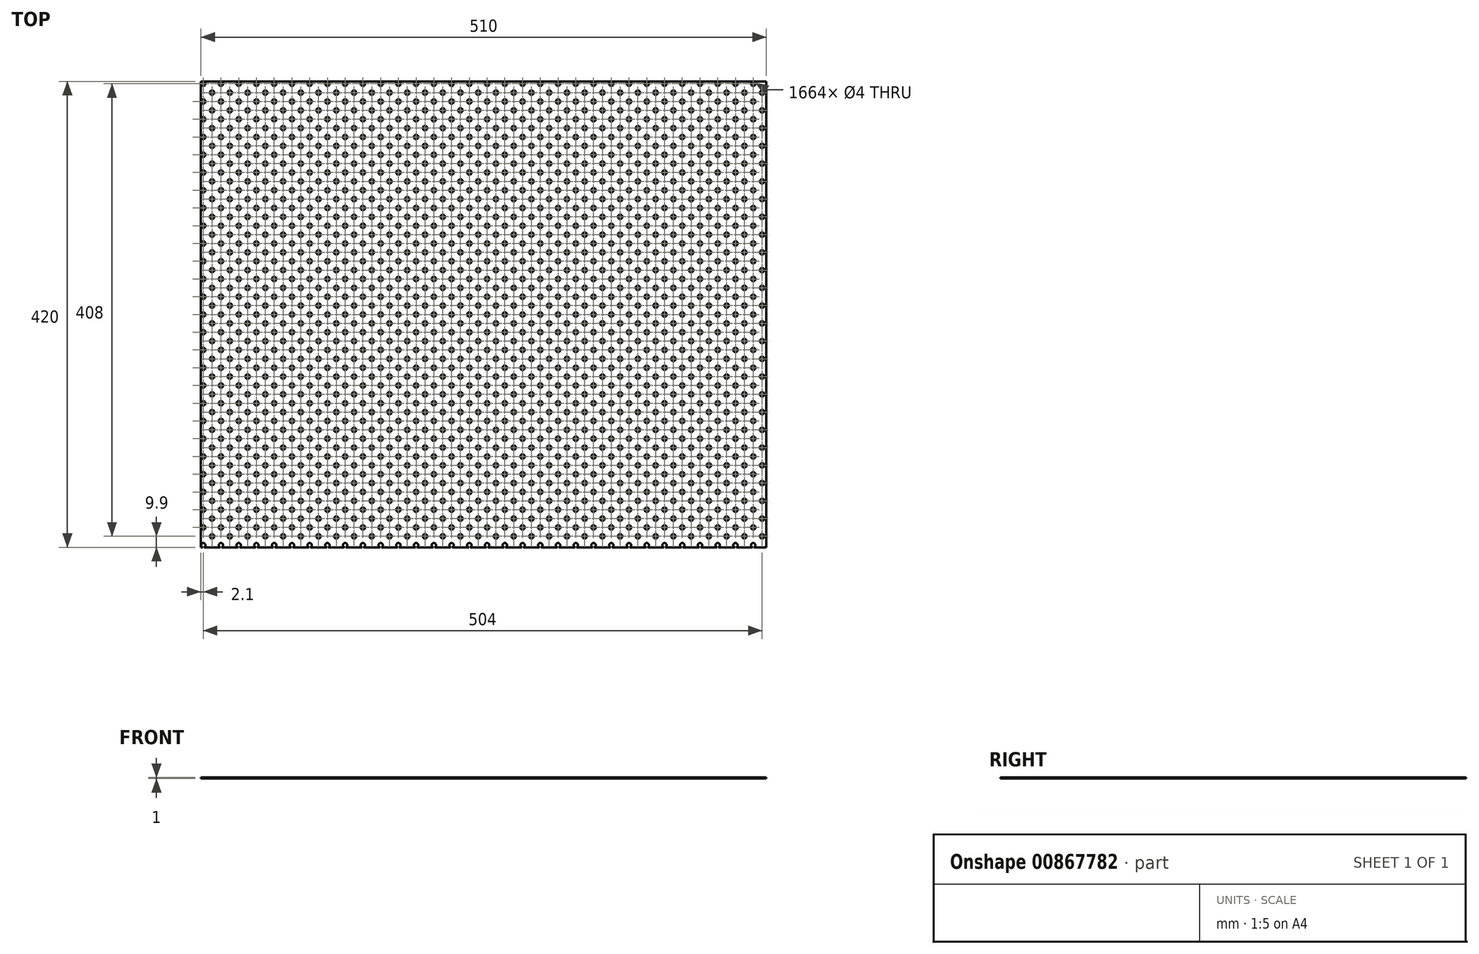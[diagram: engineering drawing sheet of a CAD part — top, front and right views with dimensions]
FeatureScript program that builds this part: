
annotation { "Feature Type Name" : "Feature", "Feature Type Description" : "" }
export const myFeature = defineFeature(function(context is Context, id is Id, definition is map)
    precondition{}
    {
        {
            var Q0;
            Q0=qCreatedBy(makeId("Top.planeOp"),FACE);
            var sketch = newSketch(context, id + "F0", { "sketchPlane" : qUnion([Q0])});
            skLineSegment(sketch, "E0.bottom", {"start": v(-115.44, 0) * mm, "end": v(394.56, 0) * mm});
            skLineSegment(sketch, "E0.top", {"start": v(-115.44, -420) * mm, "end": v(394.56, -420) * mm});
            skLineSegment(sketch, "E0.left", {"start": v(-115.44, 0) * mm, "end": v(-115.44, -420) * mm});
            skLineSegment(sketch, "E0.right", {"start": v(394.56, 0) * mm, "end": v(394.56, -420) * mm});
            skCircle(sketch, "E1", {"center": v(-113.34, -2.1) * mm, "radius": 2 * mm});
            skCircle(sketch, "E2.0.1.0", {"center": v(-113.34, -18.1) * mm, "radius": 2 * mm});
            skCircle(sketch, "E2.0.2.0", {"center": v(-113.34, -34.1) * mm, "radius": 2 * mm});
            skCircle(sketch, "E2.0.3.0", {"center": v(-113.34, -50.1) * mm, "radius": 2 * mm});
            skCircle(sketch, "E2.0.4.0", {"center": v(-113.34, -66.1) * mm, "radius": 2 * mm});
            skCircle(sketch, "E2.0.5.0", {"center": v(-113.34, -82.1) * mm, "radius": 2 * mm});
            skCircle(sketch, "E2.0.6.0", {"center": v(-113.34, -98.1) * mm, "radius": 2 * mm});
            skCircle(sketch, "E2.0.7.0", {"center": v(-113.34, -114.1) * mm, "radius": 2 * mm});
            skCircle(sketch, "E2.0.8.0", {"center": v(-113.34, -130.1) * mm, "radius": 2 * mm});
            skCircle(sketch, "E2.0.9.0", {"center": v(-113.34, -146.1) * mm, "radius": 2 * mm});
            skCircle(sketch, "E2.0.10.0", {"center": v(-113.34, -162.1) * mm, "radius": 2 * mm});
            skCircle(sketch, "E2.0.11.0", {"center": v(-113.34, -178.1) * mm, "radius": 2 * mm});
            skCircle(sketch, "E2.0.12.0", {"center": v(-113.34, -194.1) * mm, "radius": 2 * mm});
            skCircle(sketch, "E2.0.13.0", {"center": v(-113.34, -210.1) * mm, "radius": 2 * mm});
            skCircle(sketch, "E2.0.14.0", {"center": v(-113.34, -226.1) * mm, "radius": 2 * mm});
            skCircle(sketch, "E2.0.15.0", {"center": v(-113.34, -242.1) * mm, "radius": 2 * mm});
            skCircle(sketch, "E2.0.16.0", {"center": v(-113.34, -258.1) * mm, "radius": 2 * mm});
            skCircle(sketch, "E2.0.17.0", {"center": v(-113.34, -274.1) * mm, "radius": 2 * mm});
            skCircle(sketch, "E2.0.18.0", {"center": v(-113.34, -290.1) * mm, "radius": 2 * mm});
            skCircle(sketch, "E2.0.19.0", {"center": v(-113.34, -306.1) * mm, "radius": 2 * mm});
            skCircle(sketch, "E2.0.20.0", {"center": v(-113.34, -322.1) * mm, "radius": 2 * mm});
            skCircle(sketch, "E2.0.21.0", {"center": v(-113.34, -338.1) * mm, "radius": 2 * mm});
            skCircle(sketch, "E2.0.22.0", {"center": v(-113.34, -354.1) * mm, "radius": 2 * mm});
            skCircle(sketch, "E2.0.23.0", {"center": v(-113.34, -370.1) * mm, "radius": 2 * mm});
            skCircle(sketch, "E2.0.24.0", {"center": v(-113.34, -386.1) * mm, "radius": 2 * mm});
            skCircle(sketch, "E2.1.0.0", {"center": v(-97.34, -2.1) * mm, "radius": 2 * mm});
            skCircle(sketch, "E2.1.1.0", {"center": v(-97.34, -18.1) * mm, "radius": 2 * mm});
            skCircle(sketch, "E2.1.2.0", {"center": v(-97.34, -34.1) * mm, "radius": 2 * mm});
            skCircle(sketch, "E2.1.3.0", {"center": v(-97.34, -50.1) * mm, "radius": 2 * mm});
            skCircle(sketch, "E2.1.4.0", {"center": v(-97.34, -66.1) * mm, "radius": 2 * mm});
            skCircle(sketch, "E2.1.5.0", {"center": v(-97.34, -82.1) * mm, "radius": 2 * mm});
            skCircle(sketch, "E2.1.6.0", {"center": v(-97.34, -98.1) * mm, "radius": 2 * mm});
            skCircle(sketch, "E2.1.7.0", {"center": v(-97.34, -114.1) * mm, "radius": 2 * mm});
            skCircle(sketch, "E2.1.8.0", {"center": v(-97.34, -130.1) * mm, "radius": 2 * mm});
            skCircle(sketch, "E2.1.9.0", {"center": v(-97.34, -146.1) * mm, "radius": 2 * mm});
            skCircle(sketch, "E2.1.10.0", {"center": v(-97.34, -162.1) * mm, "radius": 2 * mm});
            skCircle(sketch, "E2.1.11.0", {"center": v(-97.34, -178.1) * mm, "radius": 2 * mm});
            skCircle(sketch, "E2.1.12.0", {"center": v(-97.34, -194.1) * mm, "radius": 2 * mm});
            skCircle(sketch, "E2.1.13.0", {"center": v(-97.34, -210.1) * mm, "radius": 2 * mm});
            skCircle(sketch, "E2.1.14.0", {"center": v(-97.34, -226.1) * mm, "radius": 2 * mm});
            skCircle(sketch, "E2.1.15.0", {"center": v(-97.34, -242.1) * mm, "radius": 2 * mm});
            skCircle(sketch, "E2.1.16.0", {"center": v(-97.34, -258.1) * mm, "radius": 2 * mm});
            skCircle(sketch, "E2.1.17.0", {"center": v(-97.34, -274.1) * mm, "radius": 2 * mm});
            skCircle(sketch, "E2.1.18.0", {"center": v(-97.34, -290.1) * mm, "radius": 2 * mm});
            skCircle(sketch, "E2.1.19.0", {"center": v(-97.34, -306.1) * mm, "radius": 2 * mm});
            skCircle(sketch, "E2.1.20.0", {"center": v(-97.34, -322.1) * mm, "radius": 2 * mm});
            skCircle(sketch, "E2.1.21.0", {"center": v(-97.34, -338.1) * mm, "radius": 2 * mm});
            skCircle(sketch, "E2.1.22.0", {"center": v(-97.34, -354.1) * mm, "radius": 2 * mm});
            skCircle(sketch, "E2.1.23.0", {"center": v(-97.34, -370.1) * mm, "radius": 2 * mm});
            skCircle(sketch, "E2.1.24.0", {"center": v(-97.34, -386.1) * mm, "radius": 2 * mm});
            skCircle(sketch, "E2.2.0.0", {"center": v(-81.34, -2.1) * mm, "radius": 2 * mm});
            skCircle(sketch, "E2.2.1.0", {"center": v(-81.34, -18.1) * mm, "radius": 2 * mm});
            skCircle(sketch, "E2.2.2.0", {"center": v(-81.34, -34.1) * mm, "radius": 2 * mm});
            skCircle(sketch, "E2.2.3.0", {"center": v(-81.34, -50.1) * mm, "radius": 2 * mm});
            skCircle(sketch, "E2.2.4.0", {"center": v(-81.34, -66.1) * mm, "radius": 2 * mm});
            skCircle(sketch, "E2.2.5.0", {"center": v(-81.34, -82.1) * mm, "radius": 2 * mm});
            skCircle(sketch, "E2.2.6.0", {"center": v(-81.34, -98.1) * mm, "radius": 2 * mm});
            skCircle(sketch, "E2.2.7.0", {"center": v(-81.34, -114.1) * mm, "radius": 2 * mm});
            skCircle(sketch, "E2.2.8.0", {"center": v(-81.34, -130.1) * mm, "radius": 2 * mm});
            skCircle(sketch, "E2.2.9.0", {"center": v(-81.34, -146.1) * mm, "radius": 2 * mm});
            skCircle(sketch, "E2.2.10.0", {"center": v(-81.34, -162.1) * mm, "radius": 2 * mm});
            skCircle(sketch, "E2.2.11.0", {"center": v(-81.34, -178.1) * mm, "radius": 2 * mm});
            skCircle(sketch, "E2.2.12.0", {"center": v(-81.34, -194.1) * mm, "radius": 2 * mm});
            skCircle(sketch, "E2.2.13.0", {"center": v(-81.34, -210.1) * mm, "radius": 2 * mm});
            skCircle(sketch, "E2.2.14.0", {"center": v(-81.34, -226.1) * mm, "radius": 2 * mm});
            skCircle(sketch, "E2.2.15.0", {"center": v(-81.34, -242.1) * mm, "radius": 2 * mm});
            skCircle(sketch, "E2.2.16.0", {"center": v(-81.34, -258.1) * mm, "radius": 2 * mm});
            skCircle(sketch, "E2.2.17.0", {"center": v(-81.34, -274.1) * mm, "radius": 2 * mm});
            skCircle(sketch, "E2.2.18.0", {"center": v(-81.34, -290.1) * mm, "radius": 2 * mm});
            skCircle(sketch, "E2.2.19.0", {"center": v(-81.34, -306.1) * mm, "radius": 2 * mm});
            skCircle(sketch, "E2.2.20.0", {"center": v(-81.34, -322.1) * mm, "radius": 2 * mm});
            skCircle(sketch, "E2.2.21.0", {"center": v(-81.34, -338.1) * mm, "radius": 2 * mm});
            skCircle(sketch, "E2.2.22.0", {"center": v(-81.34, -354.1) * mm, "radius": 2 * mm});
            skCircle(sketch, "E2.2.23.0", {"center": v(-81.34, -370.1) * mm, "radius": 2 * mm});
            skCircle(sketch, "E2.2.24.0", {"center": v(-81.34, -386.1) * mm, "radius": 2 * mm});
            skCircle(sketch, "E2.3.0.0", {"center": v(-65.34, -2.1) * mm, "radius": 2 * mm});
            skCircle(sketch, "E2.3.1.0", {"center": v(-65.34, -18.1) * mm, "radius": 2 * mm});
            skCircle(sketch, "E2.3.2.0", {"center": v(-65.34, -34.1) * mm, "radius": 2 * mm});
            skCircle(sketch, "E2.3.3.0", {"center": v(-65.34, -50.1) * mm, "radius": 2 * mm});
            skCircle(sketch, "E2.3.4.0", {"center": v(-65.34, -66.1) * mm, "radius": 2 * mm});
            skCircle(sketch, "E2.3.5.0", {"center": v(-65.34, -82.1) * mm, "radius": 2 * mm});
            skCircle(sketch, "E2.3.6.0", {"center": v(-65.34, -98.1) * mm, "radius": 2 * mm});
            skCircle(sketch, "E2.3.7.0", {"center": v(-65.34, -114.1) * mm, "radius": 2 * mm});
            skCircle(sketch, "E2.3.8.0", {"center": v(-65.34, -130.1) * mm, "radius": 2 * mm});
            skCircle(sketch, "E2.3.9.0", {"center": v(-65.34, -146.1) * mm, "radius": 2 * mm});
            skCircle(sketch, "E2.3.10.0", {"center": v(-65.34, -162.1) * mm, "radius": 2 * mm});
            skCircle(sketch, "E2.3.11.0", {"center": v(-65.34, -178.1) * mm, "radius": 2 * mm});
            skCircle(sketch, "E2.3.12.0", {"center": v(-65.34, -194.1) * mm, "radius": 2 * mm});
            skCircle(sketch, "E2.3.13.0", {"center": v(-65.34, -210.1) * mm, "radius": 2 * mm});
            skCircle(sketch, "E2.3.14.0", {"center": v(-65.34, -226.1) * mm, "radius": 2 * mm});
            skCircle(sketch, "E2.3.15.0", {"center": v(-65.34, -242.1) * mm, "radius": 2 * mm});
            skCircle(sketch, "E2.3.16.0", {"center": v(-65.34, -258.1) * mm, "radius": 2 * mm});
            skCircle(sketch, "E2.3.17.0", {"center": v(-65.34, -274.1) * mm, "radius": 2 * mm});
            skCircle(sketch, "E2.3.18.0", {"center": v(-65.34, -290.1) * mm, "radius": 2 * mm});
            skCircle(sketch, "E2.3.19.0", {"center": v(-65.34, -306.1) * mm, "radius": 2 * mm});
            skCircle(sketch, "E2.3.20.0", {"center": v(-65.34, -322.1) * mm, "radius": 2 * mm});
            skCircle(sketch, "E2.3.21.0", {"center": v(-65.34, -338.1) * mm, "radius": 2 * mm});
            skCircle(sketch, "E2.3.22.0", {"center": v(-65.34, -354.1) * mm, "radius": 2 * mm});
            skCircle(sketch, "E2.3.23.0", {"center": v(-65.34, -370.1) * mm, "radius": 2 * mm});
            skCircle(sketch, "E2.3.24.0", {"center": v(-65.34, -386.1) * mm, "radius": 2 * mm});
            skCircle(sketch, "E2.4.0.0", {"center": v(-49.34, -2.1) * mm, "radius": 2 * mm});
            skCircle(sketch, "E2.4.1.0", {"center": v(-49.34, -18.1) * mm, "radius": 2 * mm});
            skCircle(sketch, "E2.4.2.0", {"center": v(-49.34, -34.1) * mm, "radius": 2 * mm});
            skCircle(sketch, "E2.4.3.0", {"center": v(-49.34, -50.1) * mm, "radius": 2 * mm});
            skCircle(sketch, "E2.4.4.0", {"center": v(-49.34, -66.1) * mm, "radius": 2 * mm});
            skCircle(sketch, "E2.4.5.0", {"center": v(-49.34, -82.1) * mm, "radius": 2 * mm});
            skCircle(sketch, "E2.4.6.0", {"center": v(-49.34, -98.1) * mm, "radius": 2 * mm});
            skCircle(sketch, "E2.4.7.0", {"center": v(-49.34, -114.1) * mm, "radius": 2 * mm});
            skCircle(sketch, "E2.4.8.0", {"center": v(-49.34, -130.1) * mm, "radius": 2 * mm});
            skCircle(sketch, "E2.4.9.0", {"center": v(-49.34, -146.1) * mm, "radius": 2 * mm});
            skCircle(sketch, "E2.4.10.0", {"center": v(-49.34, -162.1) * mm, "radius": 2 * mm});
            skCircle(sketch, "E2.4.11.0", {"center": v(-49.34, -178.1) * mm, "radius": 2 * mm});
            skCircle(sketch, "E2.4.12.0", {"center": v(-49.34, -194.1) * mm, "radius": 2 * mm});
            skCircle(sketch, "E2.4.13.0", {"center": v(-49.34, -210.1) * mm, "radius": 2 * mm});
            skCircle(sketch, "E2.4.14.0", {"center": v(-49.34, -226.1) * mm, "radius": 2 * mm});
            skCircle(sketch, "E2.4.15.0", {"center": v(-49.34, -242.1) * mm, "radius": 2 * mm});
            skCircle(sketch, "E2.4.16.0", {"center": v(-49.34, -258.1) * mm, "radius": 2 * mm});
            skCircle(sketch, "E2.4.17.0", {"center": v(-49.34, -274.1) * mm, "radius": 2 * mm});
            skCircle(sketch, "E2.4.18.0", {"center": v(-49.34, -290.1) * mm, "radius": 2 * mm});
            skCircle(sketch, "E2.4.19.0", {"center": v(-49.34, -306.1) * mm, "radius": 2 * mm});
            skCircle(sketch, "E2.4.20.0", {"center": v(-49.34, -322.1) * mm, "radius": 2 * mm});
            skCircle(sketch, "E2.4.21.0", {"center": v(-49.34, -338.1) * mm, "radius": 2 * mm});
            skCircle(sketch, "E2.4.22.0", {"center": v(-49.34, -354.1) * mm, "radius": 2 * mm});
            skCircle(sketch, "E2.4.23.0", {"center": v(-49.34, -370.1) * mm, "radius": 2 * mm});
            skCircle(sketch, "E2.4.24.0", {"center": v(-49.34, -386.1) * mm, "radius": 2 * mm});
            skCircle(sketch, "E2.5.0.0", {"center": v(-33.34, -2.1) * mm, "radius": 2 * mm});
            skCircle(sketch, "E2.5.1.0", {"center": v(-33.34, -18.1) * mm, "radius": 2 * mm});
            skCircle(sketch, "E2.5.2.0", {"center": v(-33.34, -34.1) * mm, "radius": 2 * mm});
            skCircle(sketch, "E2.5.3.0", {"center": v(-33.34, -50.1) * mm, "radius": 2 * mm});
            skCircle(sketch, "E2.5.4.0", {"center": v(-33.34, -66.1) * mm, "radius": 2 * mm});
            skCircle(sketch, "E2.5.5.0", {"center": v(-33.34, -82.1) * mm, "radius": 2 * mm});
            skCircle(sketch, "E2.5.6.0", {"center": v(-33.34, -98.1) * mm, "radius": 2 * mm});
            skCircle(sketch, "E2.5.7.0", {"center": v(-33.34, -114.1) * mm, "radius": 2 * mm});
            skCircle(sketch, "E2.5.8.0", {"center": v(-33.34, -130.1) * mm, "radius": 2 * mm});
            skCircle(sketch, "E2.5.9.0", {"center": v(-33.34, -146.1) * mm, "radius": 2 * mm});
            skCircle(sketch, "E2.5.10.0", {"center": v(-33.34, -162.1) * mm, "radius": 2 * mm});
            skCircle(sketch, "E2.5.11.0", {"center": v(-33.34, -178.1) * mm, "radius": 2 * mm});
            skCircle(sketch, "E2.5.12.0", {"center": v(-33.34, -194.1) * mm, "radius": 2 * mm});
            skCircle(sketch, "E2.5.13.0", {"center": v(-33.34, -210.1) * mm, "radius": 2 * mm});
            skCircle(sketch, "E2.5.14.0", {"center": v(-33.34, -226.1) * mm, "radius": 2 * mm});
            skCircle(sketch, "E2.5.15.0", {"center": v(-33.34, -242.1) * mm, "radius": 2 * mm});
            skCircle(sketch, "E2.5.16.0", {"center": v(-33.34, -258.1) * mm, "radius": 2 * mm});
            skCircle(sketch, "E2.5.17.0", {"center": v(-33.34, -274.1) * mm, "radius": 2 * mm});
            skCircle(sketch, "E2.5.18.0", {"center": v(-33.34, -290.1) * mm, "radius": 2 * mm});
            skCircle(sketch, "E2.5.19.0", {"center": v(-33.34, -306.1) * mm, "radius": 2 * mm});
            skCircle(sketch, "E2.5.20.0", {"center": v(-33.34, -322.1) * mm, "radius": 2 * mm});
            skCircle(sketch, "E2.5.21.0", {"center": v(-33.34, -338.1) * mm, "radius": 2 * mm});
            skCircle(sketch, "E2.5.22.0", {"center": v(-33.34, -354.1) * mm, "radius": 2 * mm});
            skCircle(sketch, "E2.5.23.0", {"center": v(-33.34, -370.1) * mm, "radius": 2 * mm});
            skCircle(sketch, "E2.5.24.0", {"center": v(-33.34, -386.1) * mm, "radius": 2 * mm});
            skCircle(sketch, "E2.6.0.0", {"center": v(-17.34, -2.1) * mm, "radius": 2 * mm});
            skCircle(sketch, "E2.6.1.0", {"center": v(-17.34, -18.1) * mm, "radius": 2 * mm});
            skCircle(sketch, "E2.6.2.0", {"center": v(-17.34, -34.1) * mm, "radius": 2 * mm});
            skCircle(sketch, "E2.6.3.0", {"center": v(-17.34, -50.1) * mm, "radius": 2 * mm});
            skCircle(sketch, "E2.6.4.0", {"center": v(-17.34, -66.1) * mm, "radius": 2 * mm});
            skCircle(sketch, "E2.6.5.0", {"center": v(-17.34, -82.1) * mm, "radius": 2 * mm});
            skCircle(sketch, "E2.6.6.0", {"center": v(-17.34, -98.1) * mm, "radius": 2 * mm});
            skCircle(sketch, "E2.6.7.0", {"center": v(-17.34, -114.1) * mm, "radius": 2 * mm});
            skCircle(sketch, "E2.6.8.0", {"center": v(-17.34, -130.1) * mm, "radius": 2 * mm});
            skCircle(sketch, "E2.6.9.0", {"center": v(-17.34, -146.1) * mm, "radius": 2 * mm});
            skCircle(sketch, "E2.6.10.0", {"center": v(-17.34, -162.1) * mm, "radius": 2 * mm});
            skCircle(sketch, "E2.6.11.0", {"center": v(-17.34, -178.1) * mm, "radius": 2 * mm});
            skCircle(sketch, "E2.6.12.0", {"center": v(-17.34, -194.1) * mm, "radius": 2 * mm});
            skCircle(sketch, "E2.6.13.0", {"center": v(-17.34, -210.1) * mm, "radius": 2 * mm});
            skCircle(sketch, "E2.6.14.0", {"center": v(-17.34, -226.1) * mm, "radius": 2 * mm});
            skCircle(sketch, "E2.6.15.0", {"center": v(-17.34, -242.1) * mm, "radius": 2 * mm});
            skCircle(sketch, "E2.6.16.0", {"center": v(-17.34, -258.1) * mm, "radius": 2 * mm});
            skCircle(sketch, "E2.6.17.0", {"center": v(-17.34, -274.1) * mm, "radius": 2 * mm});
            skCircle(sketch, "E2.6.18.0", {"center": v(-17.34, -290.1) * mm, "radius": 2 * mm});
            skCircle(sketch, "E2.6.19.0", {"center": v(-17.34, -306.1) * mm, "radius": 2 * mm});
            skCircle(sketch, "E2.6.20.0", {"center": v(-17.34, -322.1) * mm, "radius": 2 * mm});
            skCircle(sketch, "E2.6.21.0", {"center": v(-17.34, -338.1) * mm, "radius": 2 * mm});
            skCircle(sketch, "E2.6.22.0", {"center": v(-17.34, -354.1) * mm, "radius": 2 * mm});
            skCircle(sketch, "E2.6.23.0", {"center": v(-17.34, -370.1) * mm, "radius": 2 * mm});
            skCircle(sketch, "E2.6.24.0", {"center": v(-17.34, -386.1) * mm, "radius": 2 * mm});
            skCircle(sketch, "E2.7.0.0", {"center": v(-1.34, -2.1) * mm, "radius": 2 * mm});
            skCircle(sketch, "E2.7.1.0", {"center": v(-1.34, -18.1) * mm, "radius": 2 * mm});
            skCircle(sketch, "E2.7.2.0", {"center": v(-1.34, -34.1) * mm, "radius": 2 * mm});
            skCircle(sketch, "E2.7.3.0", {"center": v(-1.34, -50.1) * mm, "radius": 2 * mm});
            skCircle(sketch, "E2.7.4.0", {"center": v(-1.34, -66.1) * mm, "radius": 2 * mm});
            skCircle(sketch, "E2.7.5.0", {"center": v(-1.34, -82.1) * mm, "radius": 2 * mm});
            skCircle(sketch, "E2.7.6.0", {"center": v(-1.34, -98.1) * mm, "radius": 2 * mm});
            skCircle(sketch, "E2.7.7.0", {"center": v(-1.34, -114.1) * mm, "radius": 2 * mm});
            skCircle(sketch, "E2.7.8.0", {"center": v(-1.34, -130.1) * mm, "radius": 2 * mm});
            skCircle(sketch, "E2.7.9.0", {"center": v(-1.34, -146.1) * mm, "radius": 2 * mm});
            skCircle(sketch, "E2.7.10.0", {"center": v(-1.34, -162.1) * mm, "radius": 2 * mm});
            skCircle(sketch, "E2.7.11.0", {"center": v(-1.34, -178.1) * mm, "radius": 2 * mm});
            skCircle(sketch, "E2.7.12.0", {"center": v(-1.34, -194.1) * mm, "radius": 2 * mm});
            skCircle(sketch, "E2.7.13.0", {"center": v(-1.34, -210.1) * mm, "radius": 2 * mm});
            skCircle(sketch, "E2.7.14.0", {"center": v(-1.34, -226.1) * mm, "radius": 2 * mm});
            skCircle(sketch, "E2.7.15.0", {"center": v(-1.34, -242.1) * mm, "radius": 2 * mm});
            skCircle(sketch, "E2.7.16.0", {"center": v(-1.34, -258.1) * mm, "radius": 2 * mm});
            skCircle(sketch, "E2.7.17.0", {"center": v(-1.34, -274.1) * mm, "radius": 2 * mm});
            skCircle(sketch, "E2.7.18.0", {"center": v(-1.34, -290.1) * mm, "radius": 2 * mm});
            skCircle(sketch, "E2.7.19.0", {"center": v(-1.34, -306.1) * mm, "radius": 2 * mm});
            skCircle(sketch, "E2.7.20.0", {"center": v(-1.34, -322.1) * mm, "radius": 2 * mm});
            skCircle(sketch, "E2.7.21.0", {"center": v(-1.34, -338.1) * mm, "radius": 2 * mm});
            skCircle(sketch, "E2.7.22.0", {"center": v(-1.34, -354.1) * mm, "radius": 2 * mm});
            skCircle(sketch, "E2.7.23.0", {"center": v(-1.34, -370.1) * mm, "radius": 2 * mm});
            skCircle(sketch, "E2.7.24.0", {"center": v(-1.34, -386.1) * mm, "radius": 2 * mm});
            skCircle(sketch, "E2.8.0.0", {"center": v(14.66, -2.1) * mm, "radius": 2 * mm});
            skCircle(sketch, "E2.8.1.0", {"center": v(14.66, -18.1) * mm, "radius": 2 * mm});
            skCircle(sketch, "E2.8.2.0", {"center": v(14.66, -34.1) * mm, "radius": 2 * mm});
            skCircle(sketch, "E2.8.3.0", {"center": v(14.66, -50.1) * mm, "radius": 2 * mm});
            skCircle(sketch, "E2.8.4.0", {"center": v(14.66, -66.1) * mm, "radius": 2 * mm});
            skCircle(sketch, "E2.8.5.0", {"center": v(14.66, -82.1) * mm, "radius": 2 * mm});
            skCircle(sketch, "E2.8.6.0", {"center": v(14.66, -98.1) * mm, "radius": 2 * mm});
            skCircle(sketch, "E2.8.7.0", {"center": v(14.66, -114.1) * mm, "radius": 2 * mm});
            skCircle(sketch, "E2.8.8.0", {"center": v(14.66, -130.1) * mm, "radius": 2 * mm});
            skCircle(sketch, "E2.8.9.0", {"center": v(14.66, -146.1) * mm, "radius": 2 * mm});
            skCircle(sketch, "E2.8.10.0", {"center": v(14.66, -162.1) * mm, "radius": 2 * mm});
            skCircle(sketch, "E2.8.11.0", {"center": v(14.66, -178.1) * mm, "radius": 2 * mm});
            skCircle(sketch, "E2.8.12.0", {"center": v(14.66, -194.1) * mm, "radius": 2 * mm});
            skCircle(sketch, "E2.8.13.0", {"center": v(14.66, -210.1) * mm, "radius": 2 * mm});
            skCircle(sketch, "E2.8.14.0", {"center": v(14.66, -226.1) * mm, "radius": 2 * mm});
            skCircle(sketch, "E2.8.15.0", {"center": v(14.66, -242.1) * mm, "radius": 2 * mm});
            skCircle(sketch, "E2.8.16.0", {"center": v(14.66, -258.1) * mm, "radius": 2 * mm});
            skCircle(sketch, "E2.8.17.0", {"center": v(14.66, -274.1) * mm, "radius": 2 * mm});
            skCircle(sketch, "E2.8.18.0", {"center": v(14.66, -290.1) * mm, "radius": 2 * mm});
            skCircle(sketch, "E2.8.19.0", {"center": v(14.66, -306.1) * mm, "radius": 2 * mm});
            skCircle(sketch, "E2.8.20.0", {"center": v(14.66, -322.1) * mm, "radius": 2 * mm});
            skCircle(sketch, "E2.8.21.0", {"center": v(14.66, -338.1) * mm, "radius": 2 * mm});
            skCircle(sketch, "E2.8.22.0", {"center": v(14.66, -354.1) * mm, "radius": 2 * mm});
            skCircle(sketch, "E2.8.23.0", {"center": v(14.66, -370.1) * mm, "radius": 2 * mm});
            skCircle(sketch, "E2.8.24.0", {"center": v(14.66, -386.1) * mm, "radius": 2 * mm});
            skCircle(sketch, "E2.9.0.0", {"center": v(30.66, -2.1) * mm, "radius": 2 * mm});
            skCircle(sketch, "E2.9.1.0", {"center": v(30.66, -18.1) * mm, "radius": 2 * mm});
            skCircle(sketch, "E2.9.2.0", {"center": v(30.66, -34.1) * mm, "radius": 2 * mm});
            skCircle(sketch, "E2.9.3.0", {"center": v(30.66, -50.1) * mm, "radius": 2 * mm});
            skCircle(sketch, "E2.9.4.0", {"center": v(30.66, -66.1) * mm, "radius": 2 * mm});
            skCircle(sketch, "E2.9.5.0", {"center": v(30.66, -82.1) * mm, "radius": 2 * mm});
            skCircle(sketch, "E2.9.6.0", {"center": v(30.66, -98.1) * mm, "radius": 2 * mm});
            skCircle(sketch, "E2.9.7.0", {"center": v(30.66, -114.1) * mm, "radius": 2 * mm});
            skCircle(sketch, "E2.9.8.0", {"center": v(30.66, -130.1) * mm, "radius": 2 * mm});
            skCircle(sketch, "E2.9.9.0", {"center": v(30.66, -146.1) * mm, "radius": 2 * mm});
            skCircle(sketch, "E2.9.10.0", {"center": v(30.66, -162.1) * mm, "radius": 2 * mm});
            skCircle(sketch, "E2.9.11.0", {"center": v(30.66, -178.1) * mm, "radius": 2 * mm});
            skCircle(sketch, "E2.9.12.0", {"center": v(30.66, -194.1) * mm, "radius": 2 * mm});
            skCircle(sketch, "E2.9.13.0", {"center": v(30.66, -210.1) * mm, "radius": 2 * mm});
            skCircle(sketch, "E2.9.14.0", {"center": v(30.66, -226.1) * mm, "radius": 2 * mm});
            skCircle(sketch, "E2.9.15.0", {"center": v(30.66, -242.1) * mm, "radius": 2 * mm});
            skCircle(sketch, "E2.9.16.0", {"center": v(30.66, -258.1) * mm, "radius": 2 * mm});
            skCircle(sketch, "E2.9.17.0", {"center": v(30.66, -274.1) * mm, "radius": 2 * mm});
            skCircle(sketch, "E2.9.18.0", {"center": v(30.66, -290.1) * mm, "radius": 2 * mm});
            skCircle(sketch, "E2.9.19.0", {"center": v(30.66, -306.1) * mm, "radius": 2 * mm});
            skCircle(sketch, "E2.9.20.0", {"center": v(30.66, -322.1) * mm, "radius": 2 * mm});
            skCircle(sketch, "E2.9.21.0", {"center": v(30.66, -338.1) * mm, "radius": 2 * mm});
            skCircle(sketch, "E2.9.22.0", {"center": v(30.66, -354.1) * mm, "radius": 2 * mm});
            skCircle(sketch, "E2.9.23.0", {"center": v(30.66, -370.1) * mm, "radius": 2 * mm});
            skCircle(sketch, "E2.9.24.0", {"center": v(30.66, -386.1) * mm, "radius": 2 * mm});
            skCircle(sketch, "E2.10.0.0", {"center": v(46.66, -2.1) * mm, "radius": 2 * mm});
            skCircle(sketch, "E2.10.1.0", {"center": v(46.66, -18.1) * mm, "radius": 2 * mm});
            skCircle(sketch, "E2.10.2.0", {"center": v(46.66, -34.1) * mm, "radius": 2 * mm});
            skCircle(sketch, "E2.10.3.0", {"center": v(46.66, -50.1) * mm, "radius": 2 * mm});
            skCircle(sketch, "E2.10.4.0", {"center": v(46.66, -66.1) * mm, "radius": 2 * mm});
            skCircle(sketch, "E2.10.5.0", {"center": v(46.66, -82.1) * mm, "radius": 2 * mm});
            skCircle(sketch, "E2.10.6.0", {"center": v(46.66, -98.1) * mm, "radius": 2 * mm});
            skCircle(sketch, "E2.10.7.0", {"center": v(46.66, -114.1) * mm, "radius": 2 * mm});
            skCircle(sketch, "E2.10.8.0", {"center": v(46.66, -130.1) * mm, "radius": 2 * mm});
            skCircle(sketch, "E2.10.9.0", {"center": v(46.66, -146.1) * mm, "radius": 2 * mm});
            skCircle(sketch, "E2.10.10.0", {"center": v(46.66, -162.1) * mm, "radius": 2 * mm});
            skCircle(sketch, "E2.10.11.0", {"center": v(46.66, -178.1) * mm, "radius": 2 * mm});
            skCircle(sketch, "E2.10.12.0", {"center": v(46.66, -194.1) * mm, "radius": 2 * mm});
            skCircle(sketch, "E2.10.13.0", {"center": v(46.66, -210.1) * mm, "radius": 2 * mm});
            skCircle(sketch, "E2.10.14.0", {"center": v(46.66, -226.1) * mm, "radius": 2 * mm});
            skCircle(sketch, "E2.10.15.0", {"center": v(46.66, -242.1) * mm, "radius": 2 * mm});
            skCircle(sketch, "E2.10.16.0", {"center": v(46.66, -258.1) * mm, "radius": 2 * mm});
            skCircle(sketch, "E2.10.17.0", {"center": v(46.66, -274.1) * mm, "radius": 2 * mm});
            skCircle(sketch, "E2.10.18.0", {"center": v(46.66, -290.1) * mm, "radius": 2 * mm});
            skCircle(sketch, "E2.10.19.0", {"center": v(46.66, -306.1) * mm, "radius": 2 * mm});
            skCircle(sketch, "E2.10.20.0", {"center": v(46.66, -322.1) * mm, "radius": 2 * mm});
            skCircle(sketch, "E2.10.21.0", {"center": v(46.66, -338.1) * mm, "radius": 2 * mm});
            skCircle(sketch, "E2.10.22.0", {"center": v(46.66, -354.1) * mm, "radius": 2 * mm});
            skCircle(sketch, "E2.10.23.0", {"center": v(46.66, -370.1) * mm, "radius": 2 * mm});
            skCircle(sketch, "E2.10.24.0", {"center": v(46.66, -386.1) * mm, "radius": 2 * mm});
            skCircle(sketch, "E2.11.0.0", {"center": v(62.66, -2.1) * mm, "radius": 2 * mm});
            skCircle(sketch, "E2.11.1.0", {"center": v(62.66, -18.1) * mm, "radius": 2 * mm});
            skCircle(sketch, "E2.11.2.0", {"center": v(62.66, -34.1) * mm, "radius": 2 * mm});
            skCircle(sketch, "E2.11.3.0", {"center": v(62.66, -50.1) * mm, "radius": 2 * mm});
            skCircle(sketch, "E2.11.4.0", {"center": v(62.66, -66.1) * mm, "radius": 2 * mm});
            skCircle(sketch, "E2.11.5.0", {"center": v(62.66, -82.1) * mm, "radius": 2 * mm});
            skCircle(sketch, "E2.11.6.0", {"center": v(62.66, -98.1) * mm, "radius": 2 * mm});
            skCircle(sketch, "E2.11.7.0", {"center": v(62.66, -114.1) * mm, "radius": 2 * mm});
            skCircle(sketch, "E2.11.8.0", {"center": v(62.66, -130.1) * mm, "radius": 2 * mm});
            skCircle(sketch, "E2.11.9.0", {"center": v(62.66, -146.1) * mm, "radius": 2 * mm});
            skCircle(sketch, "E2.11.10.0", {"center": v(62.66, -162.1) * mm, "radius": 2 * mm});
            skCircle(sketch, "E2.11.11.0", {"center": v(62.66, -178.1) * mm, "radius": 2 * mm});
            skCircle(sketch, "E2.11.12.0", {"center": v(62.66, -194.1) * mm, "radius": 2 * mm});
            skCircle(sketch, "E2.11.13.0", {"center": v(62.66, -210.1) * mm, "radius": 2 * mm});
            skCircle(sketch, "E2.11.14.0", {"center": v(62.66, -226.1) * mm, "radius": 2 * mm});
            skCircle(sketch, "E2.11.15.0", {"center": v(62.66, -242.1) * mm, "radius": 2 * mm});
            skCircle(sketch, "E2.11.16.0", {"center": v(62.66, -258.1) * mm, "radius": 2 * mm});
            skCircle(sketch, "E2.11.17.0", {"center": v(62.66, -274.1) * mm, "radius": 2 * mm});
            skCircle(sketch, "E2.11.18.0", {"center": v(62.66, -290.1) * mm, "radius": 2 * mm});
            skCircle(sketch, "E2.11.19.0", {"center": v(62.66, -306.1) * mm, "radius": 2 * mm});
            skCircle(sketch, "E2.11.20.0", {"center": v(62.66, -322.1) * mm, "radius": 2 * mm});
            skCircle(sketch, "E2.11.21.0", {"center": v(62.66, -338.1) * mm, "radius": 2 * mm});
            skCircle(sketch, "E2.11.22.0", {"center": v(62.66, -354.1) * mm, "radius": 2 * mm});
            skCircle(sketch, "E2.11.23.0", {"center": v(62.66, -370.1) * mm, "radius": 2 * mm});
            skCircle(sketch, "E2.11.24.0", {"center": v(62.66, -386.1) * mm, "radius": 2 * mm});
            skCircle(sketch, "E2.12.0.0", {"center": v(78.66, -2.1) * mm, "radius": 2 * mm});
            skCircle(sketch, "E2.12.1.0", {"center": v(78.66, -18.1) * mm, "radius": 2 * mm});
            skCircle(sketch, "E2.12.2.0", {"center": v(78.66, -34.1) * mm, "radius": 2 * mm});
            skCircle(sketch, "E2.12.3.0", {"center": v(78.66, -50.1) * mm, "radius": 2 * mm});
            skCircle(sketch, "E2.12.4.0", {"center": v(78.66, -66.1) * mm, "radius": 2 * mm});
            skCircle(sketch, "E2.12.5.0", {"center": v(78.66, -82.1) * mm, "radius": 2 * mm});
            skCircle(sketch, "E2.12.6.0", {"center": v(78.66, -98.1) * mm, "radius": 2 * mm});
            skCircle(sketch, "E2.12.7.0", {"center": v(78.66, -114.1) * mm, "radius": 2 * mm});
            skCircle(sketch, "E2.12.8.0", {"center": v(78.66, -130.1) * mm, "radius": 2 * mm});
            skCircle(sketch, "E2.12.9.0", {"center": v(78.66, -146.1) * mm, "radius": 2 * mm});
            skCircle(sketch, "E2.12.10.0", {"center": v(78.66, -162.1) * mm, "radius": 2 * mm});
            skCircle(sketch, "E2.12.11.0", {"center": v(78.66, -178.1) * mm, "radius": 2 * mm});
            skCircle(sketch, "E2.12.12.0", {"center": v(78.66, -194.1) * mm, "radius": 2 * mm});
            skCircle(sketch, "E2.12.13.0", {"center": v(78.66, -210.1) * mm, "radius": 2 * mm});
            skCircle(sketch, "E2.12.14.0", {"center": v(78.66, -226.1) * mm, "radius": 2 * mm});
            skCircle(sketch, "E2.12.15.0", {"center": v(78.66, -242.1) * mm, "radius": 2 * mm});
            skCircle(sketch, "E2.12.16.0", {"center": v(78.66, -258.1) * mm, "radius": 2 * mm});
            skCircle(sketch, "E2.12.17.0", {"center": v(78.66, -274.1) * mm, "radius": 2 * mm});
            skCircle(sketch, "E2.12.18.0", {"center": v(78.66, -290.1) * mm, "radius": 2 * mm});
            skCircle(sketch, "E2.12.19.0", {"center": v(78.66, -306.1) * mm, "radius": 2 * mm});
            skCircle(sketch, "E2.12.20.0", {"center": v(78.66, -322.1) * mm, "radius": 2 * mm});
            skCircle(sketch, "E2.12.21.0", {"center": v(78.66, -338.1) * mm, "radius": 2 * mm});
            skCircle(sketch, "E2.12.22.0", {"center": v(78.66, -354.1) * mm, "radius": 2 * mm});
            skCircle(sketch, "E2.12.23.0", {"center": v(78.66, -370.1) * mm, "radius": 2 * mm});
            skCircle(sketch, "E2.12.24.0", {"center": v(78.66, -386.1) * mm, "radius": 2 * mm});
            skCircle(sketch, "E2.13.0.0", {"center": v(94.66, -2.1) * mm, "radius": 2 * mm});
            skCircle(sketch, "E2.13.1.0", {"center": v(94.66, -18.1) * mm, "radius": 2 * mm});
            skCircle(sketch, "E2.13.2.0", {"center": v(94.66, -34.1) * mm, "radius": 2 * mm});
            skCircle(sketch, "E2.13.3.0", {"center": v(94.66, -50.1) * mm, "radius": 2 * mm});
            skCircle(sketch, "E2.13.4.0", {"center": v(94.66, -66.1) * mm, "radius": 2 * mm});
            skCircle(sketch, "E2.13.5.0", {"center": v(94.66, -82.1) * mm, "radius": 2 * mm});
            skCircle(sketch, "E2.13.6.0", {"center": v(94.66, -98.1) * mm, "radius": 2 * mm});
            skCircle(sketch, "E2.13.7.0", {"center": v(94.66, -114.1) * mm, "radius": 2 * mm});
            skCircle(sketch, "E2.13.8.0", {"center": v(94.66, -130.1) * mm, "radius": 2 * mm});
            skCircle(sketch, "E2.13.9.0", {"center": v(94.66, -146.1) * mm, "radius": 2 * mm});
            skCircle(sketch, "E2.13.10.0", {"center": v(94.66, -162.1) * mm, "radius": 2 * mm});
            skCircle(sketch, "E2.13.11.0", {"center": v(94.66, -178.1) * mm, "radius": 2 * mm});
            skCircle(sketch, "E2.13.12.0", {"center": v(94.66, -194.1) * mm, "radius": 2 * mm});
            skCircle(sketch, "E2.13.13.0", {"center": v(94.66, -210.1) * mm, "radius": 2 * mm});
            skCircle(sketch, "E2.13.14.0", {"center": v(94.66, -226.1) * mm, "radius": 2 * mm});
            skCircle(sketch, "E2.13.15.0", {"center": v(94.66, -242.1) * mm, "radius": 2 * mm});
            skCircle(sketch, "E2.13.16.0", {"center": v(94.66, -258.1) * mm, "radius": 2 * mm});
            skCircle(sketch, "E2.13.17.0", {"center": v(94.66, -274.1) * mm, "radius": 2 * mm});
            skCircle(sketch, "E2.13.18.0", {"center": v(94.66, -290.1) * mm, "radius": 2 * mm});
            skCircle(sketch, "E2.13.19.0", {"center": v(94.66, -306.1) * mm, "radius": 2 * mm});
            skCircle(sketch, "E2.13.20.0", {"center": v(94.66, -322.1) * mm, "radius": 2 * mm});
            skCircle(sketch, "E2.13.21.0", {"center": v(94.66, -338.1) * mm, "radius": 2 * mm});
            skCircle(sketch, "E2.13.22.0", {"center": v(94.66, -354.1) * mm, "radius": 2 * mm});
            skCircle(sketch, "E2.13.23.0", {"center": v(94.66, -370.1) * mm, "radius": 2 * mm});
            skCircle(sketch, "E2.13.24.0", {"center": v(94.66, -386.1) * mm, "radius": 2 * mm});
            skCircle(sketch, "E2.14.0.0", {"center": v(110.66, -2.1) * mm, "radius": 2 * mm});
            skCircle(sketch, "E2.14.1.0", {"center": v(110.66, -18.1) * mm, "radius": 2 * mm});
            skCircle(sketch, "E2.14.2.0", {"center": v(110.66, -34.1) * mm, "radius": 2 * mm});
            skCircle(sketch, "E2.14.3.0", {"center": v(110.66, -50.1) * mm, "radius": 2 * mm});
            skCircle(sketch, "E2.14.4.0", {"center": v(110.66, -66.1) * mm, "radius": 2 * mm});
            skCircle(sketch, "E2.14.5.0", {"center": v(110.66, -82.1) * mm, "radius": 2 * mm});
            skCircle(sketch, "E2.14.6.0", {"center": v(110.66, -98.1) * mm, "radius": 2 * mm});
            skCircle(sketch, "E2.14.7.0", {"center": v(110.66, -114.1) * mm, "radius": 2 * mm});
            skCircle(sketch, "E2.14.8.0", {"center": v(110.66, -130.1) * mm, "radius": 2 * mm});
            skCircle(sketch, "E2.14.9.0", {"center": v(110.66, -146.1) * mm, "radius": 2 * mm});
            skCircle(sketch, "E2.14.10.0", {"center": v(110.66, -162.1) * mm, "radius": 2 * mm});
            skCircle(sketch, "E2.14.11.0", {"center": v(110.66, -178.1) * mm, "radius": 2 * mm});
            skCircle(sketch, "E2.14.12.0", {"center": v(110.66, -194.1) * mm, "radius": 2 * mm});
            skCircle(sketch, "E2.14.13.0", {"center": v(110.66, -210.1) * mm, "radius": 2 * mm});
            skCircle(sketch, "E2.14.14.0", {"center": v(110.66, -226.1) * mm, "radius": 2 * mm});
            skCircle(sketch, "E2.14.15.0", {"center": v(110.66, -242.1) * mm, "radius": 2 * mm});
            skCircle(sketch, "E2.14.16.0", {"center": v(110.66, -258.1) * mm, "radius": 2 * mm});
            skCircle(sketch, "E2.14.17.0", {"center": v(110.66, -274.1) * mm, "radius": 2 * mm});
            skCircle(sketch, "E2.14.18.0", {"center": v(110.66, -290.1) * mm, "radius": 2 * mm});
            skCircle(sketch, "E2.14.19.0", {"center": v(110.66, -306.1) * mm, "radius": 2 * mm});
            skCircle(sketch, "E2.14.20.0", {"center": v(110.66, -322.1) * mm, "radius": 2 * mm});
            skCircle(sketch, "E2.14.21.0", {"center": v(110.66, -338.1) * mm, "radius": 2 * mm});
            skCircle(sketch, "E2.14.22.0", {"center": v(110.66, -354.1) * mm, "radius": 2 * mm});
            skCircle(sketch, "E2.14.23.0", {"center": v(110.66, -370.1) * mm, "radius": 2 * mm});
            skCircle(sketch, "E2.14.24.0", {"center": v(110.66, -386.1) * mm, "radius": 2 * mm});
            skCircle(sketch, "E2.15.0.0", {"center": v(126.66, -2.1) * mm, "radius": 2 * mm});
            skCircle(sketch, "E2.15.1.0", {"center": v(126.66, -18.1) * mm, "radius": 2 * mm});
            skCircle(sketch, "E2.15.2.0", {"center": v(126.66, -34.1) * mm, "radius": 2 * mm});
            skCircle(sketch, "E2.15.3.0", {"center": v(126.66, -50.1) * mm, "radius": 2 * mm});
            skCircle(sketch, "E2.15.4.0", {"center": v(126.66, -66.1) * mm, "radius": 2 * mm});
            skCircle(sketch, "E2.15.5.0", {"center": v(126.66, -82.1) * mm, "radius": 2 * mm});
            skCircle(sketch, "E2.15.6.0", {"center": v(126.66, -98.1) * mm, "radius": 2 * mm});
            skCircle(sketch, "E2.15.7.0", {"center": v(126.66, -114.1) * mm, "radius": 2 * mm});
            skCircle(sketch, "E2.15.8.0", {"center": v(126.66, -130.1) * mm, "radius": 2 * mm});
            skCircle(sketch, "E2.15.9.0", {"center": v(126.66, -146.1) * mm, "radius": 2 * mm});
            skCircle(sketch, "E2.15.10.0", {"center": v(126.66, -162.1) * mm, "radius": 2 * mm});
            skCircle(sketch, "E2.15.11.0", {"center": v(126.66, -178.1) * mm, "radius": 2 * mm});
            skCircle(sketch, "E2.15.12.0", {"center": v(126.66, -194.1) * mm, "radius": 2 * mm});
            skCircle(sketch, "E2.15.13.0", {"center": v(126.66, -210.1) * mm, "radius": 2 * mm});
            skCircle(sketch, "E2.15.14.0", {"center": v(126.66, -226.1) * mm, "radius": 2 * mm});
            skCircle(sketch, "E2.15.15.0", {"center": v(126.66, -242.1) * mm, "radius": 2 * mm});
            skCircle(sketch, "E2.15.16.0", {"center": v(126.66, -258.1) * mm, "radius": 2 * mm});
            skCircle(sketch, "E2.15.17.0", {"center": v(126.66, -274.1) * mm, "radius": 2 * mm});
            skCircle(sketch, "E2.15.18.0", {"center": v(126.66, -290.1) * mm, "radius": 2 * mm});
            skCircle(sketch, "E2.15.19.0", {"center": v(126.66, -306.1) * mm, "radius": 2 * mm});
            skCircle(sketch, "E2.15.20.0", {"center": v(126.66, -322.1) * mm, "radius": 2 * mm});
            skCircle(sketch, "E2.15.21.0", {"center": v(126.66, -338.1) * mm, "radius": 2 * mm});
            skCircle(sketch, "E2.15.22.0", {"center": v(126.66, -354.1) * mm, "radius": 2 * mm});
            skCircle(sketch, "E2.15.23.0", {"center": v(126.66, -370.1) * mm, "radius": 2 * mm});
            skCircle(sketch, "E2.15.24.0", {"center": v(126.66, -386.1) * mm, "radius": 2 * mm});
            skCircle(sketch, "E2.16.0.0", {"center": v(142.66, -2.1) * mm, "radius": 2 * mm});
            skCircle(sketch, "E2.16.1.0", {"center": v(142.66, -18.1) * mm, "radius": 2 * mm});
            skCircle(sketch, "E2.16.2.0", {"center": v(142.66, -34.1) * mm, "radius": 2 * mm});
            skCircle(sketch, "E2.16.3.0", {"center": v(142.66, -50.1) * mm, "radius": 2 * mm});
            skCircle(sketch, "E2.16.4.0", {"center": v(142.66, -66.1) * mm, "radius": 2 * mm});
            skCircle(sketch, "E2.16.5.0", {"center": v(142.66, -82.1) * mm, "radius": 2 * mm});
            skCircle(sketch, "E2.16.6.0", {"center": v(142.66, -98.1) * mm, "radius": 2 * mm});
            skCircle(sketch, "E2.16.7.0", {"center": v(142.66, -114.1) * mm, "radius": 2 * mm});
            skCircle(sketch, "E2.16.8.0", {"center": v(142.66, -130.1) * mm, "radius": 2 * mm});
            skCircle(sketch, "E2.16.9.0", {"center": v(142.66, -146.1) * mm, "radius": 2 * mm});
            skCircle(sketch, "E2.16.10.0", {"center": v(142.66, -162.1) * mm, "radius": 2 * mm});
            skCircle(sketch, "E2.16.11.0", {"center": v(142.66, -178.1) * mm, "radius": 2 * mm});
            skCircle(sketch, "E2.16.12.0", {"center": v(142.66, -194.1) * mm, "radius": 2 * mm});
            skCircle(sketch, "E2.16.13.0", {"center": v(142.66, -210.1) * mm, "radius": 2 * mm});
            skCircle(sketch, "E2.16.14.0", {"center": v(142.66, -226.1) * mm, "radius": 2 * mm});
            skCircle(sketch, "E2.16.15.0", {"center": v(142.66, -242.1) * mm, "radius": 2 * mm});
            skCircle(sketch, "E2.16.16.0", {"center": v(142.66, -258.1) * mm, "radius": 2 * mm});
            skCircle(sketch, "E2.16.17.0", {"center": v(142.66, -274.1) * mm, "radius": 2 * mm});
            skCircle(sketch, "E2.16.18.0", {"center": v(142.66, -290.1) * mm, "radius": 2 * mm});
            skCircle(sketch, "E2.16.19.0", {"center": v(142.66, -306.1) * mm, "radius": 2 * mm});
            skCircle(sketch, "E2.16.20.0", {"center": v(142.66, -322.1) * mm, "radius": 2 * mm});
            skCircle(sketch, "E2.16.21.0", {"center": v(142.66, -338.1) * mm, "radius": 2 * mm});
            skCircle(sketch, "E2.16.22.0", {"center": v(142.66, -354.1) * mm, "radius": 2 * mm});
            skCircle(sketch, "E2.16.23.0", {"center": v(142.66, -370.1) * mm, "radius": 2 * mm});
            skCircle(sketch, "E2.16.24.0", {"center": v(142.66, -386.1) * mm, "radius": 2 * mm});
            skCircle(sketch, "E2.17.0.0", {"center": v(158.66, -2.1) * mm, "radius": 2 * mm});
            skCircle(sketch, "E2.17.1.0", {"center": v(158.66, -18.1) * mm, "radius": 2 * mm});
            skCircle(sketch, "E2.17.2.0", {"center": v(158.66, -34.1) * mm, "radius": 2 * mm});
            skCircle(sketch, "E2.17.3.0", {"center": v(158.66, -50.1) * mm, "radius": 2 * mm});
            skCircle(sketch, "E2.17.4.0", {"center": v(158.66, -66.1) * mm, "radius": 2 * mm});
            skCircle(sketch, "E2.17.5.0", {"center": v(158.66, -82.1) * mm, "radius": 2 * mm});
            skCircle(sketch, "E2.17.6.0", {"center": v(158.66, -98.1) * mm, "radius": 2 * mm});
            skCircle(sketch, "E2.17.7.0", {"center": v(158.66, -114.1) * mm, "radius": 2 * mm});
            skCircle(sketch, "E2.17.8.0", {"center": v(158.66, -130.1) * mm, "radius": 2 * mm});
            skCircle(sketch, "E2.17.9.0", {"center": v(158.66, -146.1) * mm, "radius": 2 * mm});
            skCircle(sketch, "E2.17.10.0", {"center": v(158.66, -162.1) * mm, "radius": 2 * mm});
            skCircle(sketch, "E2.17.11.0", {"center": v(158.66, -178.1) * mm, "radius": 2 * mm});
            skCircle(sketch, "E2.17.12.0", {"center": v(158.66, -194.1) * mm, "radius": 2 * mm});
            skCircle(sketch, "E2.17.13.0", {"center": v(158.66, -210.1) * mm, "radius": 2 * mm});
            skCircle(sketch, "E2.17.14.0", {"center": v(158.66, -226.1) * mm, "radius": 2 * mm});
            skCircle(sketch, "E2.17.15.0", {"center": v(158.66, -242.1) * mm, "radius": 2 * mm});
            skCircle(sketch, "E2.17.16.0", {"center": v(158.66, -258.1) * mm, "radius": 2 * mm});
            skCircle(sketch, "E2.17.17.0", {"center": v(158.66, -274.1) * mm, "radius": 2 * mm});
            skCircle(sketch, "E2.17.18.0", {"center": v(158.66, -290.1) * mm, "radius": 2 * mm});
            skCircle(sketch, "E2.17.19.0", {"center": v(158.66, -306.1) * mm, "radius": 2 * mm});
            skCircle(sketch, "E2.17.20.0", {"center": v(158.66, -322.1) * mm, "radius": 2 * mm});
            skCircle(sketch, "E2.17.21.0", {"center": v(158.66, -338.1) * mm, "radius": 2 * mm});
            skCircle(sketch, "E2.17.22.0", {"center": v(158.66, -354.1) * mm, "radius": 2 * mm});
            skCircle(sketch, "E2.17.23.0", {"center": v(158.66, -370.1) * mm, "radius": 2 * mm});
            skCircle(sketch, "E2.17.24.0", {"center": v(158.66, -386.1) * mm, "radius": 2 * mm});
            skCircle(sketch, "E2.18.0.0", {"center": v(174.66, -2.1) * mm, "radius": 2 * mm});
            skCircle(sketch, "E2.18.1.0", {"center": v(174.66, -18.1) * mm, "radius": 2 * mm});
            skCircle(sketch, "E2.18.2.0", {"center": v(174.66, -34.1) * mm, "radius": 2 * mm});
            skCircle(sketch, "E2.18.3.0", {"center": v(174.66, -50.1) * mm, "radius": 2 * mm});
            skCircle(sketch, "E2.18.4.0", {"center": v(174.66, -66.1) * mm, "radius": 2 * mm});
            skCircle(sketch, "E2.18.5.0", {"center": v(174.66, -82.1) * mm, "radius": 2 * mm});
            skCircle(sketch, "E2.18.6.0", {"center": v(174.66, -98.1) * mm, "radius": 2 * mm});
            skCircle(sketch, "E2.18.7.0", {"center": v(174.66, -114.1) * mm, "radius": 2 * mm});
            skCircle(sketch, "E2.18.8.0", {"center": v(174.66, -130.1) * mm, "radius": 2 * mm});
            skCircle(sketch, "E2.18.9.0", {"center": v(174.66, -146.1) * mm, "radius": 2 * mm});
            skCircle(sketch, "E2.18.10.0", {"center": v(174.66, -162.1) * mm, "radius": 2 * mm});
            skCircle(sketch, "E2.18.11.0", {"center": v(174.66, -178.1) * mm, "radius": 2 * mm});
            skCircle(sketch, "E2.18.12.0", {"center": v(174.66, -194.1) * mm, "radius": 2 * mm});
            skCircle(sketch, "E2.18.13.0", {"center": v(174.66, -210.1) * mm, "radius": 2 * mm});
            skCircle(sketch, "E2.18.14.0", {"center": v(174.66, -226.1) * mm, "radius": 2 * mm});
            skCircle(sketch, "E2.18.15.0", {"center": v(174.66, -242.1) * mm, "radius": 2 * mm});
            skCircle(sketch, "E2.18.16.0", {"center": v(174.66, -258.1) * mm, "radius": 2 * mm});
            skCircle(sketch, "E2.18.17.0", {"center": v(174.66, -274.1) * mm, "radius": 2 * mm});
            skCircle(sketch, "E2.18.18.0", {"center": v(174.66, -290.1) * mm, "radius": 2 * mm});
            skCircle(sketch, "E2.18.19.0", {"center": v(174.66, -306.1) * mm, "radius": 2 * mm});
            skCircle(sketch, "E2.18.20.0", {"center": v(174.66, -322.1) * mm, "radius": 2 * mm});
            skCircle(sketch, "E2.18.21.0", {"center": v(174.66, -338.1) * mm, "radius": 2 * mm});
            skCircle(sketch, "E2.18.22.0", {"center": v(174.66, -354.1) * mm, "radius": 2 * mm});
            skCircle(sketch, "E2.18.23.0", {"center": v(174.66, -370.1) * mm, "radius": 2 * mm});
            skCircle(sketch, "E2.18.24.0", {"center": v(174.66, -386.1) * mm, "radius": 2 * mm});
            skCircle(sketch, "E2.19.0.0", {"center": v(190.66, -2.1) * mm, "radius": 2 * mm});
            skCircle(sketch, "E2.19.1.0", {"center": v(190.66, -18.1) * mm, "radius": 2 * mm});
            skCircle(sketch, "E2.19.2.0", {"center": v(190.66, -34.1) * mm, "radius": 2 * mm});
            skCircle(sketch, "E2.19.3.0", {"center": v(190.66, -50.1) * mm, "radius": 2 * mm});
            skCircle(sketch, "E2.19.4.0", {"center": v(190.66, -66.1) * mm, "radius": 2 * mm});
            skCircle(sketch, "E2.19.5.0", {"center": v(190.66, -82.1) * mm, "radius": 2 * mm});
            skCircle(sketch, "E2.19.6.0", {"center": v(190.66, -98.1) * mm, "radius": 2 * mm});
            skCircle(sketch, "E2.19.7.0", {"center": v(190.66, -114.1) * mm, "radius": 2 * mm});
            skCircle(sketch, "E2.19.8.0", {"center": v(190.66, -130.1) * mm, "radius": 2 * mm});
            skCircle(sketch, "E2.19.9.0", {"center": v(190.66, -146.1) * mm, "radius": 2 * mm});
            skCircle(sketch, "E2.19.10.0", {"center": v(190.66, -162.1) * mm, "radius": 2 * mm});
            skCircle(sketch, "E2.19.11.0", {"center": v(190.66, -178.1) * mm, "radius": 2 * mm});
            skCircle(sketch, "E2.19.12.0", {"center": v(190.66, -194.1) * mm, "radius": 2 * mm});
            skCircle(sketch, "E2.19.13.0", {"center": v(190.66, -210.1) * mm, "radius": 2 * mm});
            skCircle(sketch, "E2.19.14.0", {"center": v(190.66, -226.1) * mm, "radius": 2 * mm});
            skCircle(sketch, "E2.19.15.0", {"center": v(190.66, -242.1) * mm, "radius": 2 * mm});
            skCircle(sketch, "E2.19.16.0", {"center": v(190.66, -258.1) * mm, "radius": 2 * mm});
            skCircle(sketch, "E2.19.17.0", {"center": v(190.66, -274.1) * mm, "radius": 2 * mm});
            skCircle(sketch, "E2.19.18.0", {"center": v(190.66, -290.1) * mm, "radius": 2 * mm});
            skCircle(sketch, "E2.19.19.0", {"center": v(190.66, -306.1) * mm, "radius": 2 * mm});
            skCircle(sketch, "E2.19.20.0", {"center": v(190.66, -322.1) * mm, "radius": 2 * mm});
            skCircle(sketch, "E2.19.21.0", {"center": v(190.66, -338.1) * mm, "radius": 2 * mm});
            skCircle(sketch, "E2.19.22.0", {"center": v(190.66, -354.1) * mm, "radius": 2 * mm});
            skCircle(sketch, "E2.19.23.0", {"center": v(190.66, -370.1) * mm, "radius": 2 * mm});
            skCircle(sketch, "E2.19.24.0", {"center": v(190.66, -386.1) * mm, "radius": 2 * mm});
            skCircle(sketch, "E2.20.0.0", {"center": v(206.66, -2.1) * mm, "radius": 2 * mm});
            skCircle(sketch, "E2.20.1.0", {"center": v(206.66, -18.1) * mm, "radius": 2 * mm});
            skCircle(sketch, "E2.20.2.0", {"center": v(206.66, -34.1) * mm, "radius": 2 * mm});
            skCircle(sketch, "E2.20.3.0", {"center": v(206.66, -50.1) * mm, "radius": 2 * mm});
            skCircle(sketch, "E2.20.4.0", {"center": v(206.66, -66.1) * mm, "radius": 2 * mm});
            skCircle(sketch, "E2.20.5.0", {"center": v(206.66, -82.1) * mm, "radius": 2 * mm});
            skCircle(sketch, "E2.20.6.0", {"center": v(206.66, -98.1) * mm, "radius": 2 * mm});
            skCircle(sketch, "E2.20.7.0", {"center": v(206.66, -114.1) * mm, "radius": 2 * mm});
            skCircle(sketch, "E2.20.8.0", {"center": v(206.66, -130.1) * mm, "radius": 2 * mm});
            skCircle(sketch, "E2.20.9.0", {"center": v(206.66, -146.1) * mm, "radius": 2 * mm});
            skCircle(sketch, "E2.20.10.0", {"center": v(206.66, -162.1) * mm, "radius": 2 * mm});
            skCircle(sketch, "E2.20.11.0", {"center": v(206.66, -178.1) * mm, "radius": 2 * mm});
            skCircle(sketch, "E2.20.12.0", {"center": v(206.66, -194.1) * mm, "radius": 2 * mm});
            skCircle(sketch, "E2.20.13.0", {"center": v(206.66, -210.1) * mm, "radius": 2 * mm});
            skCircle(sketch, "E2.20.14.0", {"center": v(206.66, -226.1) * mm, "radius": 2 * mm});
            skCircle(sketch, "E2.20.15.0", {"center": v(206.66, -242.1) * mm, "radius": 2 * mm});
            skCircle(sketch, "E2.20.16.0", {"center": v(206.66, -258.1) * mm, "radius": 2 * mm});
            skCircle(sketch, "E2.20.17.0", {"center": v(206.66, -274.1) * mm, "radius": 2 * mm});
            skCircle(sketch, "E2.20.18.0", {"center": v(206.66, -290.1) * mm, "radius": 2 * mm});
            skCircle(sketch, "E2.20.19.0", {"center": v(206.66, -306.1) * mm, "radius": 2 * mm});
            skCircle(sketch, "E2.20.20.0", {"center": v(206.66, -322.1) * mm, "radius": 2 * mm});
            skCircle(sketch, "E2.20.21.0", {"center": v(206.66, -338.1) * mm, "radius": 2 * mm});
            skCircle(sketch, "E2.20.22.0", {"center": v(206.66, -354.1) * mm, "radius": 2 * mm});
            skCircle(sketch, "E2.20.23.0", {"center": v(206.66, -370.1) * mm, "radius": 2 * mm});
            skCircle(sketch, "E2.20.24.0", {"center": v(206.66, -386.1) * mm, "radius": 2 * mm});
            skCircle(sketch, "E2.21.0.0", {"center": v(222.66, -2.1) * mm, "radius": 2 * mm});
            skCircle(sketch, "E2.21.1.0", {"center": v(222.66, -18.1) * mm, "radius": 2 * mm});
            skCircle(sketch, "E2.21.2.0", {"center": v(222.66, -34.1) * mm, "radius": 2 * mm});
            skCircle(sketch, "E2.21.3.0", {"center": v(222.66, -50.1) * mm, "radius": 2 * mm});
            skCircle(sketch, "E2.21.4.0", {"center": v(222.66, -66.1) * mm, "radius": 2 * mm});
            skCircle(sketch, "E2.21.5.0", {"center": v(222.66, -82.1) * mm, "radius": 2 * mm});
            skCircle(sketch, "E2.21.6.0", {"center": v(222.66, -98.1) * mm, "radius": 2 * mm});
            skCircle(sketch, "E2.21.7.0", {"center": v(222.66, -114.1) * mm, "radius": 2 * mm});
            skCircle(sketch, "E2.21.8.0", {"center": v(222.66, -130.1) * mm, "radius": 2 * mm});
            skCircle(sketch, "E2.21.9.0", {"center": v(222.66, -146.1) * mm, "radius": 2 * mm});
            skCircle(sketch, "E2.21.10.0", {"center": v(222.66, -162.1) * mm, "radius": 2 * mm});
            skCircle(sketch, "E2.21.11.0", {"center": v(222.66, -178.1) * mm, "radius": 2 * mm});
            skCircle(sketch, "E2.21.12.0", {"center": v(222.66, -194.1) * mm, "radius": 2 * mm});
            skCircle(sketch, "E2.21.13.0", {"center": v(222.66, -210.1) * mm, "radius": 2 * mm});
            skCircle(sketch, "E2.21.14.0", {"center": v(222.66, -226.1) * mm, "radius": 2 * mm});
            skCircle(sketch, "E2.21.15.0", {"center": v(222.66, -242.1) * mm, "radius": 2 * mm});
            skCircle(sketch, "E2.21.16.0", {"center": v(222.66, -258.1) * mm, "radius": 2 * mm});
            skCircle(sketch, "E2.21.17.0", {"center": v(222.66, -274.1) * mm, "radius": 2 * mm});
            skCircle(sketch, "E2.21.18.0", {"center": v(222.66, -290.1) * mm, "radius": 2 * mm});
            skCircle(sketch, "E2.21.19.0", {"center": v(222.66, -306.1) * mm, "radius": 2 * mm});
            skCircle(sketch, "E2.21.20.0", {"center": v(222.66, -322.1) * mm, "radius": 2 * mm});
            skCircle(sketch, "E2.21.21.0", {"center": v(222.66, -338.1) * mm, "radius": 2 * mm});
            skCircle(sketch, "E2.21.22.0", {"center": v(222.66, -354.1) * mm, "radius": 2 * mm});
            skCircle(sketch, "E2.21.23.0", {"center": v(222.66, -370.1) * mm, "radius": 2 * mm});
            skCircle(sketch, "E2.21.24.0", {"center": v(222.66, -386.1) * mm, "radius": 2 * mm});
            skCircle(sketch, "E2.22.0.0", {"center": v(238.66, -2.1) * mm, "radius": 2 * mm});
            skCircle(sketch, "E2.22.1.0", {"center": v(238.66, -18.1) * mm, "radius": 2 * mm});
            skCircle(sketch, "E2.22.2.0", {"center": v(238.66, -34.1) * mm, "radius": 2 * mm});
            skCircle(sketch, "E2.22.3.0", {"center": v(238.66, -50.1) * mm, "radius": 2 * mm});
            skCircle(sketch, "E2.22.4.0", {"center": v(238.66, -66.1) * mm, "radius": 2 * mm});
            skCircle(sketch, "E2.22.5.0", {"center": v(238.66, -82.1) * mm, "radius": 2 * mm});
            skCircle(sketch, "E2.22.6.0", {"center": v(238.66, -98.1) * mm, "radius": 2 * mm});
            skCircle(sketch, "E2.22.7.0", {"center": v(238.66, -114.1) * mm, "radius": 2 * mm});
            skCircle(sketch, "E2.22.8.0", {"center": v(238.66, -130.1) * mm, "radius": 2 * mm});
            skCircle(sketch, "E2.22.9.0", {"center": v(238.66, -146.1) * mm, "radius": 2 * mm});
            skCircle(sketch, "E2.22.10.0", {"center": v(238.66, -162.1) * mm, "radius": 2 * mm});
            skCircle(sketch, "E2.22.11.0", {"center": v(238.66, -178.1) * mm, "radius": 2 * mm});
            skCircle(sketch, "E2.22.12.0", {"center": v(238.66, -194.1) * mm, "radius": 2 * mm});
            skCircle(sketch, "E2.22.13.0", {"center": v(238.66, -210.1) * mm, "radius": 2 * mm});
            skCircle(sketch, "E2.22.14.0", {"center": v(238.66, -226.1) * mm, "radius": 2 * mm});
            skCircle(sketch, "E2.22.15.0", {"center": v(238.66, -242.1) * mm, "radius": 2 * mm});
            skCircle(sketch, "E2.22.16.0", {"center": v(238.66, -258.1) * mm, "radius": 2 * mm});
            skCircle(sketch, "E2.22.17.0", {"center": v(238.66, -274.1) * mm, "radius": 2 * mm});
            skCircle(sketch, "E2.22.18.0", {"center": v(238.66, -290.1) * mm, "radius": 2 * mm});
            skCircle(sketch, "E2.22.19.0", {"center": v(238.66, -306.1) * mm, "radius": 2 * mm});
            skCircle(sketch, "E2.22.20.0", {"center": v(238.66, -322.1) * mm, "radius": 2 * mm});
            skCircle(sketch, "E2.22.21.0", {"center": v(238.66, -338.1) * mm, "radius": 2 * mm});
            skCircle(sketch, "E2.22.22.0", {"center": v(238.66, -354.1) * mm, "radius": 2 * mm});
            skCircle(sketch, "E2.22.23.0", {"center": v(238.66, -370.1) * mm, "radius": 2 * mm});
            skCircle(sketch, "E2.22.24.0", {"center": v(238.66, -386.1) * mm, "radius": 2 * mm});
            skCircle(sketch, "E2.23.0.0", {"center": v(254.66, -2.1) * mm, "radius": 2 * mm});
            skCircle(sketch, "E2.23.1.0", {"center": v(254.66, -18.1) * mm, "radius": 2 * mm});
            skCircle(sketch, "E2.23.2.0", {"center": v(254.66, -34.1) * mm, "radius": 2 * mm});
            skCircle(sketch, "E2.23.3.0", {"center": v(254.66, -50.1) * mm, "radius": 2 * mm});
            skCircle(sketch, "E2.23.4.0", {"center": v(254.66, -66.1) * mm, "radius": 2 * mm});
            skCircle(sketch, "E2.23.5.0", {"center": v(254.66, -82.1) * mm, "radius": 2 * mm});
            skCircle(sketch, "E2.23.6.0", {"center": v(254.66, -98.1) * mm, "radius": 2 * mm});
            skCircle(sketch, "E2.23.7.0", {"center": v(254.66, -114.1) * mm, "radius": 2 * mm});
            skCircle(sketch, "E2.23.8.0", {"center": v(254.66, -130.1) * mm, "radius": 2 * mm});
            skCircle(sketch, "E2.23.9.0", {"center": v(254.66, -146.1) * mm, "radius": 2 * mm});
            skCircle(sketch, "E2.23.10.0", {"center": v(254.66, -162.1) * mm, "radius": 2 * mm});
            skCircle(sketch, "E2.23.11.0", {"center": v(254.66, -178.1) * mm, "radius": 2 * mm});
            skCircle(sketch, "E2.23.12.0", {"center": v(254.66, -194.1) * mm, "radius": 2 * mm});
            skCircle(sketch, "E2.23.13.0", {"center": v(254.66, -210.1) * mm, "radius": 2 * mm});
            skCircle(sketch, "E2.23.14.0", {"center": v(254.66, -226.1) * mm, "radius": 2 * mm});
            skCircle(sketch, "E2.23.15.0", {"center": v(254.66, -242.1) * mm, "radius": 2 * mm});
            skCircle(sketch, "E2.23.16.0", {"center": v(254.66, -258.1) * mm, "radius": 2 * mm});
            skCircle(sketch, "E2.23.17.0", {"center": v(254.66, -274.1) * mm, "radius": 2 * mm});
            skCircle(sketch, "E2.23.18.0", {"center": v(254.66, -290.1) * mm, "radius": 2 * mm});
            skCircle(sketch, "E2.23.19.0", {"center": v(254.66, -306.1) * mm, "radius": 2 * mm});
            skCircle(sketch, "E2.23.20.0", {"center": v(254.66, -322.1) * mm, "radius": 2 * mm});
            skCircle(sketch, "E2.23.21.0", {"center": v(254.66, -338.1) * mm, "radius": 2 * mm});
            skCircle(sketch, "E2.23.22.0", {"center": v(254.66, -354.1) * mm, "radius": 2 * mm});
            skCircle(sketch, "E2.23.23.0", {"center": v(254.66, -370.1) * mm, "radius": 2 * mm});
            skCircle(sketch, "E2.23.24.0", {"center": v(254.66, -386.1) * mm, "radius": 2 * mm});
            skCircle(sketch, "E2.24.0.0", {"center": v(270.66, -2.1) * mm, "radius": 2 * mm});
            skCircle(sketch, "E2.24.1.0", {"center": v(270.66, -18.1) * mm, "radius": 2 * mm});
            skCircle(sketch, "E2.24.2.0", {"center": v(270.66, -34.1) * mm, "radius": 2 * mm});
            skCircle(sketch, "E2.24.3.0", {"center": v(270.66, -50.1) * mm, "radius": 2 * mm});
            skCircle(sketch, "E2.24.4.0", {"center": v(270.66, -66.1) * mm, "radius": 2 * mm});
            skCircle(sketch, "E2.24.5.0", {"center": v(270.66, -82.1) * mm, "radius": 2 * mm});
            skCircle(sketch, "E2.24.6.0", {"center": v(270.66, -98.1) * mm, "radius": 2 * mm});
            skCircle(sketch, "E2.24.7.0", {"center": v(270.66, -114.1) * mm, "radius": 2 * mm});
            skCircle(sketch, "E2.24.8.0", {"center": v(270.66, -130.1) * mm, "radius": 2 * mm});
            skCircle(sketch, "E2.24.9.0", {"center": v(270.66, -146.1) * mm, "radius": 2 * mm});
            skCircle(sketch, "E2.24.10.0", {"center": v(270.66, -162.1) * mm, "radius": 2 * mm});
            skCircle(sketch, "E2.24.11.0", {"center": v(270.66, -178.1) * mm, "radius": 2 * mm});
            skCircle(sketch, "E2.24.12.0", {"center": v(270.66, -194.1) * mm, "radius": 2 * mm});
            skCircle(sketch, "E2.24.13.0", {"center": v(270.66, -210.1) * mm, "radius": 2 * mm});
            skCircle(sketch, "E2.24.14.0", {"center": v(270.66, -226.1) * mm, "radius": 2 * mm});
            skCircle(sketch, "E2.24.15.0", {"center": v(270.66, -242.1) * mm, "radius": 2 * mm});
            skCircle(sketch, "E2.24.16.0", {"center": v(270.66, -258.1) * mm, "radius": 2 * mm});
            skCircle(sketch, "E2.24.17.0", {"center": v(270.66, -274.1) * mm, "radius": 2 * mm});
            skCircle(sketch, "E2.24.18.0", {"center": v(270.66, -290.1) * mm, "radius": 2 * mm});
            skCircle(sketch, "E2.24.19.0", {"center": v(270.66, -306.1) * mm, "radius": 2 * mm});
            skCircle(sketch, "E2.24.20.0", {"center": v(270.66, -322.1) * mm, "radius": 2 * mm});
            skCircle(sketch, "E2.24.21.0", {"center": v(270.66, -338.1) * mm, "radius": 2 * mm});
            skCircle(sketch, "E2.24.22.0", {"center": v(270.66, -354.1) * mm, "radius": 2 * mm});
            skCircle(sketch, "E2.24.23.0", {"center": v(270.66, -370.1) * mm, "radius": 2 * mm});
            skCircle(sketch, "E2.24.24.0", {"center": v(270.66, -386.1) * mm, "radius": 2 * mm});
            skCircle(sketch, "E2.25.0.0", {"center": v(286.66, -2.1) * mm, "radius": 2 * mm});
            skCircle(sketch, "E2.25.1.0", {"center": v(286.66, -18.1) * mm, "radius": 2 * mm});
            skCircle(sketch, "E2.25.2.0", {"center": v(286.66, -34.1) * mm, "radius": 2 * mm});
            skCircle(sketch, "E2.25.3.0", {"center": v(286.66, -50.1) * mm, "radius": 2 * mm});
            skCircle(sketch, "E2.25.4.0", {"center": v(286.66, -66.1) * mm, "radius": 2 * mm});
            skCircle(sketch, "E2.25.5.0", {"center": v(286.66, -82.1) * mm, "radius": 2 * mm});
            skCircle(sketch, "E2.25.6.0", {"center": v(286.66, -98.1) * mm, "radius": 2 * mm});
            skCircle(sketch, "E2.25.7.0", {"center": v(286.66, -114.1) * mm, "radius": 2 * mm});
            skCircle(sketch, "E2.25.8.0", {"center": v(286.66, -130.1) * mm, "radius": 2 * mm});
            skCircle(sketch, "E2.25.9.0", {"center": v(286.66, -146.1) * mm, "radius": 2 * mm});
            skCircle(sketch, "E2.25.10.0", {"center": v(286.66, -162.1) * mm, "radius": 2 * mm});
            skCircle(sketch, "E2.25.11.0", {"center": v(286.66, -178.1) * mm, "radius": 2 * mm});
            skCircle(sketch, "E2.25.12.0", {"center": v(286.66, -194.1) * mm, "radius": 2 * mm});
            skCircle(sketch, "E2.25.13.0", {"center": v(286.66, -210.1) * mm, "radius": 2 * mm});
            skCircle(sketch, "E2.25.14.0", {"center": v(286.66, -226.1) * mm, "radius": 2 * mm});
            skCircle(sketch, "E2.25.15.0", {"center": v(286.66, -242.1) * mm, "radius": 2 * mm});
            skCircle(sketch, "E2.25.16.0", {"center": v(286.66, -258.1) * mm, "radius": 2 * mm});
            skCircle(sketch, "E2.25.17.0", {"center": v(286.66, -274.1) * mm, "radius": 2 * mm});
            skCircle(sketch, "E2.25.18.0", {"center": v(286.66, -290.1) * mm, "radius": 2 * mm});
            skCircle(sketch, "E2.25.19.0", {"center": v(286.66, -306.1) * mm, "radius": 2 * mm});
            skCircle(sketch, "E2.25.20.0", {"center": v(286.66, -322.1) * mm, "radius": 2 * mm});
            skCircle(sketch, "E2.25.21.0", {"center": v(286.66, -338.1) * mm, "radius": 2 * mm});
            skCircle(sketch, "E2.25.22.0", {"center": v(286.66, -354.1) * mm, "radius": 2 * mm});
            skCircle(sketch, "E2.25.23.0", {"center": v(286.66, -370.1) * mm, "radius": 2 * mm});
            skCircle(sketch, "E2.25.24.0", {"center": v(286.66, -386.1) * mm, "radius": 2 * mm});
            skCircle(sketch, "E2.26.0.0", {"center": v(302.66, -2.1) * mm, "radius": 2 * mm});
            skCircle(sketch, "E2.26.1.0", {"center": v(302.66, -18.1) * mm, "radius": 2 * mm});
            skCircle(sketch, "E2.26.2.0", {"center": v(302.66, -34.1) * mm, "radius": 2 * mm});
            skCircle(sketch, "E2.26.3.0", {"center": v(302.66, -50.1) * mm, "radius": 2 * mm});
            skCircle(sketch, "E2.26.4.0", {"center": v(302.66, -66.1) * mm, "radius": 2 * mm});
            skCircle(sketch, "E2.26.5.0", {"center": v(302.66, -82.1) * mm, "radius": 2 * mm});
            skCircle(sketch, "E2.26.6.0", {"center": v(302.66, -98.1) * mm, "radius": 2 * mm});
            skCircle(sketch, "E2.26.7.0", {"center": v(302.66, -114.1) * mm, "radius": 2 * mm});
            skCircle(sketch, "E2.26.8.0", {"center": v(302.66, -130.1) * mm, "radius": 2 * mm});
            skCircle(sketch, "E2.26.9.0", {"center": v(302.66, -146.1) * mm, "radius": 2 * mm});
            skCircle(sketch, "E2.26.10.0", {"center": v(302.66, -162.1) * mm, "radius": 2 * mm});
            skCircle(sketch, "E2.26.11.0", {"center": v(302.66, -178.1) * mm, "radius": 2 * mm});
            skCircle(sketch, "E2.26.12.0", {"center": v(302.66, -194.1) * mm, "radius": 2 * mm});
            skCircle(sketch, "E2.26.13.0", {"center": v(302.66, -210.1) * mm, "radius": 2 * mm});
            skCircle(sketch, "E2.26.14.0", {"center": v(302.66, -226.1) * mm, "radius": 2 * mm});
            skCircle(sketch, "E2.26.15.0", {"center": v(302.66, -242.1) * mm, "radius": 2 * mm});
            skCircle(sketch, "E2.26.16.0", {"center": v(302.66, -258.1) * mm, "radius": 2 * mm});
            skCircle(sketch, "E2.26.17.0", {"center": v(302.66, -274.1) * mm, "radius": 2 * mm});
            skCircle(sketch, "E2.26.18.0", {"center": v(302.66, -290.1) * mm, "radius": 2 * mm});
            skCircle(sketch, "E2.26.19.0", {"center": v(302.66, -306.1) * mm, "radius": 2 * mm});
            skCircle(sketch, "E2.26.20.0", {"center": v(302.66, -322.1) * mm, "radius": 2 * mm});
            skCircle(sketch, "E2.26.21.0", {"center": v(302.66, -338.1) * mm, "radius": 2 * mm});
            skCircle(sketch, "E2.26.22.0", {"center": v(302.66, -354.1) * mm, "radius": 2 * mm});
            skCircle(sketch, "E2.26.23.0", {"center": v(302.66, -370.1) * mm, "radius": 2 * mm});
            skCircle(sketch, "E2.26.24.0", {"center": v(302.66, -386.1) * mm, "radius": 2 * mm});
            skCircle(sketch, "E2.27.0.0", {"center": v(318.66, -2.1) * mm, "radius": 2 * mm});
            skCircle(sketch, "E2.27.1.0", {"center": v(318.66, -18.1) * mm, "radius": 2 * mm});
            skCircle(sketch, "E2.27.2.0", {"center": v(318.66, -34.1) * mm, "radius": 2 * mm});
            skCircle(sketch, "E2.27.3.0", {"center": v(318.66, -50.1) * mm, "radius": 2 * mm});
            skCircle(sketch, "E2.27.4.0", {"center": v(318.66, -66.1) * mm, "radius": 2 * mm});
            skCircle(sketch, "E2.27.5.0", {"center": v(318.66, -82.1) * mm, "radius": 2 * mm});
            skCircle(sketch, "E2.27.6.0", {"center": v(318.66, -98.1) * mm, "radius": 2 * mm});
            skCircle(sketch, "E2.27.7.0", {"center": v(318.66, -114.1) * mm, "radius": 2 * mm});
            skCircle(sketch, "E2.27.8.0", {"center": v(318.66, -130.1) * mm, "radius": 2 * mm});
            skCircle(sketch, "E2.27.9.0", {"center": v(318.66, -146.1) * mm, "radius": 2 * mm});
            skCircle(sketch, "E2.27.10.0", {"center": v(318.66, -162.1) * mm, "radius": 2 * mm});
            skCircle(sketch, "E2.27.11.0", {"center": v(318.66, -178.1) * mm, "radius": 2 * mm});
            skCircle(sketch, "E2.27.12.0", {"center": v(318.66, -194.1) * mm, "radius": 2 * mm});
            skCircle(sketch, "E2.27.13.0", {"center": v(318.66, -210.1) * mm, "radius": 2 * mm});
            skCircle(sketch, "E2.27.14.0", {"center": v(318.66, -226.1) * mm, "radius": 2 * mm});
            skCircle(sketch, "E2.27.15.0", {"center": v(318.66, -242.1) * mm, "radius": 2 * mm});
            skCircle(sketch, "E2.27.16.0", {"center": v(318.66, -258.1) * mm, "radius": 2 * mm});
            skCircle(sketch, "E2.27.17.0", {"center": v(318.66, -274.1) * mm, "radius": 2 * mm});
            skCircle(sketch, "E2.27.18.0", {"center": v(318.66, -290.1) * mm, "radius": 2 * mm});
            skCircle(sketch, "E2.27.19.0", {"center": v(318.66, -306.1) * mm, "radius": 2 * mm});
            skCircle(sketch, "E2.27.20.0", {"center": v(318.66, -322.1) * mm, "radius": 2 * mm});
            skCircle(sketch, "E2.27.21.0", {"center": v(318.66, -338.1) * mm, "radius": 2 * mm});
            skCircle(sketch, "E2.27.22.0", {"center": v(318.66, -354.1) * mm, "radius": 2 * mm});
            skCircle(sketch, "E2.27.23.0", {"center": v(318.66, -370.1) * mm, "radius": 2 * mm});
            skCircle(sketch, "E2.27.24.0", {"center": v(318.66, -386.1) * mm, "radius": 2 * mm});
            skCircle(sketch, "E2.28.0.0", {"center": v(334.66, -2.1) * mm, "radius": 2 * mm});
            skCircle(sketch, "E2.28.1.0", {"center": v(334.66, -18.1) * mm, "radius": 2 * mm});
            skCircle(sketch, "E2.28.2.0", {"center": v(334.66, -34.1) * mm, "radius": 2 * mm});
            skCircle(sketch, "E2.28.3.0", {"center": v(334.66, -50.1) * mm, "radius": 2 * mm});
            skCircle(sketch, "E2.28.4.0", {"center": v(334.66, -66.1) * mm, "radius": 2 * mm});
            skCircle(sketch, "E2.28.5.0", {"center": v(334.66, -82.1) * mm, "radius": 2 * mm});
            skCircle(sketch, "E2.28.6.0", {"center": v(334.66, -98.1) * mm, "radius": 2 * mm});
            skCircle(sketch, "E2.28.7.0", {"center": v(334.66, -114.1) * mm, "radius": 2 * mm});
            skCircle(sketch, "E2.28.8.0", {"center": v(334.66, -130.1) * mm, "radius": 2 * mm});
            skCircle(sketch, "E2.28.9.0", {"center": v(334.66, -146.1) * mm, "radius": 2 * mm});
            skCircle(sketch, "E2.28.10.0", {"center": v(334.66, -162.1) * mm, "radius": 2 * mm});
            skCircle(sketch, "E2.28.11.0", {"center": v(334.66, -178.1) * mm, "radius": 2 * mm});
            skCircle(sketch, "E2.28.12.0", {"center": v(334.66, -194.1) * mm, "radius": 2 * mm});
            skCircle(sketch, "E2.28.13.0", {"center": v(334.66, -210.1) * mm, "radius": 2 * mm});
            skCircle(sketch, "E2.28.14.0", {"center": v(334.66, -226.1) * mm, "radius": 2 * mm});
            skCircle(sketch, "E2.28.15.0", {"center": v(334.66, -242.1) * mm, "radius": 2 * mm});
            skCircle(sketch, "E2.28.16.0", {"center": v(334.66, -258.1) * mm, "radius": 2 * mm});
            skCircle(sketch, "E2.28.17.0", {"center": v(334.66, -274.1) * mm, "radius": 2 * mm});
            skCircle(sketch, "E2.28.18.0", {"center": v(334.66, -290.1) * mm, "radius": 2 * mm});
            skCircle(sketch, "E2.28.19.0", {"center": v(334.66, -306.1) * mm, "radius": 2 * mm});
            skCircle(sketch, "E2.28.20.0", {"center": v(334.66, -322.1) * mm, "radius": 2 * mm});
            skCircle(sketch, "E2.28.21.0", {"center": v(334.66, -338.1) * mm, "radius": 2 * mm});
            skCircle(sketch, "E2.28.22.0", {"center": v(334.66, -354.1) * mm, "radius": 2 * mm});
            skCircle(sketch, "E2.28.23.0", {"center": v(334.66, -370.1) * mm, "radius": 2 * mm});
            skCircle(sketch, "E2.28.24.0", {"center": v(334.66, -386.1) * mm, "radius": 2 * mm});
            skCircle(sketch, "E2.29.0.0", {"center": v(350.66, -2.1) * mm, "radius": 2 * mm});
            skCircle(sketch, "E2.29.1.0", {"center": v(350.66, -18.1) * mm, "radius": 2 * mm});
            skCircle(sketch, "E2.29.2.0", {"center": v(350.66, -34.1) * mm, "radius": 2 * mm});
            skCircle(sketch, "E2.29.3.0", {"center": v(350.66, -50.1) * mm, "radius": 2 * mm});
            skCircle(sketch, "E2.29.4.0", {"center": v(350.66, -66.1) * mm, "radius": 2 * mm});
            skCircle(sketch, "E2.29.5.0", {"center": v(350.66, -82.1) * mm, "radius": 2 * mm});
            skCircle(sketch, "E2.29.6.0", {"center": v(350.66, -98.1) * mm, "radius": 2 * mm});
            skCircle(sketch, "E2.29.7.0", {"center": v(350.66, -114.1) * mm, "radius": 2 * mm});
            skCircle(sketch, "E2.29.8.0", {"center": v(350.66, -130.1) * mm, "radius": 2 * mm});
            skCircle(sketch, "E2.29.9.0", {"center": v(350.66, -146.1) * mm, "radius": 2 * mm});
            skCircle(sketch, "E2.29.10.0", {"center": v(350.66, -162.1) * mm, "radius": 2 * mm});
            skCircle(sketch, "E2.29.11.0", {"center": v(350.66, -178.1) * mm, "radius": 2 * mm});
            skCircle(sketch, "E2.29.12.0", {"center": v(350.66, -194.1) * mm, "radius": 2 * mm});
            skCircle(sketch, "E2.29.13.0", {"center": v(350.66, -210.1) * mm, "radius": 2 * mm});
            skCircle(sketch, "E2.29.14.0", {"center": v(350.66, -226.1) * mm, "radius": 2 * mm});
            skCircle(sketch, "E2.29.15.0", {"center": v(350.66, -242.1) * mm, "radius": 2 * mm});
            skCircle(sketch, "E2.29.16.0", {"center": v(350.66, -258.1) * mm, "radius": 2 * mm});
            skCircle(sketch, "E2.29.17.0", {"center": v(350.66, -274.1) * mm, "radius": 2 * mm});
            skCircle(sketch, "E2.29.18.0", {"center": v(350.66, -290.1) * mm, "radius": 2 * mm});
            skCircle(sketch, "E2.29.19.0", {"center": v(350.66, -306.1) * mm, "radius": 2 * mm});
            skCircle(sketch, "E2.29.20.0", {"center": v(350.66, -322.1) * mm, "radius": 2 * mm});
            skCircle(sketch, "E2.29.21.0", {"center": v(350.66, -338.1) * mm, "radius": 2 * mm});
            skCircle(sketch, "E2.29.22.0", {"center": v(350.66, -354.1) * mm, "radius": 2 * mm});
            skCircle(sketch, "E2.29.23.0", {"center": v(350.66, -370.1) * mm, "radius": 2 * mm});
            skCircle(sketch, "E2.29.24.0", {"center": v(350.66, -386.1) * mm, "radius": 2 * mm});
            skCircle(sketch, "E2.30.0.0", {"center": v(366.66, -2.1) * mm, "radius": 2 * mm});
            skCircle(sketch, "E2.30.1.0", {"center": v(366.66, -18.1) * mm, "radius": 2 * mm});
            skCircle(sketch, "E2.30.2.0", {"center": v(366.66, -34.1) * mm, "radius": 2 * mm});
            skCircle(sketch, "E2.30.3.0", {"center": v(366.66, -50.1) * mm, "radius": 2 * mm});
            skCircle(sketch, "E2.30.4.0", {"center": v(366.66, -66.1) * mm, "radius": 2 * mm});
            skCircle(sketch, "E2.30.5.0", {"center": v(366.66, -82.1) * mm, "radius": 2 * mm});
            skCircle(sketch, "E2.30.6.0", {"center": v(366.66, -98.1) * mm, "radius": 2 * mm});
            skCircle(sketch, "E2.30.7.0", {"center": v(366.66, -114.1) * mm, "radius": 2 * mm});
            skCircle(sketch, "E2.30.8.0", {"center": v(366.66, -130.1) * mm, "radius": 2 * mm});
            skCircle(sketch, "E2.30.9.0", {"center": v(366.66, -146.1) * mm, "radius": 2 * mm});
            skCircle(sketch, "E2.30.10.0", {"center": v(366.66, -162.1) * mm, "radius": 2 * mm});
            skCircle(sketch, "E2.30.11.0", {"center": v(366.66, -178.1) * mm, "radius": 2 * mm});
            skCircle(sketch, "E2.30.12.0", {"center": v(366.66, -194.1) * mm, "radius": 2 * mm});
            skCircle(sketch, "E2.30.13.0", {"center": v(366.66, -210.1) * mm, "radius": 2 * mm});
            skCircle(sketch, "E2.30.14.0", {"center": v(366.66, -226.1) * mm, "radius": 2 * mm});
            skCircle(sketch, "E2.30.15.0", {"center": v(366.66, -242.1) * mm, "radius": 2 * mm});
            skCircle(sketch, "E2.30.16.0", {"center": v(366.66, -258.1) * mm, "radius": 2 * mm});
            skCircle(sketch, "E2.30.17.0", {"center": v(366.66, -274.1) * mm, "radius": 2 * mm});
            skCircle(sketch, "E2.30.18.0", {"center": v(366.66, -290.1) * mm, "radius": 2 * mm});
            skCircle(sketch, "E2.30.19.0", {"center": v(366.66, -306.1) * mm, "radius": 2 * mm});
            skCircle(sketch, "E2.30.20.0", {"center": v(366.66, -322.1) * mm, "radius": 2 * mm});
            skCircle(sketch, "E2.30.21.0", {"center": v(366.66, -338.1) * mm, "radius": 2 * mm});
            skCircle(sketch, "E2.30.22.0", {"center": v(366.66, -354.1) * mm, "radius": 2 * mm});
            skCircle(sketch, "E2.30.23.0", {"center": v(366.66, -370.1) * mm, "radius": 2 * mm});
            skCircle(sketch, "E2.30.24.0", {"center": v(366.66, -386.1) * mm, "radius": 2 * mm});
            skLineSegment(sketch, "E2.direction1", {"start": v(-113.34, -2.1) * mm, "end": v(-97.34, -2.1) * mm, "construction": true});
            skLineSegment(sketch, "E2.direction2", {"start": v(-113.34, -2.1) * mm, "end": v(-113.34, -18.1) * mm, "construction": true});
            skCircle(sketch, "E3", {"center": v(-105.34, -10.1) * mm, "radius": 2 * mm});
            skCircle(sketch, "E4.0.1.0", {"center": v(-105.34, -26.1) * mm, "radius": 2 * mm});
            skCircle(sketch, "E4.0.2.0", {"center": v(-105.34, -42.1) * mm, "radius": 2 * mm});
            skCircle(sketch, "E4.0.3.0", {"center": v(-105.34, -58.1) * mm, "radius": 2 * mm});
            skCircle(sketch, "E4.0.4.0", {"center": v(-105.34, -74.1) * mm, "radius": 2 * mm});
            skCircle(sketch, "E4.0.5.0", {"center": v(-105.34, -90.1) * mm, "radius": 2 * mm});
            skCircle(sketch, "E4.0.6.0", {"center": v(-105.34, -106.1) * mm, "radius": 2 * mm});
            skCircle(sketch, "E4.0.7.0", {"center": v(-105.34, -122.1) * mm, "radius": 2 * mm});
            skCircle(sketch, "E4.0.8.0", {"center": v(-105.34, -138.1) * mm, "radius": 2 * mm});
            skCircle(sketch, "E4.0.9.0", {"center": v(-105.34, -154.1) * mm, "radius": 2 * mm});
            skCircle(sketch, "E4.0.10.0", {"center": v(-105.34, -170.1) * mm, "radius": 2 * mm});
            skCircle(sketch, "E4.0.11.0", {"center": v(-105.34, -186.1) * mm, "radius": 2 * mm});
            skCircle(sketch, "E4.0.12.0", {"center": v(-105.34, -202.1) * mm, "radius": 2 * mm});
            skCircle(sketch, "E4.0.13.0", {"center": v(-105.34, -218.1) * mm, "radius": 2 * mm});
            skCircle(sketch, "E4.0.14.0", {"center": v(-105.34, -234.1) * mm, "radius": 2 * mm});
            skCircle(sketch, "E4.0.15.0", {"center": v(-105.34, -250.1) * mm, "radius": 2 * mm});
            skCircle(sketch, "E4.0.16.0", {"center": v(-105.34, -266.1) * mm, "radius": 2 * mm});
            skCircle(sketch, "E4.0.17.0", {"center": v(-105.34, -282.1) * mm, "radius": 2 * mm});
            skCircle(sketch, "E4.0.18.0", {"center": v(-105.34, -298.1) * mm, "radius": 2 * mm});
            skCircle(sketch, "E4.0.19.0", {"center": v(-105.34, -314.1) * mm, "radius": 2 * mm});
            skCircle(sketch, "E4.0.20.0", {"center": v(-105.34, -330.1) * mm, "radius": 2 * mm});
            skCircle(sketch, "E4.0.21.0", {"center": v(-105.34, -346.1) * mm, "radius": 2 * mm});
            skCircle(sketch, "E4.0.22.0", {"center": v(-105.34, -362.1) * mm, "radius": 2 * mm});
            skCircle(sketch, "E4.0.23.0", {"center": v(-105.34, -378.1) * mm, "radius": 2 * mm});
            skCircle(sketch, "E4.0.24.0", {"center": v(-105.34, -394.1) * mm, "radius": 2 * mm});
            skCircle(sketch, "E4.1.0.0", {"center": v(-89.34, -10.1) * mm, "radius": 2 * mm});
            skCircle(sketch, "E4.1.1.0", {"center": v(-89.34, -26.1) * mm, "radius": 2 * mm});
            skCircle(sketch, "E4.1.2.0", {"center": v(-89.34, -42.1) * mm, "radius": 2 * mm});
            skCircle(sketch, "E4.1.3.0", {"center": v(-89.34, -58.1) * mm, "radius": 2 * mm});
            skCircle(sketch, "E4.1.4.0", {"center": v(-89.34, -74.1) * mm, "radius": 2 * mm});
            skCircle(sketch, "E4.1.5.0", {"center": v(-89.34, -90.1) * mm, "radius": 2 * mm});
            skCircle(sketch, "E4.1.6.0", {"center": v(-89.34, -106.1) * mm, "radius": 2 * mm});
            skCircle(sketch, "E4.1.7.0", {"center": v(-89.34, -122.1) * mm, "radius": 2 * mm});
            skCircle(sketch, "E4.1.8.0", {"center": v(-89.34, -138.1) * mm, "radius": 2 * mm});
            skCircle(sketch, "E4.1.9.0", {"center": v(-89.34, -154.1) * mm, "radius": 2 * mm});
            skCircle(sketch, "E4.1.10.0", {"center": v(-89.34, -170.1) * mm, "radius": 2 * mm});
            skCircle(sketch, "E4.1.11.0", {"center": v(-89.34, -186.1) * mm, "radius": 2 * mm});
            skCircle(sketch, "E4.1.12.0", {"center": v(-89.34, -202.1) * mm, "radius": 2 * mm});
            skCircle(sketch, "E4.1.13.0", {"center": v(-89.34, -218.1) * mm, "radius": 2 * mm});
            skCircle(sketch, "E4.1.14.0", {"center": v(-89.34, -234.1) * mm, "radius": 2 * mm});
            skCircle(sketch, "E4.1.15.0", {"center": v(-89.34, -250.1) * mm, "radius": 2 * mm});
            skCircle(sketch, "E4.1.16.0", {"center": v(-89.34, -266.1) * mm, "radius": 2 * mm});
            skCircle(sketch, "E4.1.17.0", {"center": v(-89.34, -282.1) * mm, "radius": 2 * mm});
            skCircle(sketch, "E4.1.18.0", {"center": v(-89.34, -298.1) * mm, "radius": 2 * mm});
            skCircle(sketch, "E4.1.19.0", {"center": v(-89.34, -314.1) * mm, "radius": 2 * mm});
            skCircle(sketch, "E4.1.20.0", {"center": v(-89.34, -330.1) * mm, "radius": 2 * mm});
            skCircle(sketch, "E4.1.21.0", {"center": v(-89.34, -346.1) * mm, "radius": 2 * mm});
            skCircle(sketch, "E4.1.22.0", {"center": v(-89.34, -362.1) * mm, "radius": 2 * mm});
            skCircle(sketch, "E4.1.23.0", {"center": v(-89.34, -378.1) * mm, "radius": 2 * mm});
            skCircle(sketch, "E4.1.24.0", {"center": v(-89.34, -394.1) * mm, "radius": 2 * mm});
            skCircle(sketch, "E4.2.0.0", {"center": v(-73.34, -10.1) * mm, "radius": 2 * mm});
            skCircle(sketch, "E4.2.1.0", {"center": v(-73.34, -26.1) * mm, "radius": 2 * mm});
            skCircle(sketch, "E4.2.2.0", {"center": v(-73.34, -42.1) * mm, "radius": 2 * mm});
            skCircle(sketch, "E4.2.3.0", {"center": v(-73.34, -58.1) * mm, "radius": 2 * mm});
            skCircle(sketch, "E4.2.4.0", {"center": v(-73.34, -74.1) * mm, "radius": 2 * mm});
            skCircle(sketch, "E4.2.5.0", {"center": v(-73.34, -90.1) * mm, "radius": 2 * mm});
            skCircle(sketch, "E4.2.6.0", {"center": v(-73.34, -106.1) * mm, "radius": 2 * mm});
            skCircle(sketch, "E4.2.7.0", {"center": v(-73.34, -122.1) * mm, "radius": 2 * mm});
            skCircle(sketch, "E4.2.8.0", {"center": v(-73.34, -138.1) * mm, "radius": 2 * mm});
            skCircle(sketch, "E4.2.9.0", {"center": v(-73.34, -154.1) * mm, "radius": 2 * mm});
            skCircle(sketch, "E4.2.10.0", {"center": v(-73.34, -170.1) * mm, "radius": 2 * mm});
            skCircle(sketch, "E4.2.11.0", {"center": v(-73.34, -186.1) * mm, "radius": 2 * mm});
            skCircle(sketch, "E4.2.12.0", {"center": v(-73.34, -202.1) * mm, "radius": 2 * mm});
            skCircle(sketch, "E4.2.13.0", {"center": v(-73.34, -218.1) * mm, "radius": 2 * mm});
            skCircle(sketch, "E4.2.14.0", {"center": v(-73.34, -234.1) * mm, "radius": 2 * mm});
            skCircle(sketch, "E4.2.15.0", {"center": v(-73.34, -250.1) * mm, "radius": 2 * mm});
            skCircle(sketch, "E4.2.16.0", {"center": v(-73.34, -266.1) * mm, "radius": 2 * mm});
            skCircle(sketch, "E4.2.17.0", {"center": v(-73.34, -282.1) * mm, "radius": 2 * mm});
            skCircle(sketch, "E4.2.18.0", {"center": v(-73.34, -298.1) * mm, "radius": 2 * mm});
            skCircle(sketch, "E4.2.19.0", {"center": v(-73.34, -314.1) * mm, "radius": 2 * mm});
            skCircle(sketch, "E4.2.20.0", {"center": v(-73.34, -330.1) * mm, "radius": 2 * mm});
            skCircle(sketch, "E4.2.21.0", {"center": v(-73.34, -346.1) * mm, "radius": 2 * mm});
            skCircle(sketch, "E4.2.22.0", {"center": v(-73.34, -362.1) * mm, "radius": 2 * mm});
            skCircle(sketch, "E4.2.23.0", {"center": v(-73.34, -378.1) * mm, "radius": 2 * mm});
            skCircle(sketch, "E4.2.24.0", {"center": v(-73.34, -394.1) * mm, "radius": 2 * mm});
            skCircle(sketch, "E4.3.0.0", {"center": v(-57.34, -10.1) * mm, "radius": 2 * mm});
            skCircle(sketch, "E4.3.1.0", {"center": v(-57.34, -26.1) * mm, "radius": 2 * mm});
            skCircle(sketch, "E4.3.2.0", {"center": v(-57.34, -42.1) * mm, "radius": 2 * mm});
            skCircle(sketch, "E4.3.3.0", {"center": v(-57.34, -58.1) * mm, "radius": 2 * mm});
            skCircle(sketch, "E4.3.4.0", {"center": v(-57.34, -74.1) * mm, "radius": 2 * mm});
            skCircle(sketch, "E4.3.5.0", {"center": v(-57.34, -90.1) * mm, "radius": 2 * mm});
            skCircle(sketch, "E4.3.6.0", {"center": v(-57.34, -106.1) * mm, "radius": 2 * mm});
            skCircle(sketch, "E4.3.7.0", {"center": v(-57.34, -122.1) * mm, "radius": 2 * mm});
            skCircle(sketch, "E4.3.8.0", {"center": v(-57.34, -138.1) * mm, "radius": 2 * mm});
            skCircle(sketch, "E4.3.9.0", {"center": v(-57.34, -154.1) * mm, "radius": 2 * mm});
            skCircle(sketch, "E4.3.10.0", {"center": v(-57.34, -170.1) * mm, "radius": 2 * mm});
            skCircle(sketch, "E4.3.11.0", {"center": v(-57.34, -186.1) * mm, "radius": 2 * mm});
            skCircle(sketch, "E4.3.12.0", {"center": v(-57.34, -202.1) * mm, "radius": 2 * mm});
            skCircle(sketch, "E4.3.13.0", {"center": v(-57.34, -218.1) * mm, "radius": 2 * mm});
            skCircle(sketch, "E4.3.14.0", {"center": v(-57.34, -234.1) * mm, "radius": 2 * mm});
            skCircle(sketch, "E4.3.15.0", {"center": v(-57.34, -250.1) * mm, "radius": 2 * mm});
            skCircle(sketch, "E4.3.16.0", {"center": v(-57.34, -266.1) * mm, "radius": 2 * mm});
            skCircle(sketch, "E4.3.17.0", {"center": v(-57.34, -282.1) * mm, "radius": 2 * mm});
            skCircle(sketch, "E4.3.18.0", {"center": v(-57.34, -298.1) * mm, "radius": 2 * mm});
            skCircle(sketch, "E4.3.19.0", {"center": v(-57.34, -314.1) * mm, "radius": 2 * mm});
            skCircle(sketch, "E4.3.20.0", {"center": v(-57.34, -330.1) * mm, "radius": 2 * mm});
            skCircle(sketch, "E4.3.21.0", {"center": v(-57.34, -346.1) * mm, "radius": 2 * mm});
            skCircle(sketch, "E4.3.22.0", {"center": v(-57.34, -362.1) * mm, "radius": 2 * mm});
            skCircle(sketch, "E4.3.23.0", {"center": v(-57.34, -378.1) * mm, "radius": 2 * mm});
            skCircle(sketch, "E4.3.24.0", {"center": v(-57.34, -394.1) * mm, "radius": 2 * mm});
            skCircle(sketch, "E4.4.0.0", {"center": v(-41.34, -10.1) * mm, "radius": 2 * mm});
            skCircle(sketch, "E4.4.1.0", {"center": v(-41.34, -26.1) * mm, "radius": 2 * mm});
            skCircle(sketch, "E4.4.2.0", {"center": v(-41.34, -42.1) * mm, "radius": 2 * mm});
            skCircle(sketch, "E4.4.3.0", {"center": v(-41.34, -58.1) * mm, "radius": 2 * mm});
            skCircle(sketch, "E4.4.4.0", {"center": v(-41.34, -74.1) * mm, "radius": 2 * mm});
            skCircle(sketch, "E4.4.5.0", {"center": v(-41.34, -90.1) * mm, "radius": 2 * mm});
            skCircle(sketch, "E4.4.6.0", {"center": v(-41.34, -106.1) * mm, "radius": 2 * mm});
            skCircle(sketch, "E4.4.7.0", {"center": v(-41.34, -122.1) * mm, "radius": 2 * mm});
            skCircle(sketch, "E4.4.8.0", {"center": v(-41.34, -138.1) * mm, "radius": 2 * mm});
            skCircle(sketch, "E4.4.9.0", {"center": v(-41.34, -154.1) * mm, "radius": 2 * mm});
            skCircle(sketch, "E4.4.10.0", {"center": v(-41.34, -170.1) * mm, "radius": 2 * mm});
            skCircle(sketch, "E4.4.11.0", {"center": v(-41.34, -186.1) * mm, "radius": 2 * mm});
            skCircle(sketch, "E4.4.12.0", {"center": v(-41.34, -202.1) * mm, "radius": 2 * mm});
            skCircle(sketch, "E4.4.13.0", {"center": v(-41.34, -218.1) * mm, "radius": 2 * mm});
            skCircle(sketch, "E4.4.14.0", {"center": v(-41.34, -234.1) * mm, "radius": 2 * mm});
            skCircle(sketch, "E4.4.15.0", {"center": v(-41.34, -250.1) * mm, "radius": 2 * mm});
            skCircle(sketch, "E4.4.16.0", {"center": v(-41.34, -266.1) * mm, "radius": 2 * mm});
            skCircle(sketch, "E4.4.17.0", {"center": v(-41.34, -282.1) * mm, "radius": 2 * mm});
            skCircle(sketch, "E4.4.18.0", {"center": v(-41.34, -298.1) * mm, "radius": 2 * mm});
            skCircle(sketch, "E4.4.19.0", {"center": v(-41.34, -314.1) * mm, "radius": 2 * mm});
            skCircle(sketch, "E4.4.20.0", {"center": v(-41.34, -330.1) * mm, "radius": 2 * mm});
            skCircle(sketch, "E4.4.21.0", {"center": v(-41.34, -346.1) * mm, "radius": 2 * mm});
            skCircle(sketch, "E4.4.22.0", {"center": v(-41.34, -362.1) * mm, "radius": 2 * mm});
            skCircle(sketch, "E4.4.23.0", {"center": v(-41.34, -378.1) * mm, "radius": 2 * mm});
            skCircle(sketch, "E4.4.24.0", {"center": v(-41.34, -394.1) * mm, "radius": 2 * mm});
            skCircle(sketch, "E4.5.0.0", {"center": v(-25.34, -10.1) * mm, "radius": 2 * mm});
            skCircle(sketch, "E4.5.1.0", {"center": v(-25.34, -26.1) * mm, "radius": 2 * mm});
            skCircle(sketch, "E4.5.2.0", {"center": v(-25.34, -42.1) * mm, "radius": 2 * mm});
            skCircle(sketch, "E4.5.3.0", {"center": v(-25.34, -58.1) * mm, "radius": 2 * mm});
            skCircle(sketch, "E4.5.4.0", {"center": v(-25.34, -74.1) * mm, "radius": 2 * mm});
            skCircle(sketch, "E4.5.5.0", {"center": v(-25.34, -90.1) * mm, "radius": 2 * mm});
            skCircle(sketch, "E4.5.6.0", {"center": v(-25.34, -106.1) * mm, "radius": 2 * mm});
            skCircle(sketch, "E4.5.7.0", {"center": v(-25.34, -122.1) * mm, "radius": 2 * mm});
            skCircle(sketch, "E4.5.8.0", {"center": v(-25.34, -138.1) * mm, "radius": 2 * mm});
            skCircle(sketch, "E4.5.9.0", {"center": v(-25.34, -154.1) * mm, "radius": 2 * mm});
            skCircle(sketch, "E4.5.10.0", {"center": v(-25.34, -170.1) * mm, "radius": 2 * mm});
            skCircle(sketch, "E4.5.11.0", {"center": v(-25.34, -186.1) * mm, "radius": 2 * mm});
            skCircle(sketch, "E4.5.12.0", {"center": v(-25.34, -202.1) * mm, "radius": 2 * mm});
            skCircle(sketch, "E4.5.13.0", {"center": v(-25.34, -218.1) * mm, "radius": 2 * mm});
            skCircle(sketch, "E4.5.14.0", {"center": v(-25.34, -234.1) * mm, "radius": 2 * mm});
            skCircle(sketch, "E4.5.15.0", {"center": v(-25.34, -250.1) * mm, "radius": 2 * mm});
            skCircle(sketch, "E4.5.16.0", {"center": v(-25.34, -266.1) * mm, "radius": 2 * mm});
            skCircle(sketch, "E4.5.17.0", {"center": v(-25.34, -282.1) * mm, "radius": 2 * mm});
            skCircle(sketch, "E4.5.18.0", {"center": v(-25.34, -298.1) * mm, "radius": 2 * mm});
            skCircle(sketch, "E4.5.19.0", {"center": v(-25.34, -314.1) * mm, "radius": 2 * mm});
            skCircle(sketch, "E4.5.20.0", {"center": v(-25.34, -330.1) * mm, "radius": 2 * mm});
            skCircle(sketch, "E4.5.21.0", {"center": v(-25.34, -346.1) * mm, "radius": 2 * mm});
            skCircle(sketch, "E4.5.22.0", {"center": v(-25.34, -362.1) * mm, "radius": 2 * mm});
            skCircle(sketch, "E4.5.23.0", {"center": v(-25.34, -378.1) * mm, "radius": 2 * mm});
            skCircle(sketch, "E4.5.24.0", {"center": v(-25.34, -394.1) * mm, "radius": 2 * mm});
            skCircle(sketch, "E4.6.0.0", {"center": v(-9.34, -10.1) * mm, "radius": 2 * mm});
            skCircle(sketch, "E4.6.1.0", {"center": v(-9.34, -26.1) * mm, "radius": 2 * mm});
            skCircle(sketch, "E4.6.2.0", {"center": v(-9.34, -42.1) * mm, "radius": 2 * mm});
            skCircle(sketch, "E4.6.3.0", {"center": v(-9.34, -58.1) * mm, "radius": 2 * mm});
            skCircle(sketch, "E4.6.4.0", {"center": v(-9.34, -74.1) * mm, "radius": 2 * mm});
            skCircle(sketch, "E4.6.5.0", {"center": v(-9.34, -90.1) * mm, "radius": 2 * mm});
            skCircle(sketch, "E4.6.6.0", {"center": v(-9.34, -106.1) * mm, "radius": 2 * mm});
            skCircle(sketch, "E4.6.7.0", {"center": v(-9.34, -122.1) * mm, "radius": 2 * mm});
            skCircle(sketch, "E4.6.8.0", {"center": v(-9.34, -138.1) * mm, "radius": 2 * mm});
            skCircle(sketch, "E4.6.9.0", {"center": v(-9.34, -154.1) * mm, "radius": 2 * mm});
            skCircle(sketch, "E4.6.10.0", {"center": v(-9.34, -170.1) * mm, "radius": 2 * mm});
            skCircle(sketch, "E4.6.11.0", {"center": v(-9.34, -186.1) * mm, "radius": 2 * mm});
            skCircle(sketch, "E4.6.12.0", {"center": v(-9.34, -202.1) * mm, "radius": 2 * mm});
            skCircle(sketch, "E4.6.13.0", {"center": v(-9.34, -218.1) * mm, "radius": 2 * mm});
            skCircle(sketch, "E4.6.14.0", {"center": v(-9.34, -234.1) * mm, "radius": 2 * mm});
            skCircle(sketch, "E4.6.15.0", {"center": v(-9.34, -250.1) * mm, "radius": 2 * mm});
            skCircle(sketch, "E4.6.16.0", {"center": v(-9.34, -266.1) * mm, "radius": 2 * mm});
            skCircle(sketch, "E4.6.17.0", {"center": v(-9.34, -282.1) * mm, "radius": 2 * mm});
            skCircle(sketch, "E4.6.18.0", {"center": v(-9.34, -298.1) * mm, "radius": 2 * mm});
            skCircle(sketch, "E4.6.19.0", {"center": v(-9.34, -314.1) * mm, "radius": 2 * mm});
            skCircle(sketch, "E4.6.20.0", {"center": v(-9.34, -330.1) * mm, "radius": 2 * mm});
            skCircle(sketch, "E4.6.21.0", {"center": v(-9.34, -346.1) * mm, "radius": 2 * mm});
            skCircle(sketch, "E4.6.22.0", {"center": v(-9.34, -362.1) * mm, "radius": 2 * mm});
            skCircle(sketch, "E4.6.23.0", {"center": v(-9.34, -378.1) * mm, "radius": 2 * mm});
            skCircle(sketch, "E4.6.24.0", {"center": v(-9.34, -394.1) * mm, "radius": 2 * mm});
            skCircle(sketch, "E4.7.0.0", {"center": v(6.66, -10.1) * mm, "radius": 2 * mm});
            skCircle(sketch, "E4.7.1.0", {"center": v(6.66, -26.1) * mm, "radius": 2 * mm});
            skCircle(sketch, "E4.7.2.0", {"center": v(6.66, -42.1) * mm, "radius": 2 * mm});
            skCircle(sketch, "E4.7.3.0", {"center": v(6.66, -58.1) * mm, "radius": 2 * mm});
            skCircle(sketch, "E4.7.4.0", {"center": v(6.66, -74.1) * mm, "radius": 2 * mm});
            skCircle(sketch, "E4.7.5.0", {"center": v(6.66, -90.1) * mm, "radius": 2 * mm});
            skCircle(sketch, "E4.7.6.0", {"center": v(6.66, -106.1) * mm, "radius": 2 * mm});
            skCircle(sketch, "E4.7.7.0", {"center": v(6.66, -122.1) * mm, "radius": 2 * mm});
            skCircle(sketch, "E4.7.8.0", {"center": v(6.66, -138.1) * mm, "radius": 2 * mm});
            skCircle(sketch, "E4.7.9.0", {"center": v(6.66, -154.1) * mm, "radius": 2 * mm});
            skCircle(sketch, "E4.7.10.0", {"center": v(6.66, -170.1) * mm, "radius": 2 * mm});
            skCircle(sketch, "E4.7.11.0", {"center": v(6.66, -186.1) * mm, "radius": 2 * mm});
            skCircle(sketch, "E4.7.12.0", {"center": v(6.66, -202.1) * mm, "radius": 2 * mm});
            skCircle(sketch, "E4.7.13.0", {"center": v(6.66, -218.1) * mm, "radius": 2 * mm});
            skCircle(sketch, "E4.7.14.0", {"center": v(6.66, -234.1) * mm, "radius": 2 * mm});
            skCircle(sketch, "E4.7.15.0", {"center": v(6.66, -250.1) * mm, "radius": 2 * mm});
            skCircle(sketch, "E4.7.16.0", {"center": v(6.66, -266.1) * mm, "radius": 2 * mm});
            skCircle(sketch, "E4.7.17.0", {"center": v(6.66, -282.1) * mm, "radius": 2 * mm});
            skCircle(sketch, "E4.7.18.0", {"center": v(6.66, -298.1) * mm, "radius": 2 * mm});
            skCircle(sketch, "E4.7.19.0", {"center": v(6.66, -314.1) * mm, "radius": 2 * mm});
            skCircle(sketch, "E4.7.20.0", {"center": v(6.66, -330.1) * mm, "radius": 2 * mm});
            skCircle(sketch, "E4.7.21.0", {"center": v(6.66, -346.1) * mm, "radius": 2 * mm});
            skCircle(sketch, "E4.7.22.0", {"center": v(6.66, -362.1) * mm, "radius": 2 * mm});
            skCircle(sketch, "E4.7.23.0", {"center": v(6.66, -378.1) * mm, "radius": 2 * mm});
            skCircle(sketch, "E4.7.24.0", {"center": v(6.66, -394.1) * mm, "radius": 2 * mm});
            skCircle(sketch, "E4.8.0.0", {"center": v(22.66, -10.1) * mm, "radius": 2 * mm});
            skCircle(sketch, "E4.8.1.0", {"center": v(22.66, -26.1) * mm, "radius": 2 * mm});
            skCircle(sketch, "E4.8.2.0", {"center": v(22.66, -42.1) * mm, "radius": 2 * mm});
            skCircle(sketch, "E4.8.3.0", {"center": v(22.66, -58.1) * mm, "radius": 2 * mm});
            skCircle(sketch, "E4.8.4.0", {"center": v(22.66, -74.1) * mm, "radius": 2 * mm});
            skCircle(sketch, "E4.8.5.0", {"center": v(22.66, -90.1) * mm, "radius": 2 * mm});
            skCircle(sketch, "E4.8.6.0", {"center": v(22.66, -106.1) * mm, "radius": 2 * mm});
            skCircle(sketch, "E4.8.7.0", {"center": v(22.66, -122.1) * mm, "radius": 2 * mm});
            skCircle(sketch, "E4.8.8.0", {"center": v(22.66, -138.1) * mm, "radius": 2 * mm});
            skCircle(sketch, "E4.8.9.0", {"center": v(22.66, -154.1) * mm, "radius": 2 * mm});
            skCircle(sketch, "E4.8.10.0", {"center": v(22.66, -170.1) * mm, "radius": 2 * mm});
            skCircle(sketch, "E4.8.11.0", {"center": v(22.66, -186.1) * mm, "radius": 2 * mm});
            skCircle(sketch, "E4.8.12.0", {"center": v(22.66, -202.1) * mm, "radius": 2 * mm});
            skCircle(sketch, "E4.8.13.0", {"center": v(22.66, -218.1) * mm, "radius": 2 * mm});
            skCircle(sketch, "E4.8.14.0", {"center": v(22.66, -234.1) * mm, "radius": 2 * mm});
            skCircle(sketch, "E4.8.15.0", {"center": v(22.66, -250.1) * mm, "radius": 2 * mm});
            skCircle(sketch, "E4.8.16.0", {"center": v(22.66, -266.1) * mm, "radius": 2 * mm});
            skCircle(sketch, "E4.8.17.0", {"center": v(22.66, -282.1) * mm, "radius": 2 * mm});
            skCircle(sketch, "E4.8.18.0", {"center": v(22.66, -298.1) * mm, "radius": 2 * mm});
            skCircle(sketch, "E4.8.19.0", {"center": v(22.66, -314.1) * mm, "radius": 2 * mm});
            skCircle(sketch, "E4.8.20.0", {"center": v(22.66, -330.1) * mm, "radius": 2 * mm});
            skCircle(sketch, "E4.8.21.0", {"center": v(22.66, -346.1) * mm, "radius": 2 * mm});
            skCircle(sketch, "E4.8.22.0", {"center": v(22.66, -362.1) * mm, "radius": 2 * mm});
            skCircle(sketch, "E4.8.23.0", {"center": v(22.66, -378.1) * mm, "radius": 2 * mm});
            skCircle(sketch, "E4.8.24.0", {"center": v(22.66, -394.1) * mm, "radius": 2 * mm});
            skCircle(sketch, "E4.9.0.0", {"center": v(38.66, -10.1) * mm, "radius": 2 * mm});
            skCircle(sketch, "E4.9.1.0", {"center": v(38.66, -26.1) * mm, "radius": 2 * mm});
            skCircle(sketch, "E4.9.2.0", {"center": v(38.66, -42.1) * mm, "radius": 2 * mm});
            skCircle(sketch, "E4.9.3.0", {"center": v(38.66, -58.1) * mm, "radius": 2 * mm});
            skCircle(sketch, "E4.9.4.0", {"center": v(38.66, -74.1) * mm, "radius": 2 * mm});
            skCircle(sketch, "E4.9.5.0", {"center": v(38.66, -90.1) * mm, "radius": 2 * mm});
            skCircle(sketch, "E4.9.6.0", {"center": v(38.66, -106.1) * mm, "radius": 2 * mm});
            skCircle(sketch, "E4.9.7.0", {"center": v(38.66, -122.1) * mm, "radius": 2 * mm});
            skCircle(sketch, "E4.9.8.0", {"center": v(38.66, -138.1) * mm, "radius": 2 * mm});
            skCircle(sketch, "E4.9.9.0", {"center": v(38.66, -154.1) * mm, "radius": 2 * mm});
            skCircle(sketch, "E4.9.10.0", {"center": v(38.66, -170.1) * mm, "radius": 2 * mm});
            skCircle(sketch, "E4.9.11.0", {"center": v(38.66, -186.1) * mm, "radius": 2 * mm});
            skCircle(sketch, "E4.9.12.0", {"center": v(38.66, -202.1) * mm, "radius": 2 * mm});
            skCircle(sketch, "E4.9.13.0", {"center": v(38.66, -218.1) * mm, "radius": 2 * mm});
            skCircle(sketch, "E4.9.14.0", {"center": v(38.66, -234.1) * mm, "radius": 2 * mm});
            skCircle(sketch, "E4.9.15.0", {"center": v(38.66, -250.1) * mm, "radius": 2 * mm});
            skCircle(sketch, "E4.9.16.0", {"center": v(38.66, -266.1) * mm, "radius": 2 * mm});
            skCircle(sketch, "E4.9.17.0", {"center": v(38.66, -282.1) * mm, "radius": 2 * mm});
            skCircle(sketch, "E4.9.18.0", {"center": v(38.66, -298.1) * mm, "radius": 2 * mm});
            skCircle(sketch, "E4.9.19.0", {"center": v(38.66, -314.1) * mm, "radius": 2 * mm});
            skCircle(sketch, "E4.9.20.0", {"center": v(38.66, -330.1) * mm, "radius": 2 * mm});
            skCircle(sketch, "E4.9.21.0", {"center": v(38.66, -346.1) * mm, "radius": 2 * mm});
            skCircle(sketch, "E4.9.22.0", {"center": v(38.66, -362.1) * mm, "radius": 2 * mm});
            skCircle(sketch, "E4.9.23.0", {"center": v(38.66, -378.1) * mm, "radius": 2 * mm});
            skCircle(sketch, "E4.9.24.0", {"center": v(38.66, -394.1) * mm, "radius": 2 * mm});
            skCircle(sketch, "E4.10.0.0", {"center": v(54.66, -10.1) * mm, "radius": 2 * mm});
            skCircle(sketch, "E4.10.1.0", {"center": v(54.66, -26.1) * mm, "radius": 2 * mm});
            skCircle(sketch, "E4.10.2.0", {"center": v(54.66, -42.1) * mm, "radius": 2 * mm});
            skCircle(sketch, "E4.10.3.0", {"center": v(54.66, -58.1) * mm, "radius": 2 * mm});
            skCircle(sketch, "E4.10.4.0", {"center": v(54.66, -74.1) * mm, "radius": 2 * mm});
            skCircle(sketch, "E4.10.5.0", {"center": v(54.66, -90.1) * mm, "radius": 2 * mm});
            skCircle(sketch, "E4.10.6.0", {"center": v(54.66, -106.1) * mm, "radius": 2 * mm});
            skCircle(sketch, "E4.10.7.0", {"center": v(54.66, -122.1) * mm, "radius": 2 * mm});
            skCircle(sketch, "E4.10.8.0", {"center": v(54.66, -138.1) * mm, "radius": 2 * mm});
            skCircle(sketch, "E4.10.9.0", {"center": v(54.66, -154.1) * mm, "radius": 2 * mm});
            skCircle(sketch, "E4.10.10.0", {"center": v(54.66, -170.1) * mm, "radius": 2 * mm});
            skCircle(sketch, "E4.10.11.0", {"center": v(54.66, -186.1) * mm, "radius": 2 * mm});
            skCircle(sketch, "E4.10.12.0", {"center": v(54.66, -202.1) * mm, "radius": 2 * mm});
            skCircle(sketch, "E4.10.13.0", {"center": v(54.66, -218.1) * mm, "radius": 2 * mm});
            skCircle(sketch, "E4.10.14.0", {"center": v(54.66, -234.1) * mm, "radius": 2 * mm});
            skCircle(sketch, "E4.10.15.0", {"center": v(54.66, -250.1) * mm, "radius": 2 * mm});
            skCircle(sketch, "E4.10.16.0", {"center": v(54.66, -266.1) * mm, "radius": 2 * mm});
            skCircle(sketch, "E4.10.17.0", {"center": v(54.66, -282.1) * mm, "radius": 2 * mm});
            skCircle(sketch, "E4.10.18.0", {"center": v(54.66, -298.1) * mm, "radius": 2 * mm});
            skCircle(sketch, "E4.10.19.0", {"center": v(54.66, -314.1) * mm, "radius": 2 * mm});
            skCircle(sketch, "E4.10.20.0", {"center": v(54.66, -330.1) * mm, "radius": 2 * mm});
            skCircle(sketch, "E4.10.21.0", {"center": v(54.66, -346.1) * mm, "radius": 2 * mm});
            skCircle(sketch, "E4.10.22.0", {"center": v(54.66, -362.1) * mm, "radius": 2 * mm});
            skCircle(sketch, "E4.10.23.0", {"center": v(54.66, -378.1) * mm, "radius": 2 * mm});
            skCircle(sketch, "E4.10.24.0", {"center": v(54.66, -394.1) * mm, "radius": 2 * mm});
            skCircle(sketch, "E4.11.0.0", {"center": v(70.66, -10.1) * mm, "radius": 2 * mm});
            skCircle(sketch, "E4.11.1.0", {"center": v(70.66, -26.1) * mm, "radius": 2 * mm});
            skCircle(sketch, "E4.11.2.0", {"center": v(70.66, -42.1) * mm, "radius": 2 * mm});
            skCircle(sketch, "E4.11.3.0", {"center": v(70.66, -58.1) * mm, "radius": 2 * mm});
            skCircle(sketch, "E4.11.4.0", {"center": v(70.66, -74.1) * mm, "radius": 2 * mm});
            skCircle(sketch, "E4.11.5.0", {"center": v(70.66, -90.1) * mm, "radius": 2 * mm});
            skCircle(sketch, "E4.11.6.0", {"center": v(70.66, -106.1) * mm, "radius": 2 * mm});
            skCircle(sketch, "E4.11.7.0", {"center": v(70.66, -122.1) * mm, "radius": 2 * mm});
            skCircle(sketch, "E4.11.8.0", {"center": v(70.66, -138.1) * mm, "radius": 2 * mm});
            skCircle(sketch, "E4.11.9.0", {"center": v(70.66, -154.1) * mm, "radius": 2 * mm});
            skCircle(sketch, "E4.11.10.0", {"center": v(70.66, -170.1) * mm, "radius": 2 * mm});
            skCircle(sketch, "E4.11.11.0", {"center": v(70.66, -186.1) * mm, "radius": 2 * mm});
            skCircle(sketch, "E4.11.12.0", {"center": v(70.66, -202.1) * mm, "radius": 2 * mm});
            skCircle(sketch, "E4.11.13.0", {"center": v(70.66, -218.1) * mm, "radius": 2 * mm});
            skCircle(sketch, "E4.11.14.0", {"center": v(70.66, -234.1) * mm, "radius": 2 * mm});
            skCircle(sketch, "E4.11.15.0", {"center": v(70.66, -250.1) * mm, "radius": 2 * mm});
            skCircle(sketch, "E4.11.16.0", {"center": v(70.66, -266.1) * mm, "radius": 2 * mm});
            skCircle(sketch, "E4.11.17.0", {"center": v(70.66, -282.1) * mm, "radius": 2 * mm});
            skCircle(sketch, "E4.11.18.0", {"center": v(70.66, -298.1) * mm, "radius": 2 * mm});
            skCircle(sketch, "E4.11.19.0", {"center": v(70.66, -314.1) * mm, "radius": 2 * mm});
            skCircle(sketch, "E4.11.20.0", {"center": v(70.66, -330.1) * mm, "radius": 2 * mm});
            skCircle(sketch, "E4.11.21.0", {"center": v(70.66, -346.1) * mm, "radius": 2 * mm});
            skCircle(sketch, "E4.11.22.0", {"center": v(70.66, -362.1) * mm, "radius": 2 * mm});
            skCircle(sketch, "E4.11.23.0", {"center": v(70.66, -378.1) * mm, "radius": 2 * mm});
            skCircle(sketch, "E4.11.24.0", {"center": v(70.66, -394.1) * mm, "radius": 2 * mm});
            skCircle(sketch, "E4.12.0.0", {"center": v(86.66, -10.1) * mm, "radius": 2 * mm});
            skCircle(sketch, "E4.12.1.0", {"center": v(86.66, -26.1) * mm, "radius": 2 * mm});
            skCircle(sketch, "E4.12.2.0", {"center": v(86.66, -42.1) * mm, "radius": 2 * mm});
            skCircle(sketch, "E4.12.3.0", {"center": v(86.66, -58.1) * mm, "radius": 2 * mm});
            skCircle(sketch, "E4.12.4.0", {"center": v(86.66, -74.1) * mm, "radius": 2 * mm});
            skCircle(sketch, "E4.12.5.0", {"center": v(86.66, -90.1) * mm, "radius": 2 * mm});
            skCircle(sketch, "E4.12.6.0", {"center": v(86.66, -106.1) * mm, "radius": 2 * mm});
            skCircle(sketch, "E4.12.7.0", {"center": v(86.66, -122.1) * mm, "radius": 2 * mm});
            skCircle(sketch, "E4.12.8.0", {"center": v(86.66, -138.1) * mm, "radius": 2 * mm});
            skCircle(sketch, "E4.12.9.0", {"center": v(86.66, -154.1) * mm, "radius": 2 * mm});
            skCircle(sketch, "E4.12.10.0", {"center": v(86.66, -170.1) * mm, "radius": 2 * mm});
            skCircle(sketch, "E4.12.11.0", {"center": v(86.66, -186.1) * mm, "radius": 2 * mm});
            skCircle(sketch, "E4.12.12.0", {"center": v(86.66, -202.1) * mm, "radius": 2 * mm});
            skCircle(sketch, "E4.12.13.0", {"center": v(86.66, -218.1) * mm, "radius": 2 * mm});
            skCircle(sketch, "E4.12.14.0", {"center": v(86.66, -234.1) * mm, "radius": 2 * mm});
            skCircle(sketch, "E4.12.15.0", {"center": v(86.66, -250.1) * mm, "radius": 2 * mm});
            skCircle(sketch, "E4.12.16.0", {"center": v(86.66, -266.1) * mm, "radius": 2 * mm});
            skCircle(sketch, "E4.12.17.0", {"center": v(86.66, -282.1) * mm, "radius": 2 * mm});
            skCircle(sketch, "E4.12.18.0", {"center": v(86.66, -298.1) * mm, "radius": 2 * mm});
            skCircle(sketch, "E4.12.19.0", {"center": v(86.66, -314.1) * mm, "radius": 2 * mm});
            skCircle(sketch, "E4.12.20.0", {"center": v(86.66, -330.1) * mm, "radius": 2 * mm});
            skCircle(sketch, "E4.12.21.0", {"center": v(86.66, -346.1) * mm, "radius": 2 * mm});
            skCircle(sketch, "E4.12.22.0", {"center": v(86.66, -362.1) * mm, "radius": 2 * mm});
            skCircle(sketch, "E4.12.23.0", {"center": v(86.66, -378.1) * mm, "radius": 2 * mm});
            skCircle(sketch, "E4.12.24.0", {"center": v(86.66, -394.1) * mm, "radius": 2 * mm});
            skCircle(sketch, "E4.13.0.0", {"center": v(102.66, -10.1) * mm, "radius": 2 * mm});
            skCircle(sketch, "E4.13.1.0", {"center": v(102.66, -26.1) * mm, "radius": 2 * mm});
            skCircle(sketch, "E4.13.2.0", {"center": v(102.66, -42.1) * mm, "radius": 2 * mm});
            skCircle(sketch, "E4.13.3.0", {"center": v(102.66, -58.1) * mm, "radius": 2 * mm});
            skCircle(sketch, "E4.13.4.0", {"center": v(102.66, -74.1) * mm, "radius": 2 * mm});
            skCircle(sketch, "E4.13.5.0", {"center": v(102.66, -90.1) * mm, "radius": 2 * mm});
            skCircle(sketch, "E4.13.6.0", {"center": v(102.66, -106.1) * mm, "radius": 2 * mm});
            skCircle(sketch, "E4.13.7.0", {"center": v(102.66, -122.1) * mm, "radius": 2 * mm});
            skCircle(sketch, "E4.13.8.0", {"center": v(102.66, -138.1) * mm, "radius": 2 * mm});
            skCircle(sketch, "E4.13.9.0", {"center": v(102.66, -154.1) * mm, "radius": 2 * mm});
            skCircle(sketch, "E4.13.10.0", {"center": v(102.66, -170.1) * mm, "radius": 2 * mm});
            skCircle(sketch, "E4.13.11.0", {"center": v(102.66, -186.1) * mm, "radius": 2 * mm});
            skCircle(sketch, "E4.13.12.0", {"center": v(102.66, -202.1) * mm, "radius": 2 * mm});
            skCircle(sketch, "E4.13.13.0", {"center": v(102.66, -218.1) * mm, "radius": 2 * mm});
            skCircle(sketch, "E4.13.14.0", {"center": v(102.66, -234.1) * mm, "radius": 2 * mm});
            skCircle(sketch, "E4.13.15.0", {"center": v(102.66, -250.1) * mm, "radius": 2 * mm});
            skCircle(sketch, "E4.13.16.0", {"center": v(102.66, -266.1) * mm, "radius": 2 * mm});
            skCircle(sketch, "E4.13.17.0", {"center": v(102.66, -282.1) * mm, "radius": 2 * mm});
            skCircle(sketch, "E4.13.18.0", {"center": v(102.66, -298.1) * mm, "radius": 2 * mm});
            skCircle(sketch, "E4.13.19.0", {"center": v(102.66, -314.1) * mm, "radius": 2 * mm});
            skCircle(sketch, "E4.13.20.0", {"center": v(102.66, -330.1) * mm, "radius": 2 * mm});
            skCircle(sketch, "E4.13.21.0", {"center": v(102.66, -346.1) * mm, "radius": 2 * mm});
            skCircle(sketch, "E4.13.22.0", {"center": v(102.66, -362.1) * mm, "radius": 2 * mm});
            skCircle(sketch, "E4.13.23.0", {"center": v(102.66, -378.1) * mm, "radius": 2 * mm});
            skCircle(sketch, "E4.13.24.0", {"center": v(102.66, -394.1) * mm, "radius": 2 * mm});
            skCircle(sketch, "E4.14.0.0", {"center": v(118.66, -10.1) * mm, "radius": 2 * mm});
            skCircle(sketch, "E4.14.1.0", {"center": v(118.66, -26.1) * mm, "radius": 2 * mm});
            skCircle(sketch, "E4.14.2.0", {"center": v(118.66, -42.1) * mm, "radius": 2 * mm});
            skCircle(sketch, "E4.14.3.0", {"center": v(118.66, -58.1) * mm, "radius": 2 * mm});
            skCircle(sketch, "E4.14.4.0", {"center": v(118.66, -74.1) * mm, "radius": 2 * mm});
            skCircle(sketch, "E4.14.5.0", {"center": v(118.66, -90.1) * mm, "radius": 2 * mm});
            skCircle(sketch, "E4.14.6.0", {"center": v(118.66, -106.1) * mm, "radius": 2 * mm});
            skCircle(sketch, "E4.14.7.0", {"center": v(118.66, -122.1) * mm, "radius": 2 * mm});
            skCircle(sketch, "E4.14.8.0", {"center": v(118.66, -138.1) * mm, "radius": 2 * mm});
            skCircle(sketch, "E4.14.9.0", {"center": v(118.66, -154.1) * mm, "radius": 2 * mm});
            skCircle(sketch, "E4.14.10.0", {"center": v(118.66, -170.1) * mm, "radius": 2 * mm});
            skCircle(sketch, "E4.14.11.0", {"center": v(118.66, -186.1) * mm, "radius": 2 * mm});
            skCircle(sketch, "E4.14.12.0", {"center": v(118.66, -202.1) * mm, "radius": 2 * mm});
            skCircle(sketch, "E4.14.13.0", {"center": v(118.66, -218.1) * mm, "radius": 2 * mm});
            skCircle(sketch, "E4.14.14.0", {"center": v(118.66, -234.1) * mm, "radius": 2 * mm});
            skCircle(sketch, "E4.14.15.0", {"center": v(118.66, -250.1) * mm, "radius": 2 * mm});
            skCircle(sketch, "E4.14.16.0", {"center": v(118.66, -266.1) * mm, "radius": 2 * mm});
            skCircle(sketch, "E4.14.17.0", {"center": v(118.66, -282.1) * mm, "radius": 2 * mm});
            skCircle(sketch, "E4.14.18.0", {"center": v(118.66, -298.1) * mm, "radius": 2 * mm});
            skCircle(sketch, "E4.14.19.0", {"center": v(118.66, -314.1) * mm, "radius": 2 * mm});
            skCircle(sketch, "E4.14.20.0", {"center": v(118.66, -330.1) * mm, "radius": 2 * mm});
            skCircle(sketch, "E4.14.21.0", {"center": v(118.66, -346.1) * mm, "radius": 2 * mm});
            skCircle(sketch, "E4.14.22.0", {"center": v(118.66, -362.1) * mm, "radius": 2 * mm});
            skCircle(sketch, "E4.14.23.0", {"center": v(118.66, -378.1) * mm, "radius": 2 * mm});
            skCircle(sketch, "E4.14.24.0", {"center": v(118.66, -394.1) * mm, "radius": 2 * mm});
            skCircle(sketch, "E4.15.0.0", {"center": v(134.66, -10.1) * mm, "radius": 2 * mm});
            skCircle(sketch, "E4.15.1.0", {"center": v(134.66, -26.1) * mm, "radius": 2 * mm});
            skCircle(sketch, "E4.15.2.0", {"center": v(134.66, -42.1) * mm, "radius": 2 * mm});
            skCircle(sketch, "E4.15.3.0", {"center": v(134.66, -58.1) * mm, "radius": 2 * mm});
            skCircle(sketch, "E4.15.4.0", {"center": v(134.66, -74.1) * mm, "radius": 2 * mm});
            skCircle(sketch, "E4.15.5.0", {"center": v(134.66, -90.1) * mm, "radius": 2 * mm});
            skCircle(sketch, "E4.15.6.0", {"center": v(134.66, -106.1) * mm, "radius": 2 * mm});
            skCircle(sketch, "E4.15.7.0", {"center": v(134.66, -122.1) * mm, "radius": 2 * mm});
            skCircle(sketch, "E4.15.8.0", {"center": v(134.66, -138.1) * mm, "radius": 2 * mm});
            skCircle(sketch, "E4.15.9.0", {"center": v(134.66, -154.1) * mm, "radius": 2 * mm});
            skCircle(sketch, "E4.15.10.0", {"center": v(134.66, -170.1) * mm, "radius": 2 * mm});
            skCircle(sketch, "E4.15.11.0", {"center": v(134.66, -186.1) * mm, "radius": 2 * mm});
            skCircle(sketch, "E4.15.12.0", {"center": v(134.66, -202.1) * mm, "radius": 2 * mm});
            skCircle(sketch, "E4.15.13.0", {"center": v(134.66, -218.1) * mm, "radius": 2 * mm});
            skCircle(sketch, "E4.15.14.0", {"center": v(134.66, -234.1) * mm, "radius": 2 * mm});
            skCircle(sketch, "E4.15.15.0", {"center": v(134.66, -250.1) * mm, "radius": 2 * mm});
            skCircle(sketch, "E4.15.16.0", {"center": v(134.66, -266.1) * mm, "radius": 2 * mm});
            skCircle(sketch, "E4.15.17.0", {"center": v(134.66, -282.1) * mm, "radius": 2 * mm});
            skCircle(sketch, "E4.15.18.0", {"center": v(134.66, -298.1) * mm, "radius": 2 * mm});
            skCircle(sketch, "E4.15.19.0", {"center": v(134.66, -314.1) * mm, "radius": 2 * mm});
            skCircle(sketch, "E4.15.20.0", {"center": v(134.66, -330.1) * mm, "radius": 2 * mm});
            skCircle(sketch, "E4.15.21.0", {"center": v(134.66, -346.1) * mm, "radius": 2 * mm});
            skCircle(sketch, "E4.15.22.0", {"center": v(134.66, -362.1) * mm, "radius": 2 * mm});
            skCircle(sketch, "E4.15.23.0", {"center": v(134.66, -378.1) * mm, "radius": 2 * mm});
            skCircle(sketch, "E4.15.24.0", {"center": v(134.66, -394.1) * mm, "radius": 2 * mm});
            skCircle(sketch, "E4.16.0.0", {"center": v(150.66, -10.1) * mm, "radius": 2 * mm});
            skCircle(sketch, "E4.16.1.0", {"center": v(150.66, -26.1) * mm, "radius": 2 * mm});
            skCircle(sketch, "E4.16.2.0", {"center": v(150.66, -42.1) * mm, "radius": 2 * mm});
            skCircle(sketch, "E4.16.3.0", {"center": v(150.66, -58.1) * mm, "radius": 2 * mm});
            skCircle(sketch, "E4.16.4.0", {"center": v(150.66, -74.1) * mm, "radius": 2 * mm});
            skCircle(sketch, "E4.16.5.0", {"center": v(150.66, -90.1) * mm, "radius": 2 * mm});
            skCircle(sketch, "E4.16.6.0", {"center": v(150.66, -106.1) * mm, "radius": 2 * mm});
            skCircle(sketch, "E4.16.7.0", {"center": v(150.66, -122.1) * mm, "radius": 2 * mm});
            skCircle(sketch, "E4.16.8.0", {"center": v(150.66, -138.1) * mm, "radius": 2 * mm});
            skCircle(sketch, "E4.16.9.0", {"center": v(150.66, -154.1) * mm, "radius": 2 * mm});
            skCircle(sketch, "E4.16.10.0", {"center": v(150.66, -170.1) * mm, "radius": 2 * mm});
            skCircle(sketch, "E4.16.11.0", {"center": v(150.66, -186.1) * mm, "radius": 2 * mm});
            skCircle(sketch, "E4.16.12.0", {"center": v(150.66, -202.1) * mm, "radius": 2 * mm});
            skCircle(sketch, "E4.16.13.0", {"center": v(150.66, -218.1) * mm, "radius": 2 * mm});
            skCircle(sketch, "E4.16.14.0", {"center": v(150.66, -234.1) * mm, "radius": 2 * mm});
            skCircle(sketch, "E4.16.15.0", {"center": v(150.66, -250.1) * mm, "radius": 2 * mm});
            skCircle(sketch, "E4.16.16.0", {"center": v(150.66, -266.1) * mm, "radius": 2 * mm});
            skCircle(sketch, "E4.16.17.0", {"center": v(150.66, -282.1) * mm, "radius": 2 * mm});
            skCircle(sketch, "E4.16.18.0", {"center": v(150.66, -298.1) * mm, "radius": 2 * mm});
            skCircle(sketch, "E4.16.19.0", {"center": v(150.66, -314.1) * mm, "radius": 2 * mm});
            skCircle(sketch, "E4.16.20.0", {"center": v(150.66, -330.1) * mm, "radius": 2 * mm});
            skCircle(sketch, "E4.16.21.0", {"center": v(150.66, -346.1) * mm, "radius": 2 * mm});
            skCircle(sketch, "E4.16.22.0", {"center": v(150.66, -362.1) * mm, "radius": 2 * mm});
            skCircle(sketch, "E4.16.23.0", {"center": v(150.66, -378.1) * mm, "radius": 2 * mm});
            skCircle(sketch, "E4.16.24.0", {"center": v(150.66, -394.1) * mm, "radius": 2 * mm});
            skCircle(sketch, "E4.17.0.0", {"center": v(166.66, -10.1) * mm, "radius": 2 * mm});
            skCircle(sketch, "E4.17.1.0", {"center": v(166.66, -26.1) * mm, "radius": 2 * mm});
            skCircle(sketch, "E4.17.2.0", {"center": v(166.66, -42.1) * mm, "radius": 2 * mm});
            skCircle(sketch, "E4.17.3.0", {"center": v(166.66, -58.1) * mm, "radius": 2 * mm});
            skCircle(sketch, "E4.17.4.0", {"center": v(166.66, -74.1) * mm, "radius": 2 * mm});
            skCircle(sketch, "E4.17.5.0", {"center": v(166.66, -90.1) * mm, "radius": 2 * mm});
            skCircle(sketch, "E4.17.6.0", {"center": v(166.66, -106.1) * mm, "radius": 2 * mm});
            skCircle(sketch, "E4.17.7.0", {"center": v(166.66, -122.1) * mm, "radius": 2 * mm});
            skCircle(sketch, "E4.17.8.0", {"center": v(166.66, -138.1) * mm, "radius": 2 * mm});
            skCircle(sketch, "E4.17.9.0", {"center": v(166.66, -154.1) * mm, "radius": 2 * mm});
            skCircle(sketch, "E4.17.10.0", {"center": v(166.66, -170.1) * mm, "radius": 2 * mm});
            skCircle(sketch, "E4.17.11.0", {"center": v(166.66, -186.1) * mm, "radius": 2 * mm});
            skCircle(sketch, "E4.17.12.0", {"center": v(166.66, -202.1) * mm, "radius": 2 * mm});
            skCircle(sketch, "E4.17.13.0", {"center": v(166.66, -218.1) * mm, "radius": 2 * mm});
            skCircle(sketch, "E4.17.14.0", {"center": v(166.66, -234.1) * mm, "radius": 2 * mm});
            skCircle(sketch, "E4.17.15.0", {"center": v(166.66, -250.1) * mm, "radius": 2 * mm});
            skCircle(sketch, "E4.17.16.0", {"center": v(166.66, -266.1) * mm, "radius": 2 * mm});
            skCircle(sketch, "E4.17.17.0", {"center": v(166.66, -282.1) * mm, "radius": 2 * mm});
            skCircle(sketch, "E4.17.18.0", {"center": v(166.66, -298.1) * mm, "radius": 2 * mm});
            skCircle(sketch, "E4.17.19.0", {"center": v(166.66, -314.1) * mm, "radius": 2 * mm});
            skCircle(sketch, "E4.17.20.0", {"center": v(166.66, -330.1) * mm, "radius": 2 * mm});
            skCircle(sketch, "E4.17.21.0", {"center": v(166.66, -346.1) * mm, "radius": 2 * mm});
            skCircle(sketch, "E4.17.22.0", {"center": v(166.66, -362.1) * mm, "radius": 2 * mm});
            skCircle(sketch, "E4.17.23.0", {"center": v(166.66, -378.1) * mm, "radius": 2 * mm});
            skCircle(sketch, "E4.17.24.0", {"center": v(166.66, -394.1) * mm, "radius": 2 * mm});
            skCircle(sketch, "E4.18.0.0", {"center": v(182.66, -10.1) * mm, "radius": 2 * mm});
            skCircle(sketch, "E4.18.1.0", {"center": v(182.66, -26.1) * mm, "radius": 2 * mm});
            skCircle(sketch, "E4.18.2.0", {"center": v(182.66, -42.1) * mm, "radius": 2 * mm});
            skCircle(sketch, "E4.18.3.0", {"center": v(182.66, -58.1) * mm, "radius": 2 * mm});
            skCircle(sketch, "E4.18.4.0", {"center": v(182.66, -74.1) * mm, "radius": 2 * mm});
            skCircle(sketch, "E4.18.5.0", {"center": v(182.66, -90.1) * mm, "radius": 2 * mm});
            skCircle(sketch, "E4.18.6.0", {"center": v(182.66, -106.1) * mm, "radius": 2 * mm});
            skCircle(sketch, "E4.18.7.0", {"center": v(182.66, -122.1) * mm, "radius": 2 * mm});
            skCircle(sketch, "E4.18.8.0", {"center": v(182.66, -138.1) * mm, "radius": 2 * mm});
            skCircle(sketch, "E4.18.9.0", {"center": v(182.66, -154.1) * mm, "radius": 2 * mm});
            skCircle(sketch, "E4.18.10.0", {"center": v(182.66, -170.1) * mm, "radius": 2 * mm});
            skCircle(sketch, "E4.18.11.0", {"center": v(182.66, -186.1) * mm, "radius": 2 * mm});
            skCircle(sketch, "E4.18.12.0", {"center": v(182.66, -202.1) * mm, "radius": 2 * mm});
            skCircle(sketch, "E4.18.13.0", {"center": v(182.66, -218.1) * mm, "radius": 2 * mm});
            skCircle(sketch, "E4.18.14.0", {"center": v(182.66, -234.1) * mm, "radius": 2 * mm});
            skCircle(sketch, "E4.18.15.0", {"center": v(182.66, -250.1) * mm, "radius": 2 * mm});
            skCircle(sketch, "E4.18.16.0", {"center": v(182.66, -266.1) * mm, "radius": 2 * mm});
            skCircle(sketch, "E4.18.17.0", {"center": v(182.66, -282.1) * mm, "radius": 2 * mm});
            skCircle(sketch, "E4.18.18.0", {"center": v(182.66, -298.1) * mm, "radius": 2 * mm});
            skCircle(sketch, "E4.18.19.0", {"center": v(182.66, -314.1) * mm, "radius": 2 * mm});
            skCircle(sketch, "E4.18.20.0", {"center": v(182.66, -330.1) * mm, "radius": 2 * mm});
            skCircle(sketch, "E4.18.21.0", {"center": v(182.66, -346.1) * mm, "radius": 2 * mm});
            skCircle(sketch, "E4.18.22.0", {"center": v(182.66, -362.1) * mm, "radius": 2 * mm});
            skCircle(sketch, "E4.18.23.0", {"center": v(182.66, -378.1) * mm, "radius": 2 * mm});
            skCircle(sketch, "E4.18.24.0", {"center": v(182.66, -394.1) * mm, "radius": 2 * mm});
            skCircle(sketch, "E4.19.0.0", {"center": v(198.66, -10.1) * mm, "radius": 2 * mm});
            skCircle(sketch, "E4.19.1.0", {"center": v(198.66, -26.1) * mm, "radius": 2 * mm});
            skCircle(sketch, "E4.19.2.0", {"center": v(198.66, -42.1) * mm, "radius": 2 * mm});
            skCircle(sketch, "E4.19.3.0", {"center": v(198.66, -58.1) * mm, "radius": 2 * mm});
            skCircle(sketch, "E4.19.4.0", {"center": v(198.66, -74.1) * mm, "radius": 2 * mm});
            skCircle(sketch, "E4.19.5.0", {"center": v(198.66, -90.1) * mm, "radius": 2 * mm});
            skCircle(sketch, "E4.19.6.0", {"center": v(198.66, -106.1) * mm, "radius": 2 * mm});
            skCircle(sketch, "E4.19.7.0", {"center": v(198.66, -122.1) * mm, "radius": 2 * mm});
            skCircle(sketch, "E4.19.8.0", {"center": v(198.66, -138.1) * mm, "radius": 2 * mm});
            skCircle(sketch, "E4.19.9.0", {"center": v(198.66, -154.1) * mm, "radius": 2 * mm});
            skCircle(sketch, "E4.19.10.0", {"center": v(198.66, -170.1) * mm, "radius": 2 * mm});
            skCircle(sketch, "E4.19.11.0", {"center": v(198.66, -186.1) * mm, "radius": 2 * mm});
            skCircle(sketch, "E4.19.12.0", {"center": v(198.66, -202.1) * mm, "radius": 2 * mm});
            skCircle(sketch, "E4.19.13.0", {"center": v(198.66, -218.1) * mm, "radius": 2 * mm});
            skCircle(sketch, "E4.19.14.0", {"center": v(198.66, -234.1) * mm, "radius": 2 * mm});
            skCircle(sketch, "E4.19.15.0", {"center": v(198.66, -250.1) * mm, "radius": 2 * mm});
            skCircle(sketch, "E4.19.16.0", {"center": v(198.66, -266.1) * mm, "radius": 2 * mm});
            skCircle(sketch, "E4.19.17.0", {"center": v(198.66, -282.1) * mm, "radius": 2 * mm});
            skCircle(sketch, "E4.19.18.0", {"center": v(198.66, -298.1) * mm, "radius": 2 * mm});
            skCircle(sketch, "E4.19.19.0", {"center": v(198.66, -314.1) * mm, "radius": 2 * mm});
            skCircle(sketch, "E4.19.20.0", {"center": v(198.66, -330.1) * mm, "radius": 2 * mm});
            skCircle(sketch, "E4.19.21.0", {"center": v(198.66, -346.1) * mm, "radius": 2 * mm});
            skCircle(sketch, "E4.19.22.0", {"center": v(198.66, -362.1) * mm, "radius": 2 * mm});
            skCircle(sketch, "E4.19.23.0", {"center": v(198.66, -378.1) * mm, "radius": 2 * mm});
            skCircle(sketch, "E4.19.24.0", {"center": v(198.66, -394.1) * mm, "radius": 2 * mm});
            skCircle(sketch, "E4.20.0.0", {"center": v(214.66, -10.1) * mm, "radius": 2 * mm});
            skCircle(sketch, "E4.20.1.0", {"center": v(214.66, -26.1) * mm, "radius": 2 * mm});
            skCircle(sketch, "E4.20.2.0", {"center": v(214.66, -42.1) * mm, "radius": 2 * mm});
            skCircle(sketch, "E4.20.3.0", {"center": v(214.66, -58.1) * mm, "radius": 2 * mm});
            skCircle(sketch, "E4.20.4.0", {"center": v(214.66, -74.1) * mm, "radius": 2 * mm});
            skCircle(sketch, "E4.20.5.0", {"center": v(214.66, -90.1) * mm, "radius": 2 * mm});
            skCircle(sketch, "E4.20.6.0", {"center": v(214.66, -106.1) * mm, "radius": 2 * mm});
            skCircle(sketch, "E4.20.7.0", {"center": v(214.66, -122.1) * mm, "radius": 2 * mm});
            skCircle(sketch, "E4.20.8.0", {"center": v(214.66, -138.1) * mm, "radius": 2 * mm});
            skCircle(sketch, "E4.20.9.0", {"center": v(214.66, -154.1) * mm, "radius": 2 * mm});
            skCircle(sketch, "E4.20.10.0", {"center": v(214.66, -170.1) * mm, "radius": 2 * mm});
            skCircle(sketch, "E4.20.11.0", {"center": v(214.66, -186.1) * mm, "radius": 2 * mm});
            skCircle(sketch, "E4.20.12.0", {"center": v(214.66, -202.1) * mm, "radius": 2 * mm});
            skCircle(sketch, "E4.20.13.0", {"center": v(214.66, -218.1) * mm, "radius": 2 * mm});
            skCircle(sketch, "E4.20.14.0", {"center": v(214.66, -234.1) * mm, "radius": 2 * mm});
            skCircle(sketch, "E4.20.15.0", {"center": v(214.66, -250.1) * mm, "radius": 2 * mm});
            skCircle(sketch, "E4.20.16.0", {"center": v(214.66, -266.1) * mm, "radius": 2 * mm});
            skCircle(sketch, "E4.20.17.0", {"center": v(214.66, -282.1) * mm, "radius": 2 * mm});
            skCircle(sketch, "E4.20.18.0", {"center": v(214.66, -298.1) * mm, "radius": 2 * mm});
            skCircle(sketch, "E4.20.19.0", {"center": v(214.66, -314.1) * mm, "radius": 2 * mm});
            skCircle(sketch, "E4.20.20.0", {"center": v(214.66, -330.1) * mm, "radius": 2 * mm});
            skCircle(sketch, "E4.20.21.0", {"center": v(214.66, -346.1) * mm, "radius": 2 * mm});
            skCircle(sketch, "E4.20.22.0", {"center": v(214.66, -362.1) * mm, "radius": 2 * mm});
            skCircle(sketch, "E4.20.23.0", {"center": v(214.66, -378.1) * mm, "radius": 2 * mm});
            skCircle(sketch, "E4.20.24.0", {"center": v(214.66, -394.1) * mm, "radius": 2 * mm});
            skCircle(sketch, "E4.21.0.0", {"center": v(230.66, -10.1) * mm, "radius": 2 * mm});
            skCircle(sketch, "E4.21.1.0", {"center": v(230.66, -26.1) * mm, "radius": 2 * mm});
            skCircle(sketch, "E4.21.2.0", {"center": v(230.66, -42.1) * mm, "radius": 2 * mm});
            skCircle(sketch, "E4.21.3.0", {"center": v(230.66, -58.1) * mm, "radius": 2 * mm});
            skCircle(sketch, "E4.21.4.0", {"center": v(230.66, -74.1) * mm, "radius": 2 * mm});
            skCircle(sketch, "E4.21.5.0", {"center": v(230.66, -90.1) * mm, "radius": 2 * mm});
            skCircle(sketch, "E4.21.6.0", {"center": v(230.66, -106.1) * mm, "radius": 2 * mm});
            skCircle(sketch, "E4.21.7.0", {"center": v(230.66, -122.1) * mm, "radius": 2 * mm});
            skCircle(sketch, "E4.21.8.0", {"center": v(230.66, -138.1) * mm, "radius": 2 * mm});
            skCircle(sketch, "E4.21.9.0", {"center": v(230.66, -154.1) * mm, "radius": 2 * mm});
            skCircle(sketch, "E4.21.10.0", {"center": v(230.66, -170.1) * mm, "radius": 2 * mm});
            skCircle(sketch, "E4.21.11.0", {"center": v(230.66, -186.1) * mm, "radius": 2 * mm});
            skCircle(sketch, "E4.21.12.0", {"center": v(230.66, -202.1) * mm, "radius": 2 * mm});
            skCircle(sketch, "E4.21.13.0", {"center": v(230.66, -218.1) * mm, "radius": 2 * mm});
            skCircle(sketch, "E4.21.14.0", {"center": v(230.66, -234.1) * mm, "radius": 2 * mm});
            skCircle(sketch, "E4.21.15.0", {"center": v(230.66, -250.1) * mm, "radius": 2 * mm});
            skCircle(sketch, "E4.21.16.0", {"center": v(230.66, -266.1) * mm, "radius": 2 * mm});
            skCircle(sketch, "E4.21.17.0", {"center": v(230.66, -282.1) * mm, "radius": 2 * mm});
            skCircle(sketch, "E4.21.18.0", {"center": v(230.66, -298.1) * mm, "radius": 2 * mm});
            skCircle(sketch, "E4.21.19.0", {"center": v(230.66, -314.1) * mm, "radius": 2 * mm});
            skCircle(sketch, "E4.21.20.0", {"center": v(230.66, -330.1) * mm, "radius": 2 * mm});
            skCircle(sketch, "E4.21.21.0", {"center": v(230.66, -346.1) * mm, "radius": 2 * mm});
            skCircle(sketch, "E4.21.22.0", {"center": v(230.66, -362.1) * mm, "radius": 2 * mm});
            skCircle(sketch, "E4.21.23.0", {"center": v(230.66, -378.1) * mm, "radius": 2 * mm});
            skCircle(sketch, "E4.21.24.0", {"center": v(230.66, -394.1) * mm, "radius": 2 * mm});
            skCircle(sketch, "E4.22.0.0", {"center": v(246.66, -10.1) * mm, "radius": 2 * mm});
            skCircle(sketch, "E4.22.1.0", {"center": v(246.66, -26.1) * mm, "radius": 2 * mm});
            skCircle(sketch, "E4.22.2.0", {"center": v(246.66, -42.1) * mm, "radius": 2 * mm});
            skCircle(sketch, "E4.22.3.0", {"center": v(246.66, -58.1) * mm, "radius": 2 * mm});
            skCircle(sketch, "E4.22.4.0", {"center": v(246.66, -74.1) * mm, "radius": 2 * mm});
            skCircle(sketch, "E4.22.5.0", {"center": v(246.66, -90.1) * mm, "radius": 2 * mm});
            skCircle(sketch, "E4.22.6.0", {"center": v(246.66, -106.1) * mm, "radius": 2 * mm});
            skCircle(sketch, "E4.22.7.0", {"center": v(246.66, -122.1) * mm, "radius": 2 * mm});
            skCircle(sketch, "E4.22.8.0", {"center": v(246.66, -138.1) * mm, "radius": 2 * mm});
            skCircle(sketch, "E4.22.9.0", {"center": v(246.66, -154.1) * mm, "radius": 2 * mm});
            skCircle(sketch, "E4.22.10.0", {"center": v(246.66, -170.1) * mm, "radius": 2 * mm});
            skCircle(sketch, "E4.22.11.0", {"center": v(246.66, -186.1) * mm, "radius": 2 * mm});
            skCircle(sketch, "E4.22.12.0", {"center": v(246.66, -202.1) * mm, "radius": 2 * mm});
            skCircle(sketch, "E4.22.13.0", {"center": v(246.66, -218.1) * mm, "radius": 2 * mm});
            skCircle(sketch, "E4.22.14.0", {"center": v(246.66, -234.1) * mm, "radius": 2 * mm});
            skCircle(sketch, "E4.22.15.0", {"center": v(246.66, -250.1) * mm, "radius": 2 * mm});
            skCircle(sketch, "E4.22.16.0", {"center": v(246.66, -266.1) * mm, "radius": 2 * mm});
            skCircle(sketch, "E4.22.17.0", {"center": v(246.66, -282.1) * mm, "radius": 2 * mm});
            skCircle(sketch, "E4.22.18.0", {"center": v(246.66, -298.1) * mm, "radius": 2 * mm});
            skCircle(sketch, "E4.22.19.0", {"center": v(246.66, -314.1) * mm, "radius": 2 * mm});
            skCircle(sketch, "E4.22.20.0", {"center": v(246.66, -330.1) * mm, "radius": 2 * mm});
            skCircle(sketch, "E4.22.21.0", {"center": v(246.66, -346.1) * mm, "radius": 2 * mm});
            skCircle(sketch, "E4.22.22.0", {"center": v(246.66, -362.1) * mm, "radius": 2 * mm});
            skCircle(sketch, "E4.22.23.0", {"center": v(246.66, -378.1) * mm, "radius": 2 * mm});
            skCircle(sketch, "E4.22.24.0", {"center": v(246.66, -394.1) * mm, "radius": 2 * mm});
            skCircle(sketch, "E4.23.0.0", {"center": v(262.66, -10.1) * mm, "radius": 2 * mm});
            skCircle(sketch, "E4.23.1.0", {"center": v(262.66, -26.1) * mm, "radius": 2 * mm});
            skCircle(sketch, "E4.23.2.0", {"center": v(262.66, -42.1) * mm, "radius": 2 * mm});
            skCircle(sketch, "E4.23.3.0", {"center": v(262.66, -58.1) * mm, "radius": 2 * mm});
            skCircle(sketch, "E4.23.4.0", {"center": v(262.66, -74.1) * mm, "radius": 2 * mm});
            skCircle(sketch, "E4.23.5.0", {"center": v(262.66, -90.1) * mm, "radius": 2 * mm});
            skCircle(sketch, "E4.23.6.0", {"center": v(262.66, -106.1) * mm, "radius": 2 * mm});
            skCircle(sketch, "E4.23.7.0", {"center": v(262.66, -122.1) * mm, "radius": 2 * mm});
            skCircle(sketch, "E4.23.8.0", {"center": v(262.66, -138.1) * mm, "radius": 2 * mm});
            skCircle(sketch, "E4.23.9.0", {"center": v(262.66, -154.1) * mm, "radius": 2 * mm});
            skCircle(sketch, "E4.23.10.0", {"center": v(262.66, -170.1) * mm, "radius": 2 * mm});
            skCircle(sketch, "E4.23.11.0", {"center": v(262.66, -186.1) * mm, "radius": 2 * mm});
            skCircle(sketch, "E4.23.12.0", {"center": v(262.66, -202.1) * mm, "radius": 2 * mm});
            skCircle(sketch, "E4.23.13.0", {"center": v(262.66, -218.1) * mm, "radius": 2 * mm});
            skCircle(sketch, "E4.23.14.0", {"center": v(262.66, -234.1) * mm, "radius": 2 * mm});
            skCircle(sketch, "E4.23.15.0", {"center": v(262.66, -250.1) * mm, "radius": 2 * mm});
            skCircle(sketch, "E4.23.16.0", {"center": v(262.66, -266.1) * mm, "radius": 2 * mm});
            skCircle(sketch, "E4.23.17.0", {"center": v(262.66, -282.1) * mm, "radius": 2 * mm});
            skCircle(sketch, "E4.23.18.0", {"center": v(262.66, -298.1) * mm, "radius": 2 * mm});
            skCircle(sketch, "E4.23.19.0", {"center": v(262.66, -314.1) * mm, "radius": 2 * mm});
            skCircle(sketch, "E4.23.20.0", {"center": v(262.66, -330.1) * mm, "radius": 2 * mm});
            skCircle(sketch, "E4.23.21.0", {"center": v(262.66, -346.1) * mm, "radius": 2 * mm});
            skCircle(sketch, "E4.23.22.0", {"center": v(262.66, -362.1) * mm, "radius": 2 * mm});
            skCircle(sketch, "E4.23.23.0", {"center": v(262.66, -378.1) * mm, "radius": 2 * mm});
            skCircle(sketch, "E4.23.24.0", {"center": v(262.66, -394.1) * mm, "radius": 2 * mm});
            skCircle(sketch, "E4.24.0.0", {"center": v(278.66, -10.1) * mm, "radius": 2 * mm});
            skCircle(sketch, "E4.24.1.0", {"center": v(278.66, -26.1) * mm, "radius": 2 * mm});
            skCircle(sketch, "E4.24.2.0", {"center": v(278.66, -42.1) * mm, "radius": 2 * mm});
            skCircle(sketch, "E4.24.3.0", {"center": v(278.66, -58.1) * mm, "radius": 2 * mm});
            skCircle(sketch, "E4.24.4.0", {"center": v(278.66, -74.1) * mm, "radius": 2 * mm});
            skCircle(sketch, "E4.24.5.0", {"center": v(278.66, -90.1) * mm, "radius": 2 * mm});
            skCircle(sketch, "E4.24.6.0", {"center": v(278.66, -106.1) * mm, "radius": 2 * mm});
            skCircle(sketch, "E4.24.7.0", {"center": v(278.66, -122.1) * mm, "radius": 2 * mm});
            skCircle(sketch, "E4.24.8.0", {"center": v(278.66, -138.1) * mm, "radius": 2 * mm});
            skCircle(sketch, "E4.24.9.0", {"center": v(278.66, -154.1) * mm, "radius": 2 * mm});
            skCircle(sketch, "E4.24.10.0", {"center": v(278.66, -170.1) * mm, "radius": 2 * mm});
            skCircle(sketch, "E4.24.11.0", {"center": v(278.66, -186.1) * mm, "radius": 2 * mm});
            skCircle(sketch, "E4.24.12.0", {"center": v(278.66, -202.1) * mm, "radius": 2 * mm});
            skCircle(sketch, "E4.24.13.0", {"center": v(278.66, -218.1) * mm, "radius": 2 * mm});
            skCircle(sketch, "E4.24.14.0", {"center": v(278.66, -234.1) * mm, "radius": 2 * mm});
            skCircle(sketch, "E4.24.15.0", {"center": v(278.66, -250.1) * mm, "radius": 2 * mm});
            skCircle(sketch, "E4.24.16.0", {"center": v(278.66, -266.1) * mm, "radius": 2 * mm});
            skCircle(sketch, "E4.24.17.0", {"center": v(278.66, -282.1) * mm, "radius": 2 * mm});
            skCircle(sketch, "E4.24.18.0", {"center": v(278.66, -298.1) * mm, "radius": 2 * mm});
            skCircle(sketch, "E4.24.19.0", {"center": v(278.66, -314.1) * mm, "radius": 2 * mm});
            skCircle(sketch, "E4.24.20.0", {"center": v(278.66, -330.1) * mm, "radius": 2 * mm});
            skCircle(sketch, "E4.24.21.0", {"center": v(278.66, -346.1) * mm, "radius": 2 * mm});
            skCircle(sketch, "E4.24.22.0", {"center": v(278.66, -362.1) * mm, "radius": 2 * mm});
            skCircle(sketch, "E4.24.23.0", {"center": v(278.66, -378.1) * mm, "radius": 2 * mm});
            skCircle(sketch, "E4.24.24.0", {"center": v(278.66, -394.1) * mm, "radius": 2 * mm});
            skCircle(sketch, "E4.25.0.0", {"center": v(294.66, -10.1) * mm, "radius": 2 * mm});
            skCircle(sketch, "E4.25.1.0", {"center": v(294.66, -26.1) * mm, "radius": 2 * mm});
            skCircle(sketch, "E4.25.2.0", {"center": v(294.66, -42.1) * mm, "radius": 2 * mm});
            skCircle(sketch, "E4.25.3.0", {"center": v(294.66, -58.1) * mm, "radius": 2 * mm});
            skCircle(sketch, "E4.25.4.0", {"center": v(294.66, -74.1) * mm, "radius": 2 * mm});
            skCircle(sketch, "E4.25.5.0", {"center": v(294.66, -90.1) * mm, "radius": 2 * mm});
            skCircle(sketch, "E4.25.6.0", {"center": v(294.66, -106.1) * mm, "radius": 2 * mm});
            skCircle(sketch, "E4.25.7.0", {"center": v(294.66, -122.1) * mm, "radius": 2 * mm});
            skCircle(sketch, "E4.25.8.0", {"center": v(294.66, -138.1) * mm, "radius": 2 * mm});
            skCircle(sketch, "E4.25.9.0", {"center": v(294.66, -154.1) * mm, "radius": 2 * mm});
            skCircle(sketch, "E4.25.10.0", {"center": v(294.66, -170.1) * mm, "radius": 2 * mm});
            skCircle(sketch, "E4.25.11.0", {"center": v(294.66, -186.1) * mm, "radius": 2 * mm});
            skCircle(sketch, "E4.25.12.0", {"center": v(294.66, -202.1) * mm, "radius": 2 * mm});
            skCircle(sketch, "E4.25.13.0", {"center": v(294.66, -218.1) * mm, "radius": 2 * mm});
            skCircle(sketch, "E4.25.14.0", {"center": v(294.66, -234.1) * mm, "radius": 2 * mm});
            skCircle(sketch, "E4.25.15.0", {"center": v(294.66, -250.1) * mm, "radius": 2 * mm});
            skCircle(sketch, "E4.25.16.0", {"center": v(294.66, -266.1) * mm, "radius": 2 * mm});
            skCircle(sketch, "E4.25.17.0", {"center": v(294.66, -282.1) * mm, "radius": 2 * mm});
            skCircle(sketch, "E4.25.18.0", {"center": v(294.66, -298.1) * mm, "radius": 2 * mm});
            skCircle(sketch, "E4.25.19.0", {"center": v(294.66, -314.1) * mm, "radius": 2 * mm});
            skCircle(sketch, "E4.25.20.0", {"center": v(294.66, -330.1) * mm, "radius": 2 * mm});
            skCircle(sketch, "E4.25.21.0", {"center": v(294.66, -346.1) * mm, "radius": 2 * mm});
            skCircle(sketch, "E4.25.22.0", {"center": v(294.66, -362.1) * mm, "radius": 2 * mm});
            skCircle(sketch, "E4.25.23.0", {"center": v(294.66, -378.1) * mm, "radius": 2 * mm});
            skCircle(sketch, "E4.25.24.0", {"center": v(294.66, -394.1) * mm, "radius": 2 * mm});
            skCircle(sketch, "E4.26.0.0", {"center": v(310.66, -10.1) * mm, "radius": 2 * mm});
            skCircle(sketch, "E4.26.1.0", {"center": v(310.66, -26.1) * mm, "radius": 2 * mm});
            skCircle(sketch, "E4.26.2.0", {"center": v(310.66, -42.1) * mm, "radius": 2 * mm});
            skCircle(sketch, "E4.26.3.0", {"center": v(310.66, -58.1) * mm, "radius": 2 * mm});
            skCircle(sketch, "E4.26.4.0", {"center": v(310.66, -74.1) * mm, "radius": 2 * mm});
            skCircle(sketch, "E4.26.5.0", {"center": v(310.66, -90.1) * mm, "radius": 2 * mm});
            skCircle(sketch, "E4.26.6.0", {"center": v(310.66, -106.1) * mm, "radius": 2 * mm});
            skCircle(sketch, "E4.26.7.0", {"center": v(310.66, -122.1) * mm, "radius": 2 * mm});
            skCircle(sketch, "E4.26.8.0", {"center": v(310.66, -138.1) * mm, "radius": 2 * mm});
            skCircle(sketch, "E4.26.9.0", {"center": v(310.66, -154.1) * mm, "radius": 2 * mm});
            skCircle(sketch, "E4.26.10.0", {"center": v(310.66, -170.1) * mm, "radius": 2 * mm});
            skCircle(sketch, "E4.26.11.0", {"center": v(310.66, -186.1) * mm, "radius": 2 * mm});
            skCircle(sketch, "E4.26.12.0", {"center": v(310.66, -202.1) * mm, "radius": 2 * mm});
            skCircle(sketch, "E4.26.13.0", {"center": v(310.66, -218.1) * mm, "radius": 2 * mm});
            skCircle(sketch, "E4.26.14.0", {"center": v(310.66, -234.1) * mm, "radius": 2 * mm});
            skCircle(sketch, "E4.26.15.0", {"center": v(310.66, -250.1) * mm, "radius": 2 * mm});
            skCircle(sketch, "E4.26.16.0", {"center": v(310.66, -266.1) * mm, "radius": 2 * mm});
            skCircle(sketch, "E4.26.17.0", {"center": v(310.66, -282.1) * mm, "radius": 2 * mm});
            skCircle(sketch, "E4.26.18.0", {"center": v(310.66, -298.1) * mm, "radius": 2 * mm});
            skCircle(sketch, "E4.26.19.0", {"center": v(310.66, -314.1) * mm, "radius": 2 * mm});
            skCircle(sketch, "E4.26.20.0", {"center": v(310.66, -330.1) * mm, "radius": 2 * mm});
            skCircle(sketch, "E4.26.21.0", {"center": v(310.66, -346.1) * mm, "radius": 2 * mm});
            skCircle(sketch, "E4.26.22.0", {"center": v(310.66, -362.1) * mm, "radius": 2 * mm});
            skCircle(sketch, "E4.26.23.0", {"center": v(310.66, -378.1) * mm, "radius": 2 * mm});
            skCircle(sketch, "E4.26.24.0", {"center": v(310.66, -394.1) * mm, "radius": 2 * mm});
            skCircle(sketch, "E4.27.0.0", {"center": v(326.66, -10.1) * mm, "radius": 2 * mm});
            skCircle(sketch, "E4.27.1.0", {"center": v(326.66, -26.1) * mm, "radius": 2 * mm});
            skCircle(sketch, "E4.27.2.0", {"center": v(326.66, -42.1) * mm, "radius": 2 * mm});
            skCircle(sketch, "E4.27.3.0", {"center": v(326.66, -58.1) * mm, "radius": 2 * mm});
            skCircle(sketch, "E4.27.4.0", {"center": v(326.66, -74.1) * mm, "radius": 2 * mm});
            skCircle(sketch, "E4.27.5.0", {"center": v(326.66, -90.1) * mm, "radius": 2 * mm});
            skCircle(sketch, "E4.27.6.0", {"center": v(326.66, -106.1) * mm, "radius": 2 * mm});
            skCircle(sketch, "E4.27.7.0", {"center": v(326.66, -122.1) * mm, "radius": 2 * mm});
            skCircle(sketch, "E4.27.8.0", {"center": v(326.66, -138.1) * mm, "radius": 2 * mm});
            skCircle(sketch, "E4.27.9.0", {"center": v(326.66, -154.1) * mm, "radius": 2 * mm});
            skCircle(sketch, "E4.27.10.0", {"center": v(326.66, -170.1) * mm, "radius": 2 * mm});
            skCircle(sketch, "E4.27.11.0", {"center": v(326.66, -186.1) * mm, "radius": 2 * mm});
            skCircle(sketch, "E4.27.12.0", {"center": v(326.66, -202.1) * mm, "radius": 2 * mm});
            skCircle(sketch, "E4.27.13.0", {"center": v(326.66, -218.1) * mm, "radius": 2 * mm});
            skCircle(sketch, "E4.27.14.0", {"center": v(326.66, -234.1) * mm, "radius": 2 * mm});
            skCircle(sketch, "E4.27.15.0", {"center": v(326.66, -250.1) * mm, "radius": 2 * mm});
            skCircle(sketch, "E4.27.16.0", {"center": v(326.66, -266.1) * mm, "radius": 2 * mm});
            skCircle(sketch, "E4.27.17.0", {"center": v(326.66, -282.1) * mm, "radius": 2 * mm});
            skCircle(sketch, "E4.27.18.0", {"center": v(326.66, -298.1) * mm, "radius": 2 * mm});
            skCircle(sketch, "E4.27.19.0", {"center": v(326.66, -314.1) * mm, "radius": 2 * mm});
            skCircle(sketch, "E4.27.20.0", {"center": v(326.66, -330.1) * mm, "radius": 2 * mm});
            skCircle(sketch, "E4.27.21.0", {"center": v(326.66, -346.1) * mm, "radius": 2 * mm});
            skCircle(sketch, "E4.27.22.0", {"center": v(326.66, -362.1) * mm, "radius": 2 * mm});
            skCircle(sketch, "E4.27.23.0", {"center": v(326.66, -378.1) * mm, "radius": 2 * mm});
            skCircle(sketch, "E4.27.24.0", {"center": v(326.66, -394.1) * mm, "radius": 2 * mm});
            skCircle(sketch, "E4.28.0.0", {"center": v(342.66, -10.1) * mm, "radius": 2 * mm});
            skCircle(sketch, "E4.28.1.0", {"center": v(342.66, -26.1) * mm, "radius": 2 * mm});
            skCircle(sketch, "E4.28.2.0", {"center": v(342.66, -42.1) * mm, "radius": 2 * mm});
            skCircle(sketch, "E4.28.3.0", {"center": v(342.66, -58.1) * mm, "radius": 2 * mm});
            skCircle(sketch, "E4.28.4.0", {"center": v(342.66, -74.1) * mm, "radius": 2 * mm});
            skCircle(sketch, "E4.28.5.0", {"center": v(342.66, -90.1) * mm, "radius": 2 * mm});
            skCircle(sketch, "E4.28.6.0", {"center": v(342.66, -106.1) * mm, "radius": 2 * mm});
            skCircle(sketch, "E4.28.7.0", {"center": v(342.66, -122.1) * mm, "radius": 2 * mm});
            skCircle(sketch, "E4.28.8.0", {"center": v(342.66, -138.1) * mm, "radius": 2 * mm});
            skCircle(sketch, "E4.28.9.0", {"center": v(342.66, -154.1) * mm, "radius": 2 * mm});
            skCircle(sketch, "E4.28.10.0", {"center": v(342.66, -170.1) * mm, "radius": 2 * mm});
            skCircle(sketch, "E4.28.11.0", {"center": v(342.66, -186.1) * mm, "radius": 2 * mm});
            skCircle(sketch, "E4.28.12.0", {"center": v(342.66, -202.1) * mm, "radius": 2 * mm});
            skCircle(sketch, "E4.28.13.0", {"center": v(342.66, -218.1) * mm, "radius": 2 * mm});
            skCircle(sketch, "E4.28.14.0", {"center": v(342.66, -234.1) * mm, "radius": 2 * mm});
            skCircle(sketch, "E4.28.15.0", {"center": v(342.66, -250.1) * mm, "radius": 2 * mm});
            skCircle(sketch, "E4.28.16.0", {"center": v(342.66, -266.1) * mm, "radius": 2 * mm});
            skCircle(sketch, "E4.28.17.0", {"center": v(342.66, -282.1) * mm, "radius": 2 * mm});
            skCircle(sketch, "E4.28.18.0", {"center": v(342.66, -298.1) * mm, "radius": 2 * mm});
            skCircle(sketch, "E4.28.19.0", {"center": v(342.66, -314.1) * mm, "radius": 2 * mm});
            skCircle(sketch, "E4.28.20.0", {"center": v(342.66, -330.1) * mm, "radius": 2 * mm});
            skCircle(sketch, "E4.28.21.0", {"center": v(342.66, -346.1) * mm, "radius": 2 * mm});
            skCircle(sketch, "E4.28.22.0", {"center": v(342.66, -362.1) * mm, "radius": 2 * mm});
            skCircle(sketch, "E4.28.23.0", {"center": v(342.66, -378.1) * mm, "radius": 2 * mm});
            skCircle(sketch, "E4.28.24.0", {"center": v(342.66, -394.1) * mm, "radius": 2 * mm});
            skCircle(sketch, "E4.29.0.0", {"center": v(358.66, -10.1) * mm, "radius": 2 * mm});
            skCircle(sketch, "E4.29.1.0", {"center": v(358.66, -26.1) * mm, "radius": 2 * mm});
            skCircle(sketch, "E4.29.2.0", {"center": v(358.66, -42.1) * mm, "radius": 2 * mm});
            skCircle(sketch, "E4.29.3.0", {"center": v(358.66, -58.1) * mm, "radius": 2 * mm});
            skCircle(sketch, "E4.29.4.0", {"center": v(358.66, -74.1) * mm, "radius": 2 * mm});
            skCircle(sketch, "E4.29.5.0", {"center": v(358.66, -90.1) * mm, "radius": 2 * mm});
            skCircle(sketch, "E4.29.6.0", {"center": v(358.66, -106.1) * mm, "radius": 2 * mm});
            skCircle(sketch, "E4.29.7.0", {"center": v(358.66, -122.1) * mm, "radius": 2 * mm});
            skCircle(sketch, "E4.29.8.0", {"center": v(358.66, -138.1) * mm, "radius": 2 * mm});
            skCircle(sketch, "E4.29.9.0", {"center": v(358.66, -154.1) * mm, "radius": 2 * mm});
            skCircle(sketch, "E4.29.10.0", {"center": v(358.66, -170.1) * mm, "radius": 2 * mm});
            skCircle(sketch, "E4.29.11.0", {"center": v(358.66, -186.1) * mm, "radius": 2 * mm});
            skCircle(sketch, "E4.29.12.0", {"center": v(358.66, -202.1) * mm, "radius": 2 * mm});
            skCircle(sketch, "E4.29.13.0", {"center": v(358.66, -218.1) * mm, "radius": 2 * mm});
            skCircle(sketch, "E4.29.14.0", {"center": v(358.66, -234.1) * mm, "radius": 2 * mm});
            skCircle(sketch, "E4.29.15.0", {"center": v(358.66, -250.1) * mm, "radius": 2 * mm});
            skCircle(sketch, "E4.29.16.0", {"center": v(358.66, -266.1) * mm, "radius": 2 * mm});
            skCircle(sketch, "E4.29.17.0", {"center": v(358.66, -282.1) * mm, "radius": 2 * mm});
            skCircle(sketch, "E4.29.18.0", {"center": v(358.66, -298.1) * mm, "radius": 2 * mm});
            skCircle(sketch, "E4.29.19.0", {"center": v(358.66, -314.1) * mm, "radius": 2 * mm});
            skCircle(sketch, "E4.29.20.0", {"center": v(358.66, -330.1) * mm, "radius": 2 * mm});
            skCircle(sketch, "E4.29.21.0", {"center": v(358.66, -346.1) * mm, "radius": 2 * mm});
            skCircle(sketch, "E4.29.22.0", {"center": v(358.66, -362.1) * mm, "radius": 2 * mm});
            skCircle(sketch, "E4.29.23.0", {"center": v(358.66, -378.1) * mm, "radius": 2 * mm});
            skCircle(sketch, "E4.29.24.0", {"center": v(358.66, -394.1) * mm, "radius": 2 * mm});
            skCircle(sketch, "E4.30.0.0", {"center": v(374.66, -10.1) * mm, "radius": 2 * mm});
            skCircle(sketch, "E4.30.1.0", {"center": v(374.66, -26.1) * mm, "radius": 2 * mm});
            skCircle(sketch, "E4.30.2.0", {"center": v(374.66, -42.1) * mm, "radius": 2 * mm});
            skCircle(sketch, "E4.30.3.0", {"center": v(374.66, -58.1) * mm, "radius": 2 * mm});
            skCircle(sketch, "E4.30.4.0", {"center": v(374.66, -74.1) * mm, "radius": 2 * mm});
            skCircle(sketch, "E4.30.5.0", {"center": v(374.66, -90.1) * mm, "radius": 2 * mm});
            skCircle(sketch, "E4.30.6.0", {"center": v(374.66, -106.1) * mm, "radius": 2 * mm});
            skCircle(sketch, "E4.30.7.0", {"center": v(374.66, -122.1) * mm, "radius": 2 * mm});
            skCircle(sketch, "E4.30.8.0", {"center": v(374.66, -138.1) * mm, "radius": 2 * mm});
            skCircle(sketch, "E4.30.9.0", {"center": v(374.66, -154.1) * mm, "radius": 2 * mm});
            skCircle(sketch, "E4.30.10.0", {"center": v(374.66, -170.1) * mm, "radius": 2 * mm});
            skCircle(sketch, "E4.30.11.0", {"center": v(374.66, -186.1) * mm, "radius": 2 * mm});
            skCircle(sketch, "E4.30.12.0", {"center": v(374.66, -202.1) * mm, "radius": 2 * mm});
            skCircle(sketch, "E4.30.13.0", {"center": v(374.66, -218.1) * mm, "radius": 2 * mm});
            skCircle(sketch, "E4.30.14.0", {"center": v(374.66, -234.1) * mm, "radius": 2 * mm});
            skCircle(sketch, "E4.30.15.0", {"center": v(374.66, -250.1) * mm, "radius": 2 * mm});
            skCircle(sketch, "E4.30.16.0", {"center": v(374.66, -266.1) * mm, "radius": 2 * mm});
            skCircle(sketch, "E4.30.17.0", {"center": v(374.66, -282.1) * mm, "radius": 2 * mm});
            skCircle(sketch, "E4.30.18.0", {"center": v(374.66, -298.1) * mm, "radius": 2 * mm});
            skCircle(sketch, "E4.30.19.0", {"center": v(374.66, -314.1) * mm, "radius": 2 * mm});
            skCircle(sketch, "E4.30.20.0", {"center": v(374.66, -330.1) * mm, "radius": 2 * mm});
            skCircle(sketch, "E4.30.21.0", {"center": v(374.66, -346.1) * mm, "radius": 2 * mm});
            skCircle(sketch, "E4.30.22.0", {"center": v(374.66, -362.1) * mm, "radius": 2 * mm});
            skCircle(sketch, "E4.30.23.0", {"center": v(374.66, -378.1) * mm, "radius": 2 * mm});
            skCircle(sketch, "E4.30.24.0", {"center": v(374.66, -394.1) * mm, "radius": 2 * mm});
            skLineSegment(sketch, "E4.direction1", {"start": v(-105.34, -10.1) * mm, "end": v(-89.34, -10.1) * mm, "construction": true});
            skLineSegment(sketch, "E4.direction2", {"start": v(-105.34, -10.1) * mm, "end": v(-105.34, -26.1) * mm, "construction": true});
            skCircle(sketch, "E5.0.31.0", {"center": v(382.66, -2.1) * mm, "radius": 2 * mm});
            skCircle(sketch, "E5.0.31.1", {"center": v(382.66, -18.1) * mm, "radius": 2 * mm});
            skCircle(sketch, "E5.0.31.2", {"center": v(382.66, -34.1) * mm, "radius": 2 * mm});
            skCircle(sketch, "E5.0.31.3", {"center": v(382.66, -50.1) * mm, "radius": 2 * mm});
            skCircle(sketch, "E5.0.31.4", {"center": v(382.66, -66.1) * mm, "radius": 2 * mm});
            skCircle(sketch, "E5.0.31.5", {"center": v(382.66, -82.1) * mm, "radius": 2 * mm});
            skCircle(sketch, "E5.0.31.6", {"center": v(382.66, -98.1) * mm, "radius": 2 * mm});
            skCircle(sketch, "E5.0.31.7", {"center": v(382.66, -114.1) * mm, "radius": 2 * mm});
            skCircle(sketch, "E5.0.31.8", {"center": v(382.66, -130.1) * mm, "radius": 2 * mm});
            skCircle(sketch, "E5.0.31.9", {"center": v(382.66, -146.1) * mm, "radius": 2 * mm});
            skCircle(sketch, "E5.0.31.10", {"center": v(382.66, -162.1) * mm, "radius": 2 * mm});
            skCircle(sketch, "E5.0.31.11", {"center": v(382.66, -178.1) * mm, "radius": 2 * mm});
            skCircle(sketch, "E5.0.31.12", {"center": v(382.66, -194.1) * mm, "radius": 2 * mm});
            skCircle(sketch, "E5.0.31.13", {"center": v(382.66, -210.1) * mm, "radius": 2 * mm});
            skCircle(sketch, "E5.0.31.14", {"center": v(382.66, -226.1) * mm, "radius": 2 * mm});
            skCircle(sketch, "E5.0.31.15", {"center": v(382.66, -242.1) * mm, "radius": 2 * mm});
            skCircle(sketch, "E5.0.31.16", {"center": v(382.66, -258.1) * mm, "radius": 2 * mm});
            skCircle(sketch, "E5.0.31.17", {"center": v(382.66, -274.1) * mm, "radius": 2 * mm});
            skCircle(sketch, "E5.0.31.18", {"center": v(382.66, -290.1) * mm, "radius": 2 * mm});
            skCircle(sketch, "E5.0.31.19", {"center": v(382.66, -306.1) * mm, "radius": 2 * mm});
            skCircle(sketch, "E5.0.31.20", {"center": v(382.66, -322.1) * mm, "radius": 2 * mm});
            skCircle(sketch, "E5.0.31.21", {"center": v(382.66, -338.1) * mm, "radius": 2 * mm});
            skCircle(sketch, "E5.0.31.22", {"center": v(382.66, -354.1) * mm, "radius": 2 * mm});
            skCircle(sketch, "E5.0.31.23", {"center": v(382.66, -370.1) * mm, "radius": 2 * mm});
            skCircle(sketch, "E5.0.31.24", {"center": v(382.66, -386.1) * mm, "radius": 2 * mm});
            skCircle(sketch, "E6.0.31.0", {"center": v(390.66, -10.1) * mm, "radius": 2 * mm});
            skCircle(sketch, "E6.0.31.1", {"center": v(390.66, -26.1) * mm, "radius": 2 * mm});
            skCircle(sketch, "E6.0.31.2", {"center": v(390.66, -42.1) * mm, "radius": 2 * mm});
            skCircle(sketch, "E6.0.31.3", {"center": v(390.66, -58.1) * mm, "radius": 2 * mm});
            skCircle(sketch, "E6.0.31.4", {"center": v(390.66, -74.1) * mm, "radius": 2 * mm});
            skCircle(sketch, "E6.0.31.5", {"center": v(390.66, -90.1) * mm, "radius": 2 * mm});
            skCircle(sketch, "E6.0.31.6", {"center": v(390.66, -106.1) * mm, "radius": 2 * mm});
            skCircle(sketch, "E6.0.31.7", {"center": v(390.66, -122.1) * mm, "radius": 2 * mm});
            skCircle(sketch, "E6.0.31.8", {"center": v(390.66, -138.1) * mm, "radius": 2 * mm});
            skCircle(sketch, "E6.0.31.9", {"center": v(390.66, -154.1) * mm, "radius": 2 * mm});
            skCircle(sketch, "E6.0.31.10", {"center": v(390.66, -170.1) * mm, "radius": 2 * mm});
            skCircle(sketch, "E6.0.31.11", {"center": v(390.66, -186.1) * mm, "radius": 2 * mm});
            skCircle(sketch, "E6.0.31.12", {"center": v(390.66, -202.1) * mm, "radius": 2 * mm});
            skCircle(sketch, "E6.0.31.13", {"center": v(390.66, -218.1) * mm, "radius": 2 * mm});
            skCircle(sketch, "E6.0.31.14", {"center": v(390.66, -234.1) * mm, "radius": 2 * mm});
            skCircle(sketch, "E6.0.31.15", {"center": v(390.66, -250.1) * mm, "radius": 2 * mm});
            skCircle(sketch, "E6.0.31.16", {"center": v(390.66, -266.1) * mm, "radius": 2 * mm});
            skCircle(sketch, "E6.0.31.17", {"center": v(390.66, -282.1) * mm, "radius": 2 * mm});
            skCircle(sketch, "E6.0.31.18", {"center": v(390.66, -298.1) * mm, "radius": 2 * mm});
            skCircle(sketch, "E6.0.31.19", {"center": v(390.66, -314.1) * mm, "radius": 2 * mm});
            skCircle(sketch, "E6.0.31.20", {"center": v(390.66, -330.1) * mm, "radius": 2 * mm});
            skCircle(sketch, "E6.0.31.21", {"center": v(390.66, -346.1) * mm, "radius": 2 * mm});
            skCircle(sketch, "E6.0.31.22", {"center": v(390.66, -362.1) * mm, "radius": 2 * mm});
            skCircle(sketch, "E6.0.31.23", {"center": v(390.66, -378.1) * mm, "radius": 2 * mm});
            skCircle(sketch, "E6.0.31.24", {"center": v(390.66, -394.1) * mm, "radius": 2 * mm});
            skCircle(sketch, "E7.0.0.25", {"center": v(-113.34, -402.1) * mm, "radius": 2 * mm});
            skCircle(sketch, "E7.0.1.25", {"center": v(-97.34, -402.1) * mm, "radius": 2 * mm});
            skCircle(sketch, "E7.0.2.25", {"center": v(-81.34, -402.1) * mm, "radius": 2 * mm});
            skCircle(sketch, "E7.0.3.25", {"center": v(-65.34, -402.1) * mm, "radius": 2 * mm});
            skCircle(sketch, "E7.0.4.25", {"center": v(-49.34, -402.1) * mm, "radius": 2 * mm});
            skCircle(sketch, "E7.0.5.25", {"center": v(-33.34, -402.1) * mm, "radius": 2 * mm});
            skCircle(sketch, "E7.0.6.25", {"center": v(-17.34, -402.1) * mm, "radius": 2 * mm});
            skCircle(sketch, "E7.0.7.25", {"center": v(-1.34, -402.1) * mm, "radius": 2 * mm});
            skCircle(sketch, "E7.0.8.25", {"center": v(14.66, -402.1) * mm, "radius": 2 * mm});
            skCircle(sketch, "E7.0.9.25", {"center": v(30.66, -402.1) * mm, "radius": 2 * mm});
            skCircle(sketch, "E7.0.10.25", {"center": v(46.66, -402.1) * mm, "radius": 2 * mm});
            skCircle(sketch, "E7.0.11.25", {"center": v(62.66, -402.1) * mm, "radius": 2 * mm});
            skCircle(sketch, "E7.0.12.25", {"center": v(78.66, -402.1) * mm, "radius": 2 * mm});
            skCircle(sketch, "E7.0.13.25", {"center": v(94.66, -402.1) * mm, "radius": 2 * mm});
            skCircle(sketch, "E7.0.14.25", {"center": v(110.66, -402.1) * mm, "radius": 2 * mm});
            skCircle(sketch, "E7.0.15.25", {"center": v(126.66, -402.1) * mm, "radius": 2 * mm});
            skCircle(sketch, "E7.0.16.25", {"center": v(142.66, -402.1) * mm, "radius": 2 * mm});
            skCircle(sketch, "E7.0.17.25", {"center": v(158.66, -402.1) * mm, "radius": 2 * mm});
            skCircle(sketch, "E7.0.18.25", {"center": v(174.66, -402.1) * mm, "radius": 2 * mm});
            skCircle(sketch, "E7.0.19.25", {"center": v(190.66, -402.1) * mm, "radius": 2 * mm});
            skCircle(sketch, "E7.0.20.25", {"center": v(206.66, -402.1) * mm, "radius": 2 * mm});
            skCircle(sketch, "E7.0.21.25", {"center": v(222.66, -402.1) * mm, "radius": 2 * mm});
            skCircle(sketch, "E7.0.22.25", {"center": v(238.66, -402.1) * mm, "radius": 2 * mm});
            skCircle(sketch, "E7.0.23.25", {"center": v(254.66, -402.1) * mm, "radius": 2 * mm});
            skCircle(sketch, "E7.0.24.25", {"center": v(270.66, -402.1) * mm, "radius": 2 * mm});
            skCircle(sketch, "E7.0.25.25", {"center": v(286.66, -402.1) * mm, "radius": 2 * mm});
            skCircle(sketch, "E7.0.26.25", {"center": v(302.66, -402.1) * mm, "radius": 2 * mm});
            skCircle(sketch, "E7.0.27.25", {"center": v(318.66, -402.1) * mm, "radius": 2 * mm});
            skCircle(sketch, "E7.0.28.25", {"center": v(334.66, -402.1) * mm, "radius": 2 * mm});
            skCircle(sketch, "E7.0.29.25", {"center": v(350.66, -402.1) * mm, "radius": 2 * mm});
            skCircle(sketch, "E7.0.30.25", {"center": v(366.66, -402.1) * mm, "radius": 2 * mm});
            skCircle(sketch, "E7.0.31.25", {"center": v(382.66, -402.1) * mm, "radius": 2 * mm});
            skCircle(sketch, "E8.0.0.25", {"center": v(-105.34, -410.1) * mm, "radius": 2 * mm});
            skCircle(sketch, "E8.0.1.25", {"center": v(-89.34, -410.1) * mm, "radius": 2 * mm});
            skCircle(sketch, "E8.0.2.25", {"center": v(-73.34, -410.1) * mm, "radius": 2 * mm});
            skCircle(sketch, "E8.0.3.25", {"center": v(-57.34, -410.1) * mm, "radius": 2 * mm});
            skCircle(sketch, "E8.0.4.25", {"center": v(-41.34, -410.1) * mm, "radius": 2 * mm});
            skCircle(sketch, "E8.0.5.25", {"center": v(-25.34, -410.1) * mm, "radius": 2 * mm});
            skCircle(sketch, "E8.0.6.25", {"center": v(-9.34, -410.1) * mm, "radius": 2 * mm});
            skCircle(sketch, "E8.0.7.25", {"center": v(6.66, -410.1) * mm, "radius": 2 * mm});
            skCircle(sketch, "E8.0.8.25", {"center": v(22.66, -410.1) * mm, "radius": 2 * mm});
            skCircle(sketch, "E8.0.9.25", {"center": v(38.66, -410.1) * mm, "radius": 2 * mm});
            skCircle(sketch, "E8.0.10.25", {"center": v(54.66, -410.1) * mm, "radius": 2 * mm});
            skCircle(sketch, "E8.0.11.25", {"center": v(70.66, -410.1) * mm, "radius": 2 * mm});
            skCircle(sketch, "E8.0.12.25", {"center": v(86.66, -410.1) * mm, "radius": 2 * mm});
            skCircle(sketch, "E8.0.13.25", {"center": v(102.66, -410.1) * mm, "radius": 2 * mm});
            skCircle(sketch, "E8.0.14.25", {"center": v(118.66, -410.1) * mm, "radius": 2 * mm});
            skCircle(sketch, "E8.0.15.25", {"center": v(134.66, -410.1) * mm, "radius": 2 * mm});
            skCircle(sketch, "E8.0.16.25", {"center": v(150.66, -410.1) * mm, "radius": 2 * mm});
            skCircle(sketch, "E8.0.17.25", {"center": v(166.66, -410.1) * mm, "radius": 2 * mm});
            skCircle(sketch, "E8.0.18.25", {"center": v(182.66, -410.1) * mm, "radius": 2 * mm});
            skCircle(sketch, "E8.0.19.25", {"center": v(198.66, -410.1) * mm, "radius": 2 * mm});
            skCircle(sketch, "E8.0.20.25", {"center": v(214.66, -410.1) * mm, "radius": 2 * mm});
            skCircle(sketch, "E8.0.21.25", {"center": v(230.66, -410.1) * mm, "radius": 2 * mm});
            skCircle(sketch, "E8.0.22.25", {"center": v(246.66, -410.1) * mm, "radius": 2 * mm});
            skCircle(sketch, "E8.0.23.25", {"center": v(262.66, -410.1) * mm, "radius": 2 * mm});
            skCircle(sketch, "E8.0.24.25", {"center": v(278.66, -410.1) * mm, "radius": 2 * mm});
            skCircle(sketch, "E8.0.25.25", {"center": v(294.66, -410.1) * mm, "radius": 2 * mm});
            skCircle(sketch, "E8.0.26.25", {"center": v(310.66, -410.1) * mm, "radius": 2 * mm});
            skCircle(sketch, "E8.0.27.25", {"center": v(326.66, -410.1) * mm, "radius": 2 * mm});
            skCircle(sketch, "E8.0.28.25", {"center": v(342.66, -410.1) * mm, "radius": 2 * mm});
            skCircle(sketch, "E8.0.29.25", {"center": v(358.66, -410.1) * mm, "radius": 2 * mm});
            skCircle(sketch, "E8.0.30.25", {"center": v(374.66, -410.1) * mm, "radius": 2 * mm});
            skCircle(sketch, "E8.0.31.25", {"center": v(390.66, -410.1) * mm, "radius": 2 * mm});
            skCircle(sketch, "E9.0.0.26", {"center": v(-113.34, -418.1) * mm, "radius": 2 * mm});
            skCircle(sketch, "E9.0.1.26", {"center": v(-97.34, -418.1) * mm, "radius": 2 * mm});
            skCircle(sketch, "E9.0.2.26", {"center": v(-81.34, -418.1) * mm, "radius": 2 * mm});
            skCircle(sketch, "E9.0.3.26", {"center": v(-65.34, -418.1) * mm, "radius": 2 * mm});
            skCircle(sketch, "E9.0.4.26", {"center": v(-49.34, -418.1) * mm, "radius": 2 * mm});
            skCircle(sketch, "E9.0.5.26", {"center": v(-33.34, -418.1) * mm, "radius": 2 * mm});
            skCircle(sketch, "E9.0.6.26", {"center": v(-17.34, -418.1) * mm, "radius": 2 * mm});
            skCircle(sketch, "E9.0.7.26", {"center": v(-1.34, -418.1) * mm, "radius": 2 * mm});
            skCircle(sketch, "E9.0.8.26", {"center": v(14.66, -418.1) * mm, "radius": 2 * mm});
            skCircle(sketch, "E9.0.9.26", {"center": v(30.66, -418.1) * mm, "radius": 2 * mm});
            skCircle(sketch, "E9.0.10.26", {"center": v(46.66, -418.1) * mm, "radius": 2 * mm});
            skCircle(sketch, "E9.0.11.26", {"center": v(62.66, -418.1) * mm, "radius": 2 * mm});
            skCircle(sketch, "E9.0.12.26", {"center": v(78.66, -418.1) * mm, "radius": 2 * mm});
            skCircle(sketch, "E9.0.13.26", {"center": v(94.66, -418.1) * mm, "radius": 2 * mm});
            skCircle(sketch, "E9.0.14.26", {"center": v(110.66, -418.1) * mm, "radius": 2 * mm});
            skCircle(sketch, "E9.0.15.26", {"center": v(126.66, -418.1) * mm, "radius": 2 * mm});
            skCircle(sketch, "E9.0.16.26", {"center": v(142.66, -418.1) * mm, "radius": 2 * mm});
            skCircle(sketch, "E9.0.17.26", {"center": v(158.66, -418.1) * mm, "radius": 2 * mm});
            skCircle(sketch, "E9.0.18.26", {"center": v(174.66, -418.1) * mm, "radius": 2 * mm});
            skCircle(sketch, "E9.0.19.26", {"center": v(190.66, -418.1) * mm, "radius": 2 * mm});
            skCircle(sketch, "E9.0.20.26", {"center": v(206.66, -418.1) * mm, "radius": 2 * mm});
            skCircle(sketch, "E9.0.21.26", {"center": v(222.66, -418.1) * mm, "radius": 2 * mm});
            skCircle(sketch, "E9.0.22.26", {"center": v(238.66, -418.1) * mm, "radius": 2 * mm});
            skCircle(sketch, "E9.0.23.26", {"center": v(254.66, -418.1) * mm, "radius": 2 * mm});
            skCircle(sketch, "E9.0.24.26", {"center": v(270.66, -418.1) * mm, "radius": 2 * mm});
            skCircle(sketch, "E9.0.25.26", {"center": v(286.66, -418.1) * mm, "radius": 2 * mm});
            skCircle(sketch, "E9.0.26.26", {"center": v(302.66, -418.1) * mm, "radius": 2 * mm});
            skCircle(sketch, "E9.0.27.26", {"center": v(318.66, -418.1) * mm, "radius": 2 * mm});
            skCircle(sketch, "E9.0.28.26", {"center": v(334.66, -418.1) * mm, "radius": 2 * mm});
            skCircle(sketch, "E9.0.29.26", {"center": v(350.66, -418.1) * mm, "radius": 2 * mm});
            skCircle(sketch, "E9.0.30.26", {"center": v(366.66, -418.1) * mm, "radius": 2 * mm});
            skCircle(sketch, "E9.0.31.26", {"center": v(382.66, -418.1) * mm, "radius": 2 * mm});
            skSolve(sketch);
        }
        {
            var Q0;
            Q0=makeQuery(id+"F0.imprint","IMPRINT",FACE,{"disambiguationData":[TD([[makeQuery(id+"F0.imprint","IMPRINT",EDGE,{"derivedFrom":sQuery(id+"F0.wireOp",EDGE,"E0.bottom")}),-1.0]])]});
            extrude(context, id + "F1", {"entities" : qUnion([Q0]), "depth" : 1 * mm, "offsetDistance" : 25 * mm});
        }
    });
